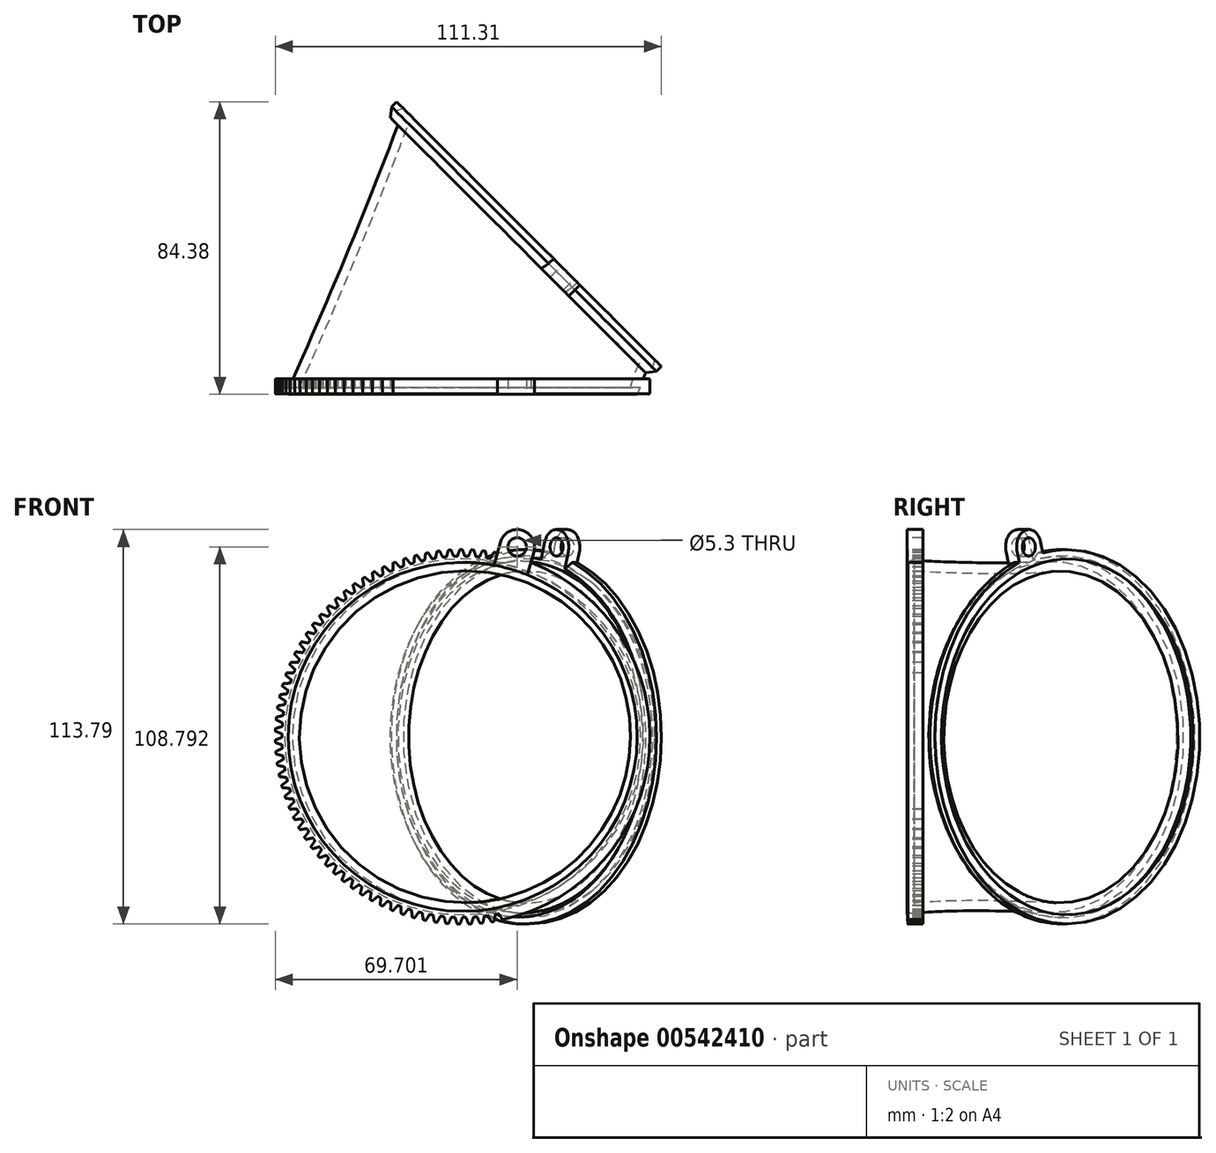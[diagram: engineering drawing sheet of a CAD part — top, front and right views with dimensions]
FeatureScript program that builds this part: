
annotation { "Feature Type Name" : "Feature", "Feature Type Description" : "" }
export const myFeature = defineFeature(function(context is Context, id is Id, definition is map)
    precondition{}
    {
        {
            var Q0;
            Q0=qCreatedBy(makeId("Front.planeOp"),FACE);
            var sketch = newSketch(context, id + "F0", { "sketchPlane" : qUnion([Q0])});
            skCircle(sketch, "E0", {"center": v(0, 0) * mm, "radius": 51 * mm});
            skSolve(sketch);
        }
        {
            var Q0;
            Q0=qCreatedBy(makeId("Top.planeOp"),FACE);
            var sketch = newSketch(context, id + "F1", { "sketchPlane" : qUnion([Q0])});
            skLineSegment(sketch, "E1", {"start": v(36.81, 28.52) * mm, "end": v(1.46, 63.87) * mm});
            skLineSegment(sketch, "E2", {"start": v(25, 0) * mm, "end": v(-25, 0) * mm});
            skLineSegment(sketch, "E3", {"start": v(19.13, 46.2) * mm, "end": v(0, 0) * mm});
            skPoint(sketch, "E4", {"position": v(19.13, 46.2) * mm});
            skLineSegment(sketch, "E5", {"start": v(9.57, 23.1) * mm, "end": v(14.19, 21.18) * mm});
            skSolve(sketch);
        }
        {
            var Q0;
            Q0=sQuery(id+"F1.wireOp",EDGE,"E1");
            cPlane(context, id + "F2", {"entities" : qUnion([Q0]), "cplaneType" : CPlaneType.LINE_ANGLE, "offset" : 25 * mm, "angle" : 90 * degree, "width" : 150 * mm, "height" : 150 * mm});
        }
        {
            var Q0;
            Q0=qCreatedBy(id+"F2.planeOp",FACE);
            var sketch = newSketch(context, id + "F3", { "sketchPlane" : qUnion([Q0])});
            skCircle(sketch, "E6", {"center": v(19.13, 0) * mm, "radius": 51 * mm});
            skSolve(sketch);
        }
        {
            var Q0;
            Q0=makeQuery(id+"F0.imprint","IMPRINT",FACE,{"disambiguationData":[TD([[makeQuery(id+"F0.imprint","IMPRINT",EDGE,{"derivedFrom":sQuery(id+"F0.wireOp",EDGE,"E0")}),1.0]])]});
            var Q1;
            Q1=makeQuery(id+"F3.imprint","IMPRINT",FACE,{"disambiguationData":[TD([[makeQuery(id+"F3.imprint","IMPRINT",EDGE,{"derivedFrom":sQuery(id+"F3.wireOp",EDGE,"E6")}),1.0]])]});
            loft(context, id + "F4", {"sheetProfilesArray" : [{ "sheetProfileEntities" : qUnion([Q0]) }, { "sheetProfileEntities" : qUnion([Q1]) }]});
        }
        {
            var Q0;
            Q0=makeQuery(id+"F4.opLoft","CAP_FACE",FACE,{"disambiguationData":[OSD([makeQuery(id+"F3.imprint","IMPRINT",FACE,{"disambiguationData":[TD([[makeQuery(id+"F3.imprint","IMPRINT",EDGE,{"derivedFrom":sQuery(id+"F3.wireOp",EDGE,"E6")}),1.0]])]})])],"isStart":true});
            var sketch = newSketch(context, id + "F5", { "sketchPlane" : qUnion([Q0])});
            skCircle(sketch, "E7", {"center": v(19.13, 0) * mm, "radius": 48 * mm});
            skSolve(sketch);
        }
        {
            var Q0;
            Q0=makeQuery(id+"F4.opLoft","CAP_FACE",FACE,{"disambiguationData":[OSD([makeQuery(id+"F3.imprint","IMPRINT",FACE,{"disambiguationData":[TD([[makeQuery(id+"F3.imprint","IMPRINT",EDGE,{"derivedFrom":sQuery(id+"F3.wireOp",EDGE,"E6")}),1.0]])]})])],"isStart":true});
            var sketch = newSketch(context, id + "F6", { "sketchPlane" : qUnion([Q0])});
            skCircle(sketch, "E8", {"center": v(19.13, 0) * mm, "radius": 54 * mm});
            skCircle(sketch, "E9", {"center": v(19.13, 0) * mm, "radius": 45 * mm});
            skSolve(sketch);
        }
        {
            var Q0;
            Q0=makeQuery(id+"F6.imprint","IMPRINT",FACE,{"disambiguationData":[TD([[makeQuery(id+"F6.imprint","IMPRINT",EDGE,{"derivedFrom":sQuery(id+"F6.wireOp",EDGE,"E8")}),1.0]])]});
            var Q1;
            Q1=makeQuery(id+"F5.imprint","IMPRINT",FACE,{"disambiguationData":[TD([[makeQuery(id+"F5.imprint","IMPRINT",EDGE,{"derivedFrom":sQuery(id+"F5.wireOp",EDGE,"E7")}),-1.0]])]});
            extrude(context, id + "F7", {"entities" : qUnion([Q0, Q1]), "operationType" : NewBodyOperationType.ADD, "oppositeDirection" : true, "depth" : 4.5 * mm, "offsetDistance" : 25 * mm});
        }
        {
            var Q0;
            Q0=makeQuery(id+"F4.opLoft","CAP_FACE",FACE,{"disambiguationData":[OSD([makeQuery(id+"F0.imprint","IMPRINT",FACE,{"disambiguationData":[TD([[makeQuery(id+"F0.imprint","IMPRINT",EDGE,{"derivedFrom":sQuery(id+"F0.wireOp",EDGE,"E0")}),1.0]])]})])],"isStart":true});
            var sketch = newSketch(context, id + "F8", { "sketchPlane" : qUnion([Q0])});
            skCircle(sketch, "E10", {"center": v(0, 0) * mm, "radius": 54 * mm});
            skSolve(sketch);
        }
        {
            var Q0;
            Q0=makeQuery(id+"F8.imprint","IMPRINT",FACE,{"disambiguationData":[TD([[makeQuery(id+"F8.imprint","IMPRINT",EDGE,{"derivedFrom":sQuery(id+"F8.wireOp",EDGE,"E10")}),1.0]])]});
            var Q1;
            Q1=makeQuery(id+"F8.imprint","IMPRINT",FACE,{"disambiguationData":[TD([[makeQuery(id+"F8.imprint","IMPRINT",EDGE,{"derivedFrom":makeQuery(id+"F4.opLoft","MID_CAP_EDGE",EDGE,{"disambiguationData":[OSD([sQuery(id+"F0.wireOp",EDGE,"E0")])],"capPos":0.0})}),1.0]])]});
            extrude(context, id + "F9", {"entities" : qUnion([Q0, Q1]), "operationType" : NewBodyOperationType.ADD, "oppositeDirection" : true, "depth" : 4.5 * mm, "offsetDistance" : 25 * mm});
        }
        {
            var Q0;
            {var subQ0=sQuery(id+"F3.wireOp",EDGE,"E6");var subQ1=sQuery(id+"F0.wireOp",EDGE,"E0");Q0=makeQuery(id+"F7.boolean.opBoolean","MERGE",FACE,{"derivedFrom":[makeQuery(id+"F4.opLoft","CAP_FACE",FACE,{"disambiguationData":[OSD([makeQuery(id+"F3.imprint","IMPRINT",FACE,{"disambiguationData":[TD([[makeQuery(id+"F3.imprint","IMPRINT",EDGE,{"derivedFrom":subQ0}),1.0]])]})])],"isStart":true}),makeQuery(id+"F7.opExtrude","CAP_FACE",FACE,{"disambiguationData":[OSD([subQ1,subQ0,sQuery(id+"F5.wireOp",EDGE,"E7")])],"isStart":true}),makeQuery(id+"F7.opExtrude","CAP_FACE",FACE,{"disambiguationData":[OSD([subQ1,subQ0,sQuery(id+"F6.wireOp",EDGE,"E8")])],"isStart":true})]});}
            var sketch = newSketch(context, id + "F10", { "sketchPlane" : qUnion([Q0])});
            skCircle(sketch, "E11", {"center": v(19.13, 0) * mm, "radius": 48 * mm});
            skSolve(sketch);
        }
        {
            var Q0;
            Q0=makeQuery(id+"F9.boolean.opBoolean","MERGE",FACE,{"derivedFrom":[makeQuery(id+"F4.opLoft","CAP_FACE",FACE,{"disambiguationData":[OSD([makeQuery(id+"F0.imprint","IMPRINT",FACE,{"disambiguationData":[TD([[makeQuery(id+"F0.imprint","IMPRINT",EDGE,{"derivedFrom":sQuery(id+"F0.wireOp",EDGE,"E0")}),1.0]])]})])],"isStart":true}),makeQuery(id+"F9.opExtrude","CAP_FACE",FACE,{"disambiguationData":[OSD([sQuery(id+"F8.wireOp",EDGE,"E10")])],"isStart":true})]});
            var sketch = newSketch(context, id + "F11", { "sketchPlane" : qUnion([Q0])});
            skCircle(sketch, "E12", {"center": v(0, 0) * mm, "radius": 48 * mm});
            skSolve(sketch);
        }
        {
            var Q1;
            Q1=makeQuery(id+"F11.imprint","IMPRINT",FACE,{"disambiguationData":[TD([[makeQuery(id+"F11.imprint","IMPRINT",EDGE,{"derivedFrom":sQuery(id+"F11.wireOp",EDGE,"E12")}),1.0]])]});
            var Q2;
            Q2=makeQuery(id+"F10.imprint","IMPRINT",FACE,{"disambiguationData":[TD([[makeQuery(id+"F10.imprint","IMPRINT",EDGE,{"derivedFrom":sQuery(id+"F10.wireOp",EDGE,"E11")}),1.0]])]});
            loft(context, id + "F12", {"operationType" : NewBodyOperationType.REMOVE, "sheetProfilesArray" : [{ "sheetProfileEntities" : qUnion([Q1]) }, { "sheetProfileEntities" : qUnion([Q2]) }]});
        }
        {
            var Q0;
            Q0=makeQuery(id+"F9.boolean.opBoolean","MERGE",FACE,{"derivedFrom":[makeQuery(id+"F4.opLoft","CAP_FACE",FACE,{"disambiguationData":[OSD([makeQuery(id+"F0.imprint","IMPRINT",FACE,{"disambiguationData":[TD([[makeQuery(id+"F0.imprint","IMPRINT",EDGE,{"derivedFrom":sQuery(id+"F0.wireOp",EDGE,"E0")}),1.0]])]})])],"isStart":true}),makeQuery(id+"F9.opExtrude","CAP_FACE",FACE,{"disambiguationData":[OSD([sQuery(id+"F8.wireOp",EDGE,"E10")])],"isStart":true})]});
            var sketch = newSketch(context, id + "F13", { "sketchPlane" : qUnion([Q0])});
            skCircle(sketch, "E13", {"center": v(0, 0) * mm, "radius": 50 * mm});
            skCircle(sketch, "E14", {"center": v(0, 0) * mm, "radius": 40 * mm});
            skSolve(sketch);
        }
        {
            var Q0;
            Q0=makeQuery(id+"F13.imprint","IMPRINT",FACE,{"disambiguationData":[TD([[makeQuery(id+"F13.imprint","IMPRINT",EDGE,{"derivedFrom":sQuery(id+"F13.wireOp",EDGE,"E13")}),1.0]])]});
            var Q1;
            Q1=makeQuery(id+"F13.imprint","IMPRINT",FACE,{"disambiguationData":[TD([[makeQuery(id+"F13.imprint","IMPRINT",EDGE,{"derivedFrom":sQuery(id+"F13.wireOp",EDGE,"E14")}),-1.0]])]});
            extrude(context, id + "F14", {"entities" : qUnion([Q0, Q1]), "operationType" : NewBodyOperationType.REMOVE, "oppositeDirection" : true, "depth" : 2 * mm, "offsetDistance" : 25 * mm});
        }
        {
            var Q0;
            {var subQ0=sQuery(id+"F3.wireOp",EDGE,"E6");var subQ1=sQuery(id+"F0.wireOp",EDGE,"E0");Q0=makeQuery(id+"F7.boolean.opBoolean","MERGE",FACE,{"derivedFrom":[makeQuery(id+"F4.opLoft","CAP_FACE",FACE,{"disambiguationData":[OSD([makeQuery(id+"F3.imprint","IMPRINT",FACE,{"disambiguationData":[TD([[makeQuery(id+"F3.imprint","IMPRINT",EDGE,{"derivedFrom":subQ0}),1.0]])]})])],"isStart":true}),makeQuery(id+"F7.opExtrude","CAP_FACE",FACE,{"disambiguationData":[OSD([subQ1,subQ0,sQuery(id+"F5.wireOp",EDGE,"E7")])],"isStart":true}),makeQuery(id+"F7.opExtrude","CAP_FACE",FACE,{"disambiguationData":[OSD([subQ1,subQ0,sQuery(id+"F6.wireOp",EDGE,"E8")])],"isStart":true})]});}
            var sketch = newSketch(context, id + "F15", { "sketchPlane" : qUnion([Q0])});
            skCircle(sketch, "E15", {"center": v(19.13, 0) * mm, "radius": 40 * mm});
            skCircle(sketch, "E16", {"center": v(19.13, 0) * mm, "radius": 51 * mm});
            skSolve(sketch);
        }
        {
            var Q0;
            Q0=makeQuery(id+"F15.imprint","IMPRINT",FACE,{"disambiguationData":[TD([[makeQuery(id+"F15.imprint","IMPRINT",EDGE,{"derivedFrom":sQuery(id+"F15.wireOp",EDGE,"E15")}),-1.0]])]});
            var Q1;
            Q1=makeQuery(id+"F15.imprint","IMPRINT",FACE,{"disambiguationData":[TD([[makeQuery(id+"F15.imprint","IMPRINT",EDGE,{"derivedFrom":sQuery(id+"F15.wireOp",EDGE,"E16")}),1.0]])]});
            extrude(context, id + "F16", {"entities" : qUnion([Q0, Q1]), "operationType" : NewBodyOperationType.REMOVE, "oppositeDirection" : true, "depth" : 2 * mm, "offsetDistance" : 25 * mm});
        }
        {
            var Q0;
            Q0=makeQuery(id+"F9.boolean.opBoolean","MERGE",FACE,{"derivedFrom":[makeQuery(id+"F4.opLoft","CAP_FACE",FACE,{"disambiguationData":[OSD([makeQuery(id+"F0.imprint","IMPRINT",FACE,{"disambiguationData":[TD([[makeQuery(id+"F0.imprint","IMPRINT",EDGE,{"derivedFrom":sQuery(id+"F0.wireOp",EDGE,"E0")}),1.0]])]})])],"isStart":true}),makeQuery(id+"F9.opExtrude","CAP_FACE",FACE,{"disambiguationData":[OSD([sQuery(id+"F8.wireOp",EDGE,"E10")])],"isStart":true})]});
            var sketch = newSketch(context, id + "F17", { "sketchPlane" : qUnion([Q0])});
            skLineSegment(sketch, "E17", {"start": v(0, 0) * mm, "end": v(-20, 0) * mm});
            skLineSegment(sketch, "E18", {"start": v(0, 0) * mm, "end": v(-4.8, 1.38) * mm});
            skLineSegment(sketch, "E19", {"start": v(0, 0) * mm, "end": v(4.8, -1.38) * mm});
            skArc(sketch, "E20", {"start": v(21.84, 58.03) * mm, "mid": v(17.09, 59.6) * mm, "end": v(12.23, 60.78) * mm});
            skLineSegment(sketch, "E21", {"start": v(-4.8, 1.38) * mm, "end": v(12.23, 60.78) * mm});
            skLineSegment(sketch, "E22", {"start": v(4.8, -1.38) * mm, "end": v(21.84, 58.03) * mm});
            skLineSegment(sketch, "E23", {"start": v(0, 0) * mm, "end": v(15.71, 54.8) * mm});
            skCircle(sketch, "E24", {"center": v(15.71, 54.8) * mm, "radius": 2.65 * mm});
            skSolve(sketch);
        }
        {
            var Q0;
            {var subQ1=sQuery(id+"F17.wireOp",EDGE,"E20");Q0=makeQuery(id+"F17.imprint","IMPRINT",FACE,{"disambiguationData":[TD([[makeQuery(id+"F17.imprint","IMPRINT",EDGE,{"derivedFrom":subQ1}),1.0]])]});}
            extrude(context, id + "F18", {"entities" : qUnion([Q0]), "operationType" : NewBodyOperationType.ADD, "oppositeDirection" : true, "depth" : 4.5 * mm, "offsetDistance" : 25 * mm});
        }
        {
            var Q0;
            Q0=makeQuery(id+"F9.opExtrude","CAP_EDGE",EDGE,{"disambiguationData":[OSD([sQuery(id+"F8.wireOp",EDGE,"E10")])],"isStart":true});
            chamfer(context, id + "F19", {"entities" : qUnion([Q0]), "chamferType" : ChamferType.TWO_OFFSETS, "width1" : 4 * mm, "oppositeDirection" : false, "width2" : .2 * mm, "tangentPropagation" : true});
        }
        {
            var Q0;
            Q0=makeQuery(id+"F18.opExtrude","SWEPT_EDGE",EDGE,{"disambiguationData":[OSD([sQuery(id+"F17.wireOp",EDGE,"E20"),sQuery(id+"F17.wireOp",EDGE,"E21")])]});
            var Q1;
            Q1=makeQuery(id+"F18.opExtrude","SWEPT_EDGE",EDGE,{"disambiguationData":[OSD([sQuery(id+"F17.wireOp",EDGE,"E20"),sQuery(id+"F17.wireOp",EDGE,"E22")])]});
            fillet(context, id + "F20", {"entities" : qUnion([Q0, Q1]), "radius" : 5 * mm, "tangentPropagation" : true, "allowEdgeOverflow" : false});
        }
        {
            var Q0;
            {var subQ0=sQuery(id+"F3.wireOp",EDGE,"E6");var subQ1=sQuery(id+"F0.wireOp",EDGE,"E0");Q0=makeQuery(id+"F7.boolean.opBoolean","MERGE",FACE,{"derivedFrom":[makeQuery(id+"F4.opLoft","CAP_FACE",FACE,{"disambiguationData":[OSD([makeQuery(id+"F3.imprint","IMPRINT",FACE,{"disambiguationData":[TD([[makeQuery(id+"F3.imprint","IMPRINT",EDGE,{"derivedFrom":subQ0}),1.0]])]})])],"isStart":true}),makeQuery(id+"F7.opExtrude","CAP_FACE",FACE,{"disambiguationData":[OSD([subQ1,subQ0,sQuery(id+"F5.wireOp",EDGE,"E7")])],"isStart":true}),makeQuery(id+"F7.opExtrude","CAP_FACE",FACE,{"disambiguationData":[OSD([subQ1,subQ0,sQuery(id+"F6.wireOp",EDGE,"E8")])],"isStart":true})]});}
            var sketch = newSketch(context, id + "F21", { "sketchPlane" : qUnion([Q0])});
            skArc(sketch, "E25", {"start": v(6.9, 60.78) * mm, "mid": v(2.04, 59.6) * mm, "end": v(-2.7, 58.03) * mm});
            skLineSegment(sketch, "E26", {"start": v(19.13, 0) * mm, "end": v(39.13, 0) * mm});
            skLineSegment(sketch, "E27", {"start": v(19.13, 0) * mm, "end": v(23.94, 1.38) * mm});
            skLineSegment(sketch, "E28", {"start": v(23.94, 1.38) * mm, "end": v(6.9, 60.78) * mm});
            skLineSegment(sketch, "E29", {"start": v(23.94, 1.38) * mm, "end": v(14.33, -1.38) * mm});
            skLineSegment(sketch, "E30", {"start": v(14.33, -1.38) * mm, "end": v(-2.7, 58.03) * mm});
            skLineSegment(sketch, "E31", {"start": v(19.13, 0) * mm, "end": v(3.42, 54.8) * mm});
            skCircle(sketch, "E32", {"center": v(3.42, 54.8) * mm, "radius": 2.65 * mm});
            skSolve(sketch);
        }
        {
            var Q0;
            {var subQ0=sQuery(id+"F21.wireOp",EDGE,"E25");Q0=makeQuery(id+"F21.imprint","IMPRINT",FACE,{"disambiguationData":[TD([[makeQuery(id+"F21.imprint","IMPRINT",EDGE,{"derivedFrom":subQ0}),1.0]])]});}
            extrude(context, id + "F22", {"entities" : qUnion([Q0]), "operationType" : NewBodyOperationType.ADD, "oppositeDirection" : true, "depth" : 4.5 * mm, "offsetDistance" : 25 * mm});
        }
        {
            var Q0;
            Q0=makeQuery(id+"F22.opExtrude","SWEPT_EDGE",EDGE,{"disambiguationData":[OSD([sQuery(id+"F21.wireOp",EDGE,"E25"),sQuery(id+"F21.wireOp",EDGE,"E30")])]});
            var Q1;
            Q1=makeQuery(id+"F22.opExtrude","SWEPT_EDGE",EDGE,{"disambiguationData":[OSD([sQuery(id+"F21.wireOp",EDGE,"E25"),sQuery(id+"F21.wireOp",EDGE,"E28")])]});
            fillet(context, id + "F23", {"entities" : qUnion([Q0, Q1]), "radius" : 5 * mm, "tangentPropagation" : true, "allowEdgeOverflow" : false});
        }
        {
            var Q0;
            Q0=makeQuery(id+"F7.opExtrude","CAP_EDGE",EDGE,{"disambiguationData":[OSD([sQuery(id+"F6.wireOp",EDGE,"E8")])],"isStart":false});
            chamfer(context, id + "F24", {"entities" : qUnion([Q0]), "chamferType" : ChamferType.TWO_OFFSETS, "width1" : 2.5 * mm, "oppositeDirection" : false, "width2" : 2 * mm, "tangentPropagation" : true});
        }
        {
            var Q0;
            {var subQ0=sQuery(id+"F8.wireOp",EDGE,"E10");Q0=makeQuery(id+"F18.boolean.opBoolean","MERGE",FACE,{"derivedFrom":[makeQuery(id+"F9.boolean.opBoolean","MERGE",FACE,{"derivedFrom":[makeQuery(id+"F4.opLoft","CAP_FACE",FACE,{"disambiguationData":[OSD([makeQuery(id+"F0.imprint","IMPRINT",FACE,{"disambiguationData":[TD([[makeQuery(id+"F0.imprint","IMPRINT",EDGE,{"derivedFrom":sQuery(id+"F0.wireOp",EDGE,"E0")}),1.0]])]})])],"isStart":true}),makeQuery(id+"F9.opExtrude","CAP_FACE",FACE,{"disambiguationData":[OSD([subQ0])],"isStart":true})]}),makeQuery(id+"F18.opExtrude","CAP_FACE",FACE,{"disambiguationData":[OSD([subQ0,sQuery(id+"F17.wireOp",EDGE,"E20"),sQuery(id+"F17.wireOp",EDGE,"E21"),sQuery(id+"F17.wireOp",EDGE,"E22"),sQuery(id+"F17.wireOp",EDGE,"E24")])],"isStart":true})]});}
            var sketch = newSketch(context, id + "F25", { "sketchPlane" : qUnion([Q0])});
            skArc(sketch, "E33", {"start": v(9.38, 53.18) * mm, "mid": v(9.25, 53.2) * mm, "end": v(9.12, 53.22) * mm});
            skLineSegment(sketch, "E34", {"start": v(0, 0) * mm, "end": v(9.38, 53.18) * mm});
            skLineSegment(sketch, "E35", {"start": v(0, 0) * mm, "end": v(9.42, 0) * mm});
            skLineSegment(sketch, "E36", {"start": v(0, 0) * mm, "end": v(6.11, 53.65) * mm});
            skLineSegment(sketch, "E37", {"start": v(0, 0) * mm, "end": v(8.97, 53.2) * mm});
            skLineSegment(sketch, "E38", {"start": v(0, 0) * mm, "end": v(6.5, 53.55) * mm});
            skLineSegment(sketch, "E39", {"start": v(7.75, 53.43) * mm, "end": v(0, 0) * mm});
            skLineSegment(sketch, "E40", {"start": v(6.54, 53.47) * mm, "end": v(6.93, 51.77) * mm});
            skLineSegment(sketch, "E41", {"start": v(8.05, 51.6) * mm, "end": v(8.91, 53.13) * mm});
            skArc(sketch, "E42", {"start": v(9.05, 51.3) * mm, "mid": v(8.86, 51.34) * mm, "end": v(8.67, 51.37) * mm});
            skLineSegment(sketch, "E43", {"start": v(9.38, 53.18) * mm, "end": v(9.11, 53.23) * mm});
            skArc(sketch, "E44.trimOffspring", {"start": v(6.37, 53.62) * mm, "mid": v(6.24, 53.64) * mm, "end": v(6.11, 53.65) * mm});
            skPoint(sketch, "E45.visualSharp", {"position": v(6.5, 53.6) * mm});
            skArc(sketch, "E45.filletArc", {"start": v(6.54, 53.47) * mm, "mid": v(6.48, 53.57) * mm, "end": v(6.37, 53.62) * mm});
            skPoint(sketch, "E46.visualSharp", {"position": v(8.98, 53.25) * mm});
            skArc(sketch, "E46.filletArc", {"start": v(9.12, 53.22) * mm, "mid": v(9, 53.2) * mm, "end": v(8.91, 53.13) * mm});
            skArc(sketch, "E47.trimOffspring", {"start": v(7.85, 51.5) * mm, "mid": v(7.48, 51.56) * mm, "end": v(7.1, 51.61) * mm});
            skPoint(sketch, "E48.visualSharp", {"position": v(6.96, 51.63) * mm});
            skArc(sketch, "E48.filletArc", {"start": v(6.93, 51.77) * mm, "mid": v(7, 51.66) * mm, "end": v(7.1, 51.61) * mm});
            skPoint(sketch, "E49.visualSharp", {"position": v(7.99, 51.48) * mm});
            skArc(sketch, "E49.filletArc", {"start": v(7.85, 51.5) * mm, "mid": v(7.97, 51.52) * mm, "end": v(8.05, 51.6) * mm});
            skLineSegment(sketch, "E50", {"start": v(6.11, 53.65) * mm, "end": v(8.15, 53.9) * mm});
            skLineSegment(sketch, "E51", {"start": v(8.15, 53.9) * mm, "end": v(9.38, 53.18) * mm});
            skLineSegment(sketch, "E52.1.0", {"start": v(4.85, 54.3) * mm, "end": v(6.12, 53.65) * mm});
            skPoint(sketch, "E52.1.1", {"position": v(4.83, 51.88) * mm});
            skPoint(sketch, "E52.1.2", {"position": v(5.72, 53.7) * mm});
            skArc(sketch, "E52.1.3", {"start": v(4.7, 51.89) * mm, "mid": v(4.32, 51.92) * mm, "end": v(3.94, 51.95) * mm});
            skPoint(sketch, "E52.1.4", {"position": v(3.23, 53.9) * mm});
            skPoint(sketch, "E52.1.5", {"position": v(3.8, 51.96) * mm});
            skLineSegment(sketch, "E52.1.6", {"start": v(4.9, 52) * mm, "end": v(5.66, 53.57) * mm});
            skLineSegment(sketch, "E52.1.7", {"start": v(2.83, 53.93) * mm, "end": v(4.85, 54.3) * mm});
            skLineSegment(sketch, "E52.1.8", {"start": v(3.27, 53.77) * mm, "end": v(3.76, 52.1) * mm});
            skArc(sketch, "E52.1.9", {"start": v(4.7, 51.89) * mm, "mid": v(4.81, 51.91) * mm, "end": v(4.9, 52) * mm});
            skArc(sketch, "E52.1.10", {"start": v(3.76, 52.1) * mm, "mid": v(3.83, 52) * mm, "end": v(3.94, 51.95) * mm});
            skArc(sketch, "E52.1.11", {"start": v(3.27, 53.77) * mm, "mid": v(3.2, 53.87) * mm, "end": v(3.09, 53.91) * mm});
            skArc(sketch, "E52.1.12", {"start": v(5.86, 53.68) * mm, "mid": v(5.74, 53.66) * mm, "end": v(5.66, 53.57) * mm});
            skArc(sketch, "E52.1.13", {"start": v(6.12, 53.65) * mm, "mid": v(5.99, 53.67) * mm, "end": v(5.86, 53.68) * mm});
            skArc(sketch, "E52.1.14", {"start": v(3.09, 53.91) * mm, "mid": v(2.96, 53.92) * mm, "end": v(2.83, 53.93) * mm});
            skLineSegment(sketch, "E52.1.15", {"start": v(6.12, 53.65) * mm, "end": v(5.85, 53.68) * mm});
            skLineSegment(sketch, "E52.2.0", {"start": v(1.53, 54.5) * mm, "end": v(2.84, 53.93) * mm});
            skPoint(sketch, "E52.2.1", {"position": v(1.66, 52.07) * mm});
            skPoint(sketch, "E52.2.2", {"position": v(2.44, 53.95) * mm});
            skArc(sketch, "E52.2.3", {"start": v(1.52, 52.08) * mm, "mid": v(1.14, 52.09) * mm, "end": v(0.77, 52.1) * mm});
            skPoint(sketch, "E52.2.4", {"position": v(-0.06, 54) * mm});
            skPoint(sketch, "E52.2.5", {"position": v(0.63, 52.1) * mm});
            skLineSegment(sketch, "E52.2.6", {"start": v(1.71, 52.2) * mm, "end": v(2.38, 53.82) * mm});
            skLineSegment(sketch, "E52.2.7", {"start": v(-0.46, 54) * mm, "end": v(1.53, 54.5) * mm});
            skLineSegment(sketch, "E52.2.8", {"start": v(-0.02, 53.87) * mm, "end": v(0.58, 52.23) * mm});
            skArc(sketch, "E52.2.9", {"start": v(1.52, 52.08) * mm, "mid": v(1.64, 52.1) * mm, "end": v(1.71, 52.2) * mm});
            skArc(sketch, "E52.2.10", {"start": v(0.58, 52.23) * mm, "mid": v(0.65, 52.13) * mm, "end": v(0.77, 52.1) * mm});
            skArc(sketch, "E52.2.11", {"start": v(-0.02, 53.87) * mm, "mid": v(-0.09, 53.96) * mm, "end": v(-0.2, 54) * mm});
            skArc(sketch, "E52.2.12", {"start": v(2.58, 53.94) * mm, "mid": v(2.46, 53.9) * mm, "end": v(2.38, 53.82) * mm});
            skArc(sketch, "E52.2.13", {"start": v(2.84, 53.93) * mm, "mid": v(2.7, 53.93) * mm, "end": v(2.58, 53.94) * mm});
            skArc(sketch, "E52.2.14", {"start": v(-0.2, 54) * mm, "mid": v(-0.33, 54) * mm, "end": v(-0.46, 54) * mm});
            skLineSegment(sketch, "E52.2.15", {"start": v(2.84, 53.93) * mm, "end": v(2.56, 53.94) * mm});
            skLineSegment(sketch, "E52.3.0", {"start": v(-1.8, 54.48) * mm, "end": v(-0.46, 54) * mm});
            skPoint(sketch, "E52.3.1", {"position": v(-1.52, 52.08) * mm});
            skPoint(sketch, "E52.3.2", {"position": v(-0.86, 54) * mm});
            skArc(sketch, "E52.3.3", {"start": v(-1.66, 52.07) * mm, "mid": v(-2.03, 52.06) * mm, "end": v(-2.41, 52.04) * mm});
            skPoint(sketch, "E52.3.4", {"position": v(-3.36, 53.9) * mm});
            skPoint(sketch, "E52.3.5", {"position": v(-2.55, 52.04) * mm});
            skLineSegment(sketch, "E52.3.6", {"start": v(-1.47, 52.2) * mm, "end": v(-0.9, 53.86) * mm});
            skLineSegment(sketch, "E52.3.7", {"start": v(-3.75, 53.87) * mm, "end": v(-1.8, 54.48) * mm});
            skLineSegment(sketch, "E52.3.8", {"start": v(-3.3, 53.77) * mm, "end": v(-2.6, 52.16) * mm});
            skArc(sketch, "E52.3.9", {"start": v(-1.66, 52.07) * mm, "mid": v(-1.54, 52.11) * mm, "end": v(-1.47, 52.2) * mm});
            skArc(sketch, "E52.3.10", {"start": v(-2.6, 52.16) * mm, "mid": v(-2.53, 52.07) * mm, "end": v(-2.41, 52.04) * mm});
            skArc(sketch, "E52.3.11", {"start": v(-3.3, 53.77) * mm, "mid": v(-3.38, 53.86) * mm, "end": v(-3.5, 53.89) * mm});
            skArc(sketch, "E52.3.12", {"start": v(-0.72, 54) * mm, "mid": v(-0.83, 53.96) * mm, "end": v(-0.9, 53.86) * mm});
            skArc(sketch, "E52.3.13", {"start": v(-0.46, 54) * mm, "mid": v(-0.59, 54) * mm, "end": v(-0.72, 54) * mm});
            skArc(sketch, "E52.3.14", {"start": v(-3.5, 53.89) * mm, "mid": v(-3.63, 53.88) * mm, "end": v(-3.75, 53.87) * mm});
            skLineSegment(sketch, "E52.3.15", {"start": v(-0.46, 54) * mm, "end": v(-0.73, 54) * mm});
            skLineSegment(sketch, "E52.4.0", {"start": v(-5.12, 54.27) * mm, "end": v(-3.75, 53.87) * mm});
            skPoint(sketch, "E52.4.1", {"position": v(-4.69, 51.89) * mm});
            skPoint(sketch, "E52.4.2", {"position": v(-4.15, 53.84) * mm});
            skArc(sketch, "E52.4.3", {"start": v(-4.83, 51.88) * mm, "mid": v(-5.2, 51.84) * mm, "end": v(-5.58, 51.8) * mm});
            skPoint(sketch, "E52.4.4", {"position": v(-6.64, 53.6) * mm});
            skPoint(sketch, "E52.4.5", {"position": v(-5.72, 51.79) * mm});
            skLineSegment(sketch, "E52.4.6", {"start": v(-4.65, 52.02) * mm, "end": v(-4.19, 53.7) * mm});
            skLineSegment(sketch, "E52.4.7", {"start": v(-7.03, 53.54) * mm, "end": v(-5.12, 54.27) * mm});
            skLineSegment(sketch, "E52.4.8", {"start": v(-6.57, 53.47) * mm, "end": v(-5.78, 51.9) * mm});
            skArc(sketch, "E52.4.9", {"start": v(-4.83, 51.88) * mm, "mid": v(-4.72, 51.92) * mm, "end": v(-4.65, 52.02) * mm});
            skArc(sketch, "E52.4.10", {"start": v(-5.78, 51.9) * mm, "mid": v(-5.7, 51.82) * mm, "end": v(-5.58, 51.8) * mm});
            skArc(sketch, "E52.4.11", {"start": v(-6.57, 53.47) * mm, "mid": v(-6.66, 53.55) * mm, "end": v(-6.77, 53.57) * mm});
            skArc(sketch, "E52.4.12", {"start": v(-4, 53.85) * mm, "mid": v(-4.12, 53.8) * mm, "end": v(-4.19, 53.7) * mm});
            skArc(sketch, "E52.4.13", {"start": v(-3.75, 53.87) * mm, "mid": v(-3.88, 53.86) * mm, "end": v(-4, 53.85) * mm});
            skArc(sketch, "E52.4.14", {"start": v(-6.77, 53.57) * mm, "mid": v(-6.9, 53.56) * mm, "end": v(-7.03, 53.54) * mm});
            skLineSegment(sketch, "E52.4.15", {"start": v(-3.75, 53.87) * mm, "end": v(-4.02, 53.85) * mm});
            skLineSegment(sketch, "E52.5.0", {"start": v(-8.41, 53.86) * mm, "end": v(-7.03, 53.54) * mm});
            skPoint(sketch, "E52.5.1", {"position": v(-7.84, 51.5) * mm});
            skPoint(sketch, "E52.5.2", {"position": v(-7.42, 53.49) * mm});
            skArc(sketch, "E52.5.3", {"start": v(-7.98, 51.49) * mm, "mid": v(-8.35, 51.43) * mm, "end": v(-8.73, 51.36) * mm});
            skPoint(sketch, "E52.5.4", {"position": v(-9.9, 53.09) * mm});
            skPoint(sketch, "E52.5.5", {"position": v(-8.86, 51.34) * mm});
            skLineSegment(sketch, "E52.5.6", {"start": v(-7.82, 51.64) * mm, "end": v(-7.45, 53.35) * mm});
            skLineSegment(sketch, "E52.5.7", {"start": v(-10.28, 53.01) * mm, "end": v(-8.41, 53.86) * mm});
            skLineSegment(sketch, "E52.5.8", {"start": v(-9.82, 52.97) * mm, "end": v(-8.93, 51.46) * mm});
            skArc(sketch, "E52.5.9", {"start": v(-7.98, 51.49) * mm, "mid": v(-7.87, 51.54) * mm, "end": v(-7.82, 51.64) * mm});
            skArc(sketch, "E52.5.10", {"start": v(-8.93, 51.46) * mm, "mid": v(-8.84, 51.38) * mm, "end": v(-8.73, 51.36) * mm});
            skArc(sketch, "E52.5.11", {"start": v(-9.82, 52.97) * mm, "mid": v(-9.9, 53.05) * mm, "end": v(-10.03, 53.06) * mm});
            skArc(sketch, "E52.5.12", {"start": v(-7.28, 53.5) * mm, "mid": v(-7.4, 53.46) * mm, "end": v(-7.45, 53.35) * mm});
            skArc(sketch, "E52.5.13", {"start": v(-7.03, 53.54) * mm, "mid": v(-7.15, 53.52) * mm, "end": v(-7.28, 53.5) * mm});
            skArc(sketch, "E52.5.14", {"start": v(-10.03, 53.06) * mm, "mid": v(-10.16, 53.04) * mm, "end": v(-10.28, 53.01) * mm});
            skLineSegment(sketch, "E52.5.15", {"start": v(-7.03, 53.54) * mm, "end": v(-7.3, 53.5) * mm});
            skLineSegment(sketch, "E52.6.0", {"start": v(-11.68, 53.25) * mm, "end": v(-10.28, 53.01) * mm});
            skPoint(sketch, "E52.6.1", {"position": v(-10.97, 50.93) * mm});
            skPoint(sketch, "E52.6.2", {"position": v(-10.67, 52.94) * mm});
            skArc(sketch, "E52.6.3", {"start": v(-11.1, 50.9) * mm, "mid": v(-11.47, 50.82) * mm, "end": v(-11.84, 50.74) * mm});
            skPoint(sketch, "E52.6.4", {"position": v(-13.1, 52.38) * mm});
            skPoint(sketch, "E52.6.5", {"position": v(-11.98, 50.7) * mm});
            skLineSegment(sketch, "E52.6.6", {"start": v(-10.95, 51.07) * mm, "end": v(-10.69, 52.8) * mm});
            skLineSegment(sketch, "E52.6.7", {"start": v(-13.5, 52.29) * mm, "end": v(-11.68, 53.25) * mm});
            skLineSegment(sketch, "E52.6.8", {"start": v(-13.03, 52.27) * mm, "end": v(-12.05, 50.82) * mm});
            skArc(sketch, "E52.6.9", {"start": v(-11.1, 50.9) * mm, "mid": v(-11, 50.96) * mm, "end": v(-10.95, 51.07) * mm});
            skArc(sketch, "E52.6.10", {"start": v(-12.05, 50.82) * mm, "mid": v(-11.96, 50.74) * mm, "end": v(-11.84, 50.74) * mm});
            skArc(sketch, "E52.6.11", {"start": v(-13.03, 52.27) * mm, "mid": v(-13.12, 52.34) * mm, "end": v(-13.24, 52.35) * mm});
            skArc(sketch, "E52.6.12", {"start": v(-10.53, 52.96) * mm, "mid": v(-10.64, 52.9) * mm, "end": v(-10.69, 52.8) * mm});
            skArc(sketch, "E52.6.13", {"start": v(-10.28, 53.01) * mm, "mid": v(-10.4, 52.99) * mm, "end": v(-10.53, 52.96) * mm});
            skArc(sketch, "E52.6.14", {"start": v(-13.24, 52.35) * mm, "mid": v(-13.37, 52.32) * mm, "end": v(-13.5, 52.29) * mm});
            skLineSegment(sketch, "E52.6.15", {"start": v(-10.28, 53.01) * mm, "end": v(-10.54, 52.96) * mm});
            skLineSegment(sketch, "E52.7.0", {"start": v(-14.9, 52.43) * mm, "end": v(-13.49, 52.29) * mm});
            skPoint(sketch, "E52.7.1", {"position": v(-14.05, 50.17) * mm});
            skPoint(sketch, "E52.7.2", {"position": v(-13.88, 52.19) * mm});
            skArc(sketch, "E52.7.3", {"start": v(-14.19, 50.13) * mm, "mid": v(-14.55, 50.03) * mm, "end": v(-14.91, 49.92) * mm});
            skPoint(sketch, "E52.7.4", {"position": v(-16.28, 51.49) * mm});
            skPoint(sketch, "E52.7.5", {"position": v(-15.04, 49.88) * mm});
            skLineSegment(sketch, "E52.7.6", {"start": v(-14.04, 50.3) * mm, "end": v(-13.89, 52.05) * mm});
            skLineSegment(sketch, "E52.7.7", {"start": v(-16.66, 51.37) * mm, "end": v(-14.9, 52.43) * mm});
            skLineSegment(sketch, "E52.7.8", {"start": v(-16.2, 51.38) * mm, "end": v(-15.13, 50) * mm});
            skArc(sketch, "E52.7.9", {"start": v(-14.19, 50.13) * mm, "mid": v(-14.09, 50.2) * mm, "end": v(-14.04, 50.3) * mm});
            skArc(sketch, "E52.7.10", {"start": v(-15.13, 50) * mm, "mid": v(-15.03, 49.92) * mm, "end": v(-14.91, 49.92) * mm});
            skArc(sketch, "E52.7.11", {"start": v(-16.2, 51.38) * mm, "mid": v(-16.3, 51.45) * mm, "end": v(-16.41, 51.45) * mm});
            skArc(sketch, "E52.7.12", {"start": v(-13.74, 52.22) * mm, "mid": v(-13.84, 52.16) * mm, "end": v(-13.89, 52.05) * mm});
            skArc(sketch, "E52.7.13", {"start": v(-13.49, 52.29) * mm, "mid": v(-13.62, 52.26) * mm, "end": v(-13.74, 52.22) * mm});
            skArc(sketch, "E52.7.14", {"start": v(-16.41, 51.45) * mm, "mid": v(-16.53, 51.4) * mm, "end": v(-16.66, 51.37) * mm});
            skLineSegment(sketch, "E52.7.15", {"start": v(-13.49, 52.29) * mm, "end": v(-13.75, 52.22) * mm});
            skLineSegment(sketch, "E52.8.0", {"start": v(-18.08, 51.43) * mm, "end": v(-16.65, 51.37) * mm});
            skPoint(sketch, "E52.8.1", {"position": v(-17.09, 49.22) * mm});
            skPoint(sketch, "E52.8.2", {"position": v(-17.03, 51.24) * mm});
            skArc(sketch, "E52.8.3", {"start": v(-17.22, 49.17) * mm, "mid": v(-17.57, 49.05) * mm, "end": v(-17.93, 48.92) * mm});
            skPoint(sketch, "E52.8.4", {"position": v(-19.39, 50.4) * mm});
            skPoint(sketch, "E52.8.5", {"position": v(-18.06, 48.87) * mm});
            skLineSegment(sketch, "E52.8.6", {"start": v(-17.08, 49.36) * mm, "end": v(-17.04, 51.1) * mm});
            skLineSegment(sketch, "E52.8.7", {"start": v(-19.76, 50.26) * mm, "end": v(-18.08, 51.43) * mm});
            skLineSegment(sketch, "E52.8.8", {"start": v(-19.3, 50.3) * mm, "end": v(-18.15, 48.97) * mm});
            skArc(sketch, "E52.8.9", {"start": v(-17.22, 49.17) * mm, "mid": v(-17.12, 49.24) * mm, "end": v(-17.08, 49.36) * mm});
            skArc(sketch, "E52.8.10", {"start": v(-18.15, 48.97) * mm, "mid": v(-18.05, 48.91) * mm, "end": v(-17.93, 48.92) * mm});
            skArc(sketch, "E52.8.11", {"start": v(-19.3, 50.3) * mm, "mid": v(-19.4, 50.36) * mm, "end": v(-19.52, 50.35) * mm});
            skArc(sketch, "E52.8.12", {"start": v(-16.9, 51.29) * mm, "mid": v(-17, 51.22) * mm, "end": v(-17.04, 51.1) * mm});
            skArc(sketch, "E52.8.13", {"start": v(-16.65, 51.37) * mm, "mid": v(-16.78, 51.33) * mm, "end": v(-16.9, 51.29) * mm});
            skArc(sketch, "E52.8.14", {"start": v(-19.52, 50.35) * mm, "mid": v(-19.64, 50.3) * mm, "end": v(-19.76, 50.26) * mm});
            skLineSegment(sketch, "E52.8.15", {"start": v(-16.65, 51.37) * mm, "end": v(-16.9, 51.28) * mm});
            skLineSegment(sketch, "E52.9.0", {"start": v(-21.18, 50.23) * mm, "end": v(-19.75, 50.26) * mm});
            skPoint(sketch, "E52.9.1", {"position": v(-20.06, 48.09) * mm});
            skPoint(sketch, "E52.9.2", {"position": v(-20.12, 50.1) * mm});
            skArc(sketch, "E52.9.3", {"start": v(-20.18, 48.03) * mm, "mid": v(-20.53, 47.88) * mm, "end": v(-20.88, 47.73) * mm});
            skPoint(sketch, "E52.9.4", {"position": v(-22.42, 49.12) * mm});
            skPoint(sketch, "E52.9.5", {"position": v(-21, 47.68) * mm});
            skLineSegment(sketch, "E52.9.6", {"start": v(-20.06, 48.22) * mm, "end": v(-20.12, 49.97) * mm});
            skLineSegment(sketch, "E52.9.7", {"start": v(-22.79, 48.96) * mm, "end": v(-21.18, 50.23) * mm});
            skLineSegment(sketch, "E52.9.8", {"start": v(-22.32, 49.02) * mm, "end": v(-21.1, 47.78) * mm});
            skArc(sketch, "E52.9.9", {"start": v(-20.18, 48.03) * mm, "mid": v(-20.1, 48.1) * mm, "end": v(-20.06, 48.22) * mm});
            skArc(sketch, "E52.9.10", {"start": v(-21.1, 47.78) * mm, "mid": v(-21, 47.72) * mm, "end": v(-20.88, 47.73) * mm});
            skArc(sketch, "E52.9.11", {"start": v(-22.32, 49.02) * mm, "mid": v(-22.43, 49.08) * mm, "end": v(-22.55, 49.07) * mm});
            skArc(sketch, "E52.9.12", {"start": v(-20, 50.16) * mm, "mid": v(-20.09, 50.09) * mm, "end": v(-20.12, 49.97) * mm});
            skArc(sketch, "E52.9.13", {"start": v(-19.75, 50.26) * mm, "mid": v(-19.87, 50.21) * mm, "end": v(-20, 50.16) * mm});
            skArc(sketch, "E52.9.14", {"start": v(-22.55, 49.07) * mm, "mid": v(-22.67, 49.01) * mm, "end": v(-22.79, 48.96) * mm});
            skLineSegment(sketch, "E52.9.15", {"start": v(-19.75, 50.26) * mm, "end": v(-20, 50.16) * mm});
            skLineSegment(sketch, "E52.10.0", {"start": v(-24.2, 48.85) * mm, "end": v(-22.78, 48.96) * mm});
            skPoint(sketch, "E52.10.1", {"position": v(-22.95, 46.77) * mm});
            skPoint(sketch, "E52.10.2", {"position": v(-23.14, 48.79) * mm});
            skArc(sketch, "E52.10.3", {"start": v(-23.07, 46.71) * mm, "mid": v(-23.41, 46.54) * mm, "end": v(-23.75, 46.37) * mm});
            skPoint(sketch, "E52.10.4", {"position": v(-25.38, 47.67) * mm});
            skPoint(sketch, "E52.10.5", {"position": v(-23.87, 46.3) * mm});
            skLineSegment(sketch, "E52.10.6", {"start": v(-22.96, 46.91) * mm, "end": v(-23.13, 48.65) * mm});
            skLineSegment(sketch, "E52.10.7", {"start": v(-25.73, 47.48) * mm, "end": v(-24.2, 48.85) * mm});
            skLineSegment(sketch, "E52.10.8", {"start": v(-25.27, 47.57) * mm, "end": v(-23.97, 46.4) * mm});
            skArc(sketch, "E52.10.9", {"start": v(-23.07, 46.71) * mm, "mid": v(-22.99, 46.8) * mm, "end": v(-22.96, 46.91) * mm});
            skArc(sketch, "E52.10.10", {"start": v(-23.97, 46.4) * mm, "mid": v(-23.87, 46.35) * mm, "end": v(-23.75, 46.37) * mm});
            skArc(sketch, "E52.10.11", {"start": v(-25.27, 47.57) * mm, "mid": v(-25.38, 47.62) * mm, "end": v(-25.5, 47.6) * mm});
            skArc(sketch, "E52.10.12", {"start": v(-23.01, 48.85) * mm, "mid": v(-23.1, 48.77) * mm, "end": v(-23.13, 48.65) * mm});
            skArc(sketch, "E52.10.13", {"start": v(-22.78, 48.96) * mm, "mid": v(-22.9, 48.9) * mm, "end": v(-23.01, 48.85) * mm});
            skArc(sketch, "E52.10.14", {"start": v(-25.5, 47.6) * mm, "mid": v(-25.61, 47.54) * mm, "end": v(-25.73, 47.48) * mm});
            skLineSegment(sketch, "E52.10.15", {"start": v(-22.78, 48.96) * mm, "end": v(-23.02, 48.84) * mm});
            skLineSegment(sketch, "E52.11.0", {"start": v(-27.13, 47.28) * mm, "end": v(-25.72, 47.48) * mm});
            skPoint(sketch, "E52.11.1", {"position": v(-25.76, 45.29) * mm});
            skPoint(sketch, "E52.11.2", {"position": v(-26.07, 47.29) * mm});
            skArc(sketch, "E52.11.3", {"start": v(-25.88, 45.22) * mm, "mid": v(-26.2, 45.03) * mm, "end": v(-26.53, 44.84) * mm});
            skPoint(sketch, "E52.11.4", {"position": v(-28.23, 46.03) * mm});
            skPoint(sketch, "E52.11.5", {"position": v(-26.65, 44.77) * mm});
            skLineSegment(sketch, "E52.11.6", {"start": v(-25.78, 45.42) * mm, "end": v(-26.05, 47.15) * mm});
            skLineSegment(sketch, "E52.11.7", {"start": v(-28.57, 45.82) * mm, "end": v(-27.13, 47.28) * mm});
            skLineSegment(sketch, "E52.11.8", {"start": v(-28.12, 45.94) * mm, "end": v(-26.76, 44.85) * mm});
            skArc(sketch, "E52.11.9", {"start": v(-25.88, 45.22) * mm, "mid": v(-25.8, 45.3) * mm, "end": v(-25.78, 45.42) * mm});
            skArc(sketch, "E52.11.10", {"start": v(-26.76, 44.85) * mm, "mid": v(-26.65, 44.81) * mm, "end": v(-26.53, 44.84) * mm});
            skArc(sketch, "E52.11.11", {"start": v(-28.12, 45.94) * mm, "mid": v(-28.24, 45.99) * mm, "end": v(-28.35, 45.96) * mm});
            skArc(sketch, "E52.11.12", {"start": v(-25.95, 47.36) * mm, "mid": v(-26.03, 47.27) * mm, "end": v(-26.05, 47.15) * mm});
            skArc(sketch, "E52.11.13", {"start": v(-25.72, 47.48) * mm, "mid": v(-25.84, 47.42) * mm, "end": v(-25.95, 47.36) * mm});
            skArc(sketch, "E52.11.14", {"start": v(-28.35, 45.96) * mm, "mid": v(-28.46, 45.89) * mm, "end": v(-28.57, 45.82) * mm});
            skLineSegment(sketch, "E52.11.15", {"start": v(-25.72, 47.48) * mm, "end": v(-25.96, 47.35) * mm});
            skLineSegment(sketch, "E52.12.0", {"start": v(-29.97, 45.54) * mm, "end": v(-28.57, 45.82) * mm});
            skPoint(sketch, "E52.12.1", {"position": v(-28.47, 43.63) * mm});
            skPoint(sketch, "E52.12.2", {"position": v(-28.9, 45.61) * mm});
            skArc(sketch, "E52.12.3", {"start": v(-28.59, 43.56) * mm, "mid": v(-28.9, 43.35) * mm, "end": v(-29.22, 43.14) * mm});
            skPoint(sketch, "E52.12.4", {"position": v(-30.99, 44.22) * mm});
            skPoint(sketch, "E52.12.5", {"position": v(-29.33, 43.06) * mm});
            skLineSegment(sketch, "E52.12.6", {"start": v(-28.5, 43.77) * mm, "end": v(-28.88, 45.47) * mm});
            skLineSegment(sketch, "E52.12.7", {"start": v(-31.31, 44) * mm, "end": v(-29.97, 45.54) * mm});
            skLineSegment(sketch, "E52.12.8", {"start": v(-30.87, 44.14) * mm, "end": v(-29.44, 43.14) * mm});
            skArc(sketch, "E52.12.9", {"start": v(-28.59, 43.56) * mm, "mid": v(-28.51, 43.65) * mm, "end": v(-28.5, 43.77) * mm});
            skArc(sketch, "E52.12.10", {"start": v(-29.44, 43.14) * mm, "mid": v(-29.33, 43.1) * mm, "end": v(-29.22, 43.14) * mm});
            skArc(sketch, "E52.12.11", {"start": v(-30.87, 44.14) * mm, "mid": v(-30.99, 44.18) * mm, "end": v(-31.1, 44.14) * mm});
            skArc(sketch, "E52.12.12", {"start": v(-28.79, 45.69) * mm, "mid": v(-28.87, 45.6) * mm, "end": v(-28.88, 45.47) * mm});
            skArc(sketch, "E52.12.13", {"start": v(-28.57, 45.82) * mm, "mid": v(-28.68, 45.75) * mm, "end": v(-28.79, 45.69) * mm});
            skArc(sketch, "E52.12.14", {"start": v(-31.1, 44.14) * mm, "mid": v(-31.2, 44.07) * mm, "end": v(-31.31, 44) * mm});
            skLineSegment(sketch, "E52.12.15", {"start": v(-28.57, 45.82) * mm, "end": v(-28.8, 45.68) * mm});
            skLineSegment(sketch, "E52.13.0", {"start": v(-32.69, 43.63) * mm, "end": v(-31.3, 44) * mm});
            skPoint(sketch, "E52.13.1", {"position": v(-31.08, 41.82) * mm});
            skPoint(sketch, "E52.13.2", {"position": v(-31.63, 43.76) * mm});
            skArc(sketch, "E52.13.3", {"start": v(-31.19, 41.73) * mm, "mid": v(-31.5, 41.5) * mm, "end": v(-31.8, 41.28) * mm});
            skPoint(sketch, "E52.13.4", {"position": v(-33.63, 42.25) * mm});
            skPoint(sketch, "E52.13.5", {"position": v(-31.9, 41.2) * mm});
            skLineSegment(sketch, "E52.13.6", {"start": v(-31.12, 41.95) * mm, "end": v(-31.6, 43.63) * mm});
            skLineSegment(sketch, "E52.13.7", {"start": v(-33.94, 42) * mm, "end": v(-32.69, 43.63) * mm});
            skLineSegment(sketch, "E52.13.8", {"start": v(-33.5, 42.18) * mm, "end": v(-32.02, 41.26) * mm});
            skArc(sketch, "E52.13.9", {"start": v(-31.19, 41.73) * mm, "mid": v(-31.12, 41.83) * mm, "end": v(-31.12, 41.95) * mm});
            skArc(sketch, "E52.13.10", {"start": v(-32.02, 41.26) * mm, "mid": v(-31.9, 41.23) * mm, "end": v(-31.8, 41.28) * mm});
            skArc(sketch, "E52.13.11", {"start": v(-33.5, 42.18) * mm, "mid": v(-33.62, 42.2) * mm, "end": v(-33.74, 42.16) * mm});
            skArc(sketch, "E52.13.12", {"start": v(-31.52, 43.85) * mm, "mid": v(-31.6, 43.75) * mm, "end": v(-31.6, 43.63) * mm});
            skArc(sketch, "E52.13.13", {"start": v(-31.3, 44) * mm, "mid": v(-31.42, 43.92) * mm, "end": v(-31.52, 43.85) * mm});
            skArc(sketch, "E52.13.14", {"start": v(-33.74, 42.16) * mm, "mid": v(-33.84, 42.08) * mm, "end": v(-33.94, 42) * mm});
            skLineSegment(sketch, "E52.13.15", {"start": v(-31.3, 44) * mm, "end": v(-31.53, 43.84) * mm});
            skLineSegment(sketch, "E52.14.0", {"start": v(-35.28, 41.55) * mm, "end": v(-33.93, 42) * mm});
            skPoint(sketch, "E52.14.1", {"position": v(-33.57, 39.84) * mm});
            skPoint(sketch, "E52.14.2", {"position": v(-34.24, 41.75) * mm});
            skArc(sketch, "E52.14.3", {"start": v(-33.67, 39.75) * mm, "mid": v(-33.96, 39.5) * mm, "end": v(-34.25, 39.26) * mm});
            skPoint(sketch, "E52.14.4", {"position": v(-36.14, 40.12) * mm});
            skPoint(sketch, "E52.14.5", {"position": v(-34.35, 39.17) * mm});
            skLineSegment(sketch, "E52.14.6", {"start": v(-33.62, 39.97) * mm, "end": v(-34.2, 41.62) * mm});
            skLineSegment(sketch, "E52.14.7", {"start": v(-36.44, 39.85) * mm, "end": v(-35.28, 41.55) * mm});
            skLineSegment(sketch, "E52.14.8", {"start": v(-36.02, 40.06) * mm, "end": v(-34.47, 39.24) * mm});
            skArc(sketch, "E52.14.9", {"start": v(-33.67, 39.75) * mm, "mid": v(-33.61, 39.85) * mm, "end": v(-33.62, 39.97) * mm});
            skArc(sketch, "E52.14.10", {"start": v(-34.47, 39.24) * mm, "mid": v(-34.36, 39.21) * mm, "end": v(-34.25, 39.26) * mm});
            skArc(sketch, "E52.14.11", {"start": v(-36.02, 40.06) * mm, "mid": v(-36.13, 40.08) * mm, "end": v(-36.24, 40.03) * mm});
            skArc(sketch, "E52.14.12", {"start": v(-34.13, 41.84) * mm, "mid": v(-34.2, 41.74) * mm, "end": v(-34.2, 41.62) * mm});
            skArc(sketch, "E52.14.13", {"start": v(-33.93, 42) * mm, "mid": v(-34.03, 41.92) * mm, "end": v(-34.13, 41.84) * mm});
            skArc(sketch, "E52.14.14", {"start": v(-36.24, 40.03) * mm, "mid": v(-36.34, 39.94) * mm, "end": v(-36.44, 39.85) * mm});
            skLineSegment(sketch, "E52.14.15", {"start": v(-33.93, 42) * mm, "end": v(-34.14, 41.84) * mm});
            skLineSegment(sketch, "E52.15.0", {"start": v(-37.75, 39.32) * mm, "end": v(-36.43, 39.86) * mm});
            skPoint(sketch, "E52.15.1", {"position": v(-35.94, 37.72) * mm});
            skPoint(sketch, "E52.15.2", {"position": v(-36.73, 39.59) * mm});
            skArc(sketch, "E52.15.3", {"start": v(-36.04, 37.63) * mm, "mid": v(-36.3, 37.36) * mm, "end": v(-36.58, 37.1) * mm});
            skPoint(sketch, "E52.15.4", {"position": v(-38.52, 37.85) * mm});
            skPoint(sketch, "E52.15.5", {"position": v(-36.68, 37) * mm});
            skLineSegment(sketch, "E52.15.6", {"start": v(-36, 37.85) * mm, "end": v(-36.67, 39.46) * mm});
            skLineSegment(sketch, "E52.15.7", {"start": v(-38.8, 37.56) * mm, "end": v(-37.75, 39.32) * mm});
            skLineSegment(sketch, "E52.15.8", {"start": v(-38.4, 37.79) * mm, "end": v(-36.8, 37.06) * mm});
            skArc(sketch, "E52.15.9", {"start": v(-36.04, 37.63) * mm, "mid": v(-35.98, 37.73) * mm, "end": v(-36, 37.85) * mm});
            skArc(sketch, "E52.15.10", {"start": v(-36.8, 37.06) * mm, "mid": v(-36.68, 37.05) * mm, "end": v(-36.58, 37.1) * mm});
            skArc(sketch, "E52.15.11", {"start": v(-38.4, 37.79) * mm, "mid": v(-38.51, 37.8) * mm, "end": v(-38.62, 37.75) * mm});
            skArc(sketch, "E52.15.12", {"start": v(-36.62, 39.68) * mm, "mid": v(-36.68, 39.58) * mm, "end": v(-36.67, 39.46) * mm});
            skArc(sketch, "E52.15.13", {"start": v(-36.43, 39.86) * mm, "mid": v(-36.53, 39.77) * mm, "end": v(-36.62, 39.68) * mm});
            skArc(sketch, "E52.15.14", {"start": v(-38.62, 37.75) * mm, "mid": v(-38.7, 37.65) * mm, "end": v(-38.8, 37.56) * mm});
            skLineSegment(sketch, "E52.15.15", {"start": v(-36.43, 39.86) * mm, "end": v(-36.63, 39.68) * mm});
            skLineSegment(sketch, "E52.16.0", {"start": v(-40.08, 36.95) * mm, "end": v(-38.8, 37.56) * mm});
            skPoint(sketch, "E52.16.1", {"position": v(-38.17, 35.46) * mm});
            skPoint(sketch, "E52.16.2", {"position": v(-39.07, 37.28) * mm});
            skArc(sketch, "E52.16.3", {"start": v(-38.26, 35.36) * mm, "mid": v(-38.52, 35.08) * mm, "end": v(-38.77, 34.8) * mm});
            skPoint(sketch, "E52.16.4", {"position": v(-40.75, 35.43) * mm});
            skPoint(sketch, "E52.16.5", {"position": v(-38.86, 34.7) * mm});
            skLineSegment(sketch, "E52.16.6", {"start": v(-38.23, 35.59) * mm, "end": v(-39, 37.15) * mm});
            skLineSegment(sketch, "E52.16.7", {"start": v(-41.02, 35.12) * mm, "end": v(-40.08, 36.95) * mm});
            skLineSegment(sketch, "E52.16.8", {"start": v(-40.62, 35.38) * mm, "end": v(-39, 34.75) * mm});
            skArc(sketch, "E52.16.9", {"start": v(-38.26, 35.36) * mm, "mid": v(-38.21, 35.47) * mm, "end": v(-38.23, 35.59) * mm});
            skArc(sketch, "E52.16.10", {"start": v(-39, 34.75) * mm, "mid": v(-38.87, 34.74) * mm, "end": v(-38.77, 34.8) * mm});
            skArc(sketch, "E52.16.11", {"start": v(-40.62, 35.38) * mm, "mid": v(-40.74, 35.38) * mm, "end": v(-40.85, 35.32) * mm});
            skArc(sketch, "E52.16.12", {"start": v(-38.97, 37.38) * mm, "mid": v(-39.03, 37.27) * mm, "end": v(-39, 37.15) * mm});
            skArc(sketch, "E52.16.13", {"start": v(-38.8, 37.56) * mm, "mid": v(-38.88, 37.47) * mm, "end": v(-38.97, 37.38) * mm});
            skArc(sketch, "E52.16.14", {"start": v(-40.85, 35.32) * mm, "mid": v(-40.93, 35.22) * mm, "end": v(-41.02, 35.12) * mm});
            skLineSegment(sketch, "E52.16.15", {"start": v(-38.8, 37.56) * mm, "end": v(-38.98, 37.37) * mm});
            skLineSegment(sketch, "E52.17.0", {"start": v(-42.26, 34.44) * mm, "end": v(-41.01, 35.13) * mm});
            skPoint(sketch, "E52.17.1", {"position": v(-40.26, 33.07) * mm});
            skPoint(sketch, "E52.17.2", {"position": v(-41.27, 34.82) * mm});
            skArc(sketch, "E52.17.3", {"start": v(-40.35, 32.96) * mm, "mid": v(-40.59, 32.67) * mm, "end": v(-40.82, 32.37) * mm});
            skPoint(sketch, "E52.17.4", {"position": v(-42.84, 32.88) * mm});
            skPoint(sketch, "E52.17.5", {"position": v(-40.9, 32.26) * mm});
            skLineSegment(sketch, "E52.17.6", {"start": v(-40.33, 33.19) * mm, "end": v(-41.2, 34.7) * mm});
            skLineSegment(sketch, "E52.17.7", {"start": v(-43.08, 32.56) * mm, "end": v(-42.26, 34.44) * mm});
            skLineSegment(sketch, "E52.17.8", {"start": v(-42.7, 32.83) * mm, "end": v(-41.04, 32.3) * mm});
            skArc(sketch, "E52.17.9", {"start": v(-40.35, 32.96) * mm, "mid": v(-40.3, 33.07) * mm, "end": v(-40.33, 33.19) * mm});
            skArc(sketch, "E52.17.10", {"start": v(-41.04, 32.3) * mm, "mid": v(-40.92, 32.3) * mm, "end": v(-40.82, 32.37) * mm});
            skArc(sketch, "E52.17.11", {"start": v(-42.7, 32.83) * mm, "mid": v(-42.83, 32.83) * mm, "end": v(-42.92, 32.77) * mm});
            skArc(sketch, "E52.17.12", {"start": v(-41.18, 34.93) * mm, "mid": v(-41.23, 34.82) * mm, "end": v(-41.2, 34.7) * mm});
            skArc(sketch, "E52.17.13", {"start": v(-41.01, 35.13) * mm, "mid": v(-41.1, 35.03) * mm, "end": v(-41.18, 34.93) * mm});
            skArc(sketch, "E52.17.14", {"start": v(-42.92, 32.77) * mm, "mid": v(-43, 32.66) * mm, "end": v(-43.08, 32.56) * mm});
            skLineSegment(sketch, "E52.17.15", {"start": v(-41.01, 35.13) * mm, "end": v(-41.19, 34.92) * mm});
            skLineSegment(sketch, "E52.18.0", {"start": v(-44.28, 31.8) * mm, "end": v(-43.08, 32.56) * mm});
            skPoint(sketch, "E52.18.1", {"position": v(-42.2, 30.55) * mm});
            skPoint(sketch, "E52.18.2", {"position": v(-43.32, 32.24) * mm});
            skArc(sketch, "E52.18.3", {"start": v(-42.28, 30.44) * mm, "mid": v(-42.5, 30.13) * mm, "end": v(-42.72, 29.82) * mm});
            skPoint(sketch, "E52.18.4", {"position": v(-44.76, 30.2) * mm});
            skPoint(sketch, "E52.18.5", {"position": v(-42.8, 29.71) * mm});
            skLineSegment(sketch, "E52.18.6", {"start": v(-42.28, 30.67) * mm, "end": v(-43.24, 32.13) * mm});
            skLineSegment(sketch, "E52.18.7", {"start": v(-44.99, 29.87) * mm, "end": v(-44.28, 31.8) * mm});
            skLineSegment(sketch, "E52.18.8", {"start": v(-44.63, 30.17) * mm, "end": v(-42.93, 29.74) * mm});
            skArc(sketch, "E52.18.9", {"start": v(-42.28, 30.44) * mm, "mid": v(-42.24, 30.55) * mm, "end": v(-42.28, 30.67) * mm});
            skArc(sketch, "E52.18.10", {"start": v(-42.93, 29.74) * mm, "mid": v(-42.81, 29.75) * mm, "end": v(-42.72, 29.82) * mm});
            skArc(sketch, "E52.18.11", {"start": v(-44.63, 30.17) * mm, "mid": v(-44.75, 30.16) * mm, "end": v(-44.84, 30.09) * mm});
            skArc(sketch, "E52.18.12", {"start": v(-43.23, 32.36) * mm, "mid": v(-43.27, 32.24) * mm, "end": v(-43.24, 32.13) * mm});
            skArc(sketch, "E52.18.13", {"start": v(-43.08, 32.56) * mm, "mid": v(-43.15, 32.46) * mm, "end": v(-43.23, 32.36) * mm});
            skArc(sketch, "E52.18.14", {"start": v(-44.84, 30.09) * mm, "mid": v(-44.91, 29.98) * mm, "end": v(-44.99, 29.87) * mm});
            skLineSegment(sketch, "E52.18.15", {"start": v(-43.08, 32.56) * mm, "end": v(-43.24, 32.35) * mm});
            skLineSegment(sketch, "E52.19.0", {"start": v(-46.13, 29.04) * mm, "end": v(-44.98, 29.88) * mm});
            skPoint(sketch, "E52.19.1", {"position": v(-43.99, 27.92) * mm});
            skPoint(sketch, "E52.19.2", {"position": v(-45.2, 29.54) * mm});
            skArc(sketch, "E52.19.3", {"start": v(-44.06, 27.8) * mm, "mid": v(-44.26, 27.49) * mm, "end": v(-44.46, 27.16) * mm});
            skPoint(sketch, "E52.19.4", {"position": v(-46.52, 27.42) * mm});
            skPoint(sketch, "E52.19.5", {"position": v(-44.53, 27.05) * mm});
            skLineSegment(sketch, "E52.19.6", {"start": v(-44.07, 28.03) * mm, "end": v(-45.12, 29.43) * mm});
            skLineSegment(sketch, "E52.19.7", {"start": v(-46.72, 27.07) * mm, "end": v(-46.13, 29.04) * mm});
            skLineSegment(sketch, "E52.19.8", {"start": v(-46.38, 27.4) * mm, "end": v(-44.67, 27.07) * mm});
            skArc(sketch, "E52.19.9", {"start": v(-44.06, 27.8) * mm, "mid": v(-44.03, 27.92) * mm, "end": v(-44.07, 28.03) * mm});
            skArc(sketch, "E52.19.10", {"start": v(-44.67, 27.07) * mm, "mid": v(-44.55, 27.09) * mm, "end": v(-44.46, 27.16) * mm});
            skArc(sketch, "E52.19.11", {"start": v(-46.38, 27.4) * mm, "mid": v(-46.5, 27.38) * mm, "end": v(-46.6, 27.3) * mm});
            skArc(sketch, "E52.19.12", {"start": v(-45.12, 29.66) * mm, "mid": v(-45.16, 29.54) * mm, "end": v(-45.12, 29.43) * mm});
            skArc(sketch, "E52.19.13", {"start": v(-44.98, 29.88) * mm, "mid": v(-45.05, 29.77) * mm, "end": v(-45.12, 29.66) * mm});
            skArc(sketch, "E52.19.14", {"start": v(-46.6, 27.3) * mm, "mid": v(-46.66, 27.19) * mm, "end": v(-46.72, 27.07) * mm});
            skLineSegment(sketch, "E52.19.15", {"start": v(-44.98, 29.88) * mm, "end": v(-45.13, 29.65) * mm});
            skLineSegment(sketch, "E52.20.0", {"start": v(-47.82, 26.17) * mm, "end": v(-46.72, 27.08) * mm});
            skPoint(sketch, "E52.20.1", {"position": v(-45.6, 25.19) * mm});
            skPoint(sketch, "E52.20.2", {"position": v(-46.92, 26.73) * mm});
            skArc(sketch, "E52.20.3", {"start": v(-45.67, 25.07) * mm, "mid": v(-45.85, 24.74) * mm, "end": v(-46.03, 24.4) * mm});
            skPoint(sketch, "E52.20.4", {"position": v(-48.1, 24.53) * mm});
            skPoint(sketch, "E52.20.5", {"position": v(-46.1, 24.28) * mm});
            skLineSegment(sketch, "E52.20.6", {"start": v(-45.7, 25.3) * mm, "end": v(-46.83, 26.63) * mm});
            skLineSegment(sketch, "E52.20.7", {"start": v(-48.29, 24.17) * mm, "end": v(-47.82, 26.17) * mm});
            skLineSegment(sketch, "E52.20.8", {"start": v(-47.97, 24.51) * mm, "end": v(-46.23, 24.3) * mm});
            skArc(sketch, "E52.20.9", {"start": v(-45.67, 25.07) * mm, "mid": v(-45.65, 25.19) * mm, "end": v(-45.7, 25.3) * mm});
            skArc(sketch, "E52.20.10", {"start": v(-46.23, 24.3) * mm, "mid": v(-46.12, 24.32) * mm, "end": v(-46.03, 24.4) * mm});
            skArc(sketch, "E52.20.11", {"start": v(-47.97, 24.51) * mm, "mid": v(-48.09, 24.5) * mm, "end": v(-48.17, 24.4) * mm});
            skArc(sketch, "E52.20.12", {"start": v(-46.85, 26.85) * mm, "mid": v(-46.87, 26.74) * mm, "end": v(-46.83, 26.63) * mm});
            skArc(sketch, "E52.20.13", {"start": v(-46.72, 27.08) * mm, "mid": v(-46.78, 26.97) * mm, "end": v(-46.85, 26.85) * mm});
            skArc(sketch, "E52.20.14", {"start": v(-48.17, 24.4) * mm, "mid": v(-48.23, 24.3) * mm, "end": v(-48.29, 24.17) * mm});
            skLineSegment(sketch, "E52.20.15", {"start": v(-46.72, 27.08) * mm, "end": v(-46.85, 26.84) * mm});
            skLineSegment(sketch, "E52.21.0", {"start": v(-49.33, 23.2) * mm, "end": v(-48.28, 24.18) * mm});
            skPoint(sketch, "E52.21.1", {"position": v(-47.06, 22.36) * mm});
            skPoint(sketch, "E52.21.2", {"position": v(-48.46, 23.82) * mm});
            skArc(sketch, "E52.21.3", {"start": v(-47.12, 22.24) * mm, "mid": v(-47.28, 21.9) * mm, "end": v(-47.43, 21.55) * mm});
            skPoint(sketch, "E52.21.4", {"position": v(-49.51, 21.55) * mm});
            skPoint(sketch, "E52.21.5", {"position": v(-47.5, 21.43) * mm});
            skLineSegment(sketch, "E52.21.6", {"start": v(-47.15, 22.46) * mm, "end": v(-48.36, 23.72) * mm});
            skLineSegment(sketch, "E52.21.7", {"start": v(-49.67, 21.19) * mm, "end": v(-49.33, 23.2) * mm});
            skLineSegment(sketch, "E52.21.8", {"start": v(-49.37, 21.54) * mm, "end": v(-47.63, 21.43) * mm});
            skArc(sketch, "E52.21.9", {"start": v(-47.12, 22.24) * mm, "mid": v(-47.1, 22.36) * mm, "end": v(-47.15, 22.46) * mm});
            skArc(sketch, "E52.21.10", {"start": v(-47.63, 21.43) * mm, "mid": v(-47.51, 21.46) * mm, "end": v(-47.43, 21.55) * mm});
            skArc(sketch, "E52.21.11", {"start": v(-49.37, 21.54) * mm, "mid": v(-49.49, 21.52) * mm, "end": v(-49.57, 21.42) * mm});
            skArc(sketch, "E52.21.12", {"start": v(-48.4, 23.95) * mm, "mid": v(-48.42, 23.83) * mm, "end": v(-48.36, 23.72) * mm});
            skArc(sketch, "E52.21.13", {"start": v(-48.28, 24.18) * mm, "mid": v(-48.34, 24.06) * mm, "end": v(-48.4, 23.95) * mm});
            skArc(sketch, "E52.21.14", {"start": v(-49.57, 21.42) * mm, "mid": v(-49.62, 21.3) * mm, "end": v(-49.67, 21.19) * mm});
            skLineSegment(sketch, "E52.21.15", {"start": v(-48.28, 24.18) * mm, "end": v(-48.4, 23.94) * mm});
            skLineSegment(sketch, "E52.22.0", {"start": v(-50.65, 20.16) * mm, "end": v(-49.67, 21.2) * mm});
            skPoint(sketch, "E52.22.1", {"position": v(-48.33, 19.45) * mm});
            skPoint(sketch, "E52.22.2", {"position": v(-49.82, 20.82) * mm});
            skArc(sketch, "E52.22.3", {"start": v(-48.38, 19.32) * mm, "mid": v(-48.52, 18.97) * mm, "end": v(-48.66, 18.62) * mm});
            skPoint(sketch, "E52.22.4", {"position": v(-50.73, 18.5) * mm});
            skPoint(sketch, "E52.22.5", {"position": v(-48.7, 18.5) * mm});
            skLineSegment(sketch, "E52.22.6", {"start": v(-48.43, 19.55) * mm, "end": v(-49.72, 20.73) * mm});
            skLineSegment(sketch, "E52.22.7", {"start": v(-50.87, 18.12) * mm, "end": v(-50.65, 20.16) * mm});
            skLineSegment(sketch, "E52.22.8", {"start": v(-50.6, 18.5) * mm, "end": v(-48.85, 18.5) * mm});
            skArc(sketch, "E52.22.9", {"start": v(-48.38, 19.32) * mm, "mid": v(-48.37, 19.44) * mm, "end": v(-48.43, 19.55) * mm});
            skArc(sketch, "E52.22.10", {"start": v(-48.85, 18.5) * mm, "mid": v(-48.73, 18.53) * mm, "end": v(-48.66, 18.62) * mm});
            skArc(sketch, "E52.22.11", {"start": v(-50.6, 18.5) * mm, "mid": v(-50.7, 18.46) * mm, "end": v(-50.78, 18.36) * mm});
            skArc(sketch, "E52.22.12", {"start": v(-49.77, 20.95) * mm, "mid": v(-49.78, 20.83) * mm, "end": v(-49.72, 20.73) * mm});
            skArc(sketch, "E52.22.13", {"start": v(-49.67, 21.2) * mm, "mid": v(-49.72, 21.07) * mm, "end": v(-49.77, 20.95) * mm});
            skArc(sketch, "E52.22.14", {"start": v(-50.78, 18.36) * mm, "mid": v(-50.83, 18.24) * mm, "end": v(-50.87, 18.12) * mm});
            skLineSegment(sketch, "E52.22.15", {"start": v(-49.67, 21.2) * mm, "end": v(-49.77, 20.94) * mm});
            skLineSegment(sketch, "E52.23.0", {"start": v(-51.78, 17.03) * mm, "end": v(-50.87, 18.12) * mm});
            skPoint(sketch, "E52.23.1", {"position": v(-49.43, 16.47) * mm});
            skPoint(sketch, "E52.23.2", {"position": v(-51, 17.75) * mm});
            skArc(sketch, "E52.23.3", {"start": v(-49.47, 16.34) * mm, "mid": v(-49.59, 15.98) * mm, "end": v(-49.7, 15.62) * mm});
            skPoint(sketch, "E52.23.4", {"position": v(-51.77, 15.37) * mm});
            skPoint(sketch, "E52.23.5", {"position": v(-49.74, 15.49) * mm});
            skLineSegment(sketch, "E52.23.6", {"start": v(-49.54, 16.56) * mm, "end": v(-50.9, 17.66) * mm});
            skLineSegment(sketch, "E52.23.7", {"start": v(-51.88, 14.98) * mm, "end": v(-51.78, 17.03) * mm});
            skLineSegment(sketch, "E52.23.8", {"start": v(-51.63, 15.38) * mm, "end": v(-49.88, 15.48) * mm});
            skArc(sketch, "E52.23.9", {"start": v(-49.47, 16.34) * mm, "mid": v(-49.47, 16.46) * mm, "end": v(-49.54, 16.56) * mm});
            skArc(sketch, "E52.23.10", {"start": v(-49.88, 15.48) * mm, "mid": v(-49.77, 15.52) * mm, "end": v(-49.7, 15.62) * mm});
            skArc(sketch, "E52.23.11", {"start": v(-51.63, 15.38) * mm, "mid": v(-51.74, 15.33) * mm, "end": v(-51.8, 15.23) * mm});
            skArc(sketch, "E52.23.12", {"start": v(-50.95, 17.88) * mm, "mid": v(-50.96, 17.76) * mm, "end": v(-50.9, 17.66) * mm});
            skArc(sketch, "E52.23.13", {"start": v(-50.87, 18.12) * mm, "mid": v(-50.91, 18) * mm, "end": v(-50.95, 17.88) * mm});
            skArc(sketch, "E52.23.14", {"start": v(-51.8, 15.23) * mm, "mid": v(-51.84, 15.1) * mm, "end": v(-51.88, 14.98) * mm});
            skLineSegment(sketch, "E52.23.15", {"start": v(-50.87, 18.12) * mm, "end": v(-50.96, 17.87) * mm});
            skLineSegment(sketch, "E52.24.0", {"start": v(-52.73, 13.84) * mm, "end": v(-51.88, 14.99) * mm});
            skPoint(sketch, "E52.24.1", {"position": v(-50.34, 13.43) * mm});
            skPoint(sketch, "E52.24.2", {"position": v(-51.99, 14.6) * mm});
            skArc(sketch, "E52.24.3", {"start": v(-50.38, 13.3) * mm, "mid": v(-50.47, 12.93) * mm, "end": v(-50.56, 12.56) * mm});
            skPoint(sketch, "E52.24.4", {"position": v(-52.6, 12.18) * mm});
            skPoint(sketch, "E52.24.5", {"position": v(-50.6, 12.43) * mm});
            skLineSegment(sketch, "E52.24.6", {"start": v(-50.45, 13.5) * mm, "end": v(-51.87, 14.52) * mm});
            skLineSegment(sketch, "E52.24.7", {"start": v(-52.7, 11.8) * mm, "end": v(-52.73, 13.84) * mm});
            skLineSegment(sketch, "E52.24.8", {"start": v(-52.47, 12.2) * mm, "end": v(-50.73, 12.4) * mm});
            skArc(sketch, "E52.24.9", {"start": v(-50.38, 13.3) * mm, "mid": v(-50.38, 13.41) * mm, "end": v(-50.45, 13.5) * mm});
            skArc(sketch, "E52.24.10", {"start": v(-50.73, 12.4) * mm, "mid": v(-50.63, 12.46) * mm, "end": v(-50.56, 12.56) * mm});
            skArc(sketch, "E52.24.11", {"start": v(-52.47, 12.2) * mm, "mid": v(-52.58, 12.15) * mm, "end": v(-52.64, 12.05) * mm});
            skArc(sketch, "E52.24.12", {"start": v(-51.95, 14.74) * mm, "mid": v(-51.95, 14.62) * mm, "end": v(-51.87, 14.52) * mm});
            skArc(sketch, "E52.24.13", {"start": v(-51.88, 14.99) * mm, "mid": v(-51.91, 14.87) * mm, "end": v(-51.95, 14.74) * mm});
            skArc(sketch, "E52.24.14", {"start": v(-52.64, 12.05) * mm, "mid": v(-52.67, 11.92) * mm, "end": v(-52.7, 11.8) * mm});
            skLineSegment(sketch, "E52.24.15", {"start": v(-51.88, 14.99) * mm, "end": v(-51.95, 14.73) * mm});
            skLineSegment(sketch, "E52.25.0", {"start": v(-53.47, 10.6) * mm, "end": v(-52.7, 11.8) * mm});
            skPoint(sketch, "E52.25.1", {"position": v(-51.07, 10.33) * mm});
            skPoint(sketch, "E52.25.2", {"position": v(-52.78, 11.4) * mm});
            skArc(sketch, "E52.25.3", {"start": v(-51.1, 10.2) * mm, "mid": v(-51.17, 9.83) * mm, "end": v(-51.24, 9.45) * mm});
            skPoint(sketch, "E52.25.4", {"position": v(-53.25, 8.95) * mm});
            skPoint(sketch, "E52.25.5", {"position": v(-51.26, 9.32) * mm});
            skLineSegment(sketch, "E52.25.6", {"start": v(-51.18, 10.4) * mm, "end": v(-52.66, 11.33) * mm});
            skLineSegment(sketch, "E52.25.7", {"start": v(-53.32, 8.56) * mm, "end": v(-53.47, 10.6) * mm});
            skLineSegment(sketch, "E52.25.8", {"start": v(-53.11, 8.98) * mm, "end": v(-51.4, 9.3) * mm});
            skArc(sketch, "E52.25.9", {"start": v(-51.1, 10.2) * mm, "mid": v(-51.1, 10.31) * mm, "end": v(-51.18, 10.4) * mm});
            skArc(sketch, "E52.25.10", {"start": v(-51.4, 9.3) * mm, "mid": v(-51.3, 9.35) * mm, "end": v(-51.24, 9.45) * mm});
            skArc(sketch, "E52.25.11", {"start": v(-53.11, 8.98) * mm, "mid": v(-53.22, 8.92) * mm, "end": v(-53.28, 8.81) * mm});
            skArc(sketch, "E52.25.12", {"start": v(-52.75, 11.55) * mm, "mid": v(-52.74, 11.43) * mm, "end": v(-52.66, 11.33) * mm});
            skArc(sketch, "E52.25.13", {"start": v(-52.7, 11.8) * mm, "mid": v(-52.72, 11.67) * mm, "end": v(-52.75, 11.55) * mm});
            skArc(sketch, "E52.25.14", {"start": v(-53.28, 8.81) * mm, "mid": v(-53.3, 8.69) * mm, "end": v(-53.32, 8.56) * mm});
            skLineSegment(sketch, "E52.25.15", {"start": v(-52.7, 11.8) * mm, "end": v(-52.75, 11.53) * mm});
            skLineSegment(sketch, "E52.26.0", {"start": v(-54.02, 7.32) * mm, "end": v(-53.32, 8.56) * mm});
            skPoint(sketch, "E52.26.1", {"position": v(-51.6, 7.2) * mm});
            skPoint(sketch, "E52.26.2", {"position": v(-53.38, 8.17) * mm});
            skArc(sketch, "E52.26.3", {"start": v(-51.62, 7.06) * mm, "mid": v(-51.67, 6.69) * mm, "end": v(-51.72, 6.31) * mm});
            skPoint(sketch, "E52.26.4", {"position": v(-53.7, 5.7) * mm});
            skPoint(sketch, "E52.26.5", {"position": v(-51.73, 6.18) * mm});
            skLineSegment(sketch, "E52.26.6", {"start": v(-51.72, 7.27) * mm, "end": v(-53.26, 8.1) * mm});
            skLineSegment(sketch, "E52.26.7", {"start": v(-53.74, 5.3) * mm, "end": v(-54.02, 7.32) * mm});
            skLineSegment(sketch, "E52.26.8", {"start": v(-53.56, 5.72) * mm, "end": v(-51.87, 6.14) * mm});
            skArc(sketch, "E52.26.9", {"start": v(-51.62, 7.06) * mm, "mid": v(-51.64, 7.18) * mm, "end": v(-51.72, 7.27) * mm});
            skArc(sketch, "E52.26.10", {"start": v(-51.87, 6.14) * mm, "mid": v(-51.76, 6.2) * mm, "end": v(-51.72, 6.31) * mm});
            skArc(sketch, "E52.26.11", {"start": v(-53.56, 5.72) * mm, "mid": v(-53.67, 5.66) * mm, "end": v(-53.71, 5.55) * mm});
            skArc(sketch, "E52.26.12", {"start": v(-53.36, 8.3) * mm, "mid": v(-53.34, 8.19) * mm, "end": v(-53.26, 8.1) * mm});
            skArc(sketch, "E52.26.13", {"start": v(-53.32, 8.56) * mm, "mid": v(-53.34, 8.44) * mm, "end": v(-53.36, 8.3) * mm});
            skArc(sketch, "E52.26.14", {"start": v(-53.71, 5.55) * mm, "mid": v(-53.73, 5.42) * mm, "end": v(-53.74, 5.3) * mm});
            skLineSegment(sketch, "E52.26.15", {"start": v(-53.32, 8.56) * mm, "end": v(-53.36, 8.3) * mm});
            skLineSegment(sketch, "E52.27.0", {"start": v(-54.36, 4.02) * mm, "end": v(-53.74, 5.3) * mm});
            skPoint(sketch, "E52.27.1", {"position": v(-51.94, 4.04) * mm});
            skPoint(sketch, "E52.27.2", {"position": v(-53.78, 4.9) * mm});
            skArc(sketch, "E52.27.3", {"start": v(-51.95, 3.9) * mm, "mid": v(-51.98, 3.53) * mm, "end": v(-52, 3.15) * mm});
            skPoint(sketch, "E52.27.4", {"position": v(-53.95, 2.4) * mm});
            skPoint(sketch, "E52.27.5", {"position": v(-52.01, 3.01) * mm});
            skLineSegment(sketch, "E52.27.6", {"start": v(-52.07, 4.1) * mm, "end": v(-53.65, 4.84) * mm});
            skLineSegment(sketch, "E52.27.7", {"start": v(-53.96, 2) * mm, "end": v(-54.36, 4.02) * mm});
            skLineSegment(sketch, "E52.27.8", {"start": v(-53.81, 2.45) * mm, "end": v(-52.14, 2.97) * mm});
            skArc(sketch, "E52.27.9", {"start": v(-51.95, 3.9) * mm, "mid": v(-51.98, 4.02) * mm, "end": v(-52.07, 4.1) * mm});
            skArc(sketch, "E52.27.10", {"start": v(-52.14, 2.97) * mm, "mid": v(-52.05, 3.04) * mm, "end": v(-52, 3.15) * mm});
            skArc(sketch, "E52.27.11", {"start": v(-53.81, 2.45) * mm, "mid": v(-53.91, 2.38) * mm, "end": v(-53.95, 2.27) * mm});
            skArc(sketch, "E52.27.12", {"start": v(-53.76, 5.04) * mm, "mid": v(-53.74, 4.92) * mm, "end": v(-53.65, 4.84) * mm});
            skArc(sketch, "E52.27.13", {"start": v(-53.74, 5.3) * mm, "mid": v(-53.75, 5.17) * mm, "end": v(-53.76, 5.04) * mm});
            skArc(sketch, "E52.27.14", {"start": v(-53.95, 2.27) * mm, "mid": v(-53.96, 2.14) * mm, "end": v(-53.96, 2) * mm});
            skLineSegment(sketch, "E52.27.15", {"start": v(-53.74, 5.3) * mm, "end": v(-53.76, 5.03) * mm});
            skLineSegment(sketch, "E52.28.0", {"start": v(-54.5, 0.7) * mm, "end": v(-53.96, 2.01) * mm});
            skPoint(sketch, "E52.28.1", {"position": v(-52.1, 0.87) * mm});
            skPoint(sketch, "E52.28.2", {"position": v(-53.98, 1.61) * mm});
            skArc(sketch, "E52.28.3", {"start": v(-52.1, 0.73) * mm, "mid": v(-52.1, 0.35) * mm, "end": v(-52.1, -0.03) * mm});
            skPoint(sketch, "E52.28.4", {"position": v(-54, -0.89) * mm});
            skPoint(sketch, "E52.28.5", {"position": v(-52.1, -0.17) * mm});
            skLineSegment(sketch, "E52.28.6", {"start": v(-52.22, 0.92) * mm, "end": v(-53.85, 1.56) * mm});
            skLineSegment(sketch, "E52.28.7", {"start": v(-53.98, -1.29) * mm, "end": v(-54.5, 0.7) * mm});
            skLineSegment(sketch, "E52.28.8", {"start": v(-53.86, -0.84) * mm, "end": v(-52.23, -0.22) * mm});
            skArc(sketch, "E52.28.9", {"start": v(-52.1, 0.73) * mm, "mid": v(-52.13, 0.84) * mm, "end": v(-52.22, 0.92) * mm});
            skArc(sketch, "E52.28.10", {"start": v(-52.23, -0.22) * mm, "mid": v(-52.14, -0.14) * mm, "end": v(-52.1, -0.03) * mm});
            skArc(sketch, "E52.28.11", {"start": v(-53.86, -0.84) * mm, "mid": v(-53.96, -0.91) * mm, "end": v(-54, -1.03) * mm});
            skArc(sketch, "E52.28.12", {"start": v(-53.97, 1.75) * mm, "mid": v(-53.94, 1.64) * mm, "end": v(-53.85, 1.56) * mm});
            skArc(sketch, "E52.28.13", {"start": v(-53.96, 2.01) * mm, "mid": v(-53.97, 1.88) * mm, "end": v(-53.97, 1.75) * mm});
            skArc(sketch, "E52.28.14", {"start": v(-54, -1.03) * mm, "mid": v(-53.99, -1.16) * mm, "end": v(-53.98, -1.29) * mm});
            skLineSegment(sketch, "E52.28.15", {"start": v(-53.96, 2.01) * mm, "end": v(-53.97, 1.74) * mm});
            skLineSegment(sketch, "E52.29.0", {"start": v(-54.45, -2.63) * mm, "end": v(-53.98, -1.28) * mm});
            skPoint(sketch, "E52.29.1", {"position": v(-52.05, -2.31) * mm});
            skPoint(sketch, "E52.29.2", {"position": v(-53.97, -1.68) * mm});
            skArc(sketch, "E52.29.3", {"start": v(-52.04, -2.45) * mm, "mid": v(-52.02, -2.83) * mm, "end": v(-52, -3.2) * mm});
            skPoint(sketch, "E52.29.4", {"position": v(-53.84, -4.18) * mm});
            skPoint(sketch, "E52.29.5", {"position": v(-52, -3.34) * mm});
            skLineSegment(sketch, "E52.29.6", {"start": v(-52.18, -2.27) * mm, "end": v(-53.84, -1.72) * mm});
            skLineSegment(sketch, "E52.29.7", {"start": v(-53.8, -4.58) * mm, "end": v(-54.45, -2.63) * mm});
            skLineSegment(sketch, "E52.29.8", {"start": v(-53.71, -4.12) * mm, "end": v(-52.12, -3.4) * mm});
            skArc(sketch, "E52.29.9", {"start": v(-52.04, -2.45) * mm, "mid": v(-52.08, -2.34) * mm, "end": v(-52.18, -2.27) * mm});
            skArc(sketch, "E52.29.10", {"start": v(-52.12, -3.4) * mm, "mid": v(-52.03, -3.32) * mm, "end": v(-52, -3.2) * mm});
            skArc(sketch, "E52.29.11", {"start": v(-53.71, -4.12) * mm, "mid": v(-53.8, -4.2) * mm, "end": v(-53.83, -4.32) * mm});
            skArc(sketch, "E52.29.12", {"start": v(-53.98, -1.54) * mm, "mid": v(-53.94, -1.65) * mm, "end": v(-53.84, -1.72) * mm});
            skArc(sketch, "E52.29.13", {"start": v(-53.98, -1.28) * mm, "mid": v(-53.98, -1.41) * mm, "end": v(-53.98, -1.54) * mm});
            skArc(sketch, "E52.29.14", {"start": v(-53.83, -4.32) * mm, "mid": v(-53.82, -4.45) * mm, "end": v(-53.8, -4.58) * mm});
            skLineSegment(sketch, "E52.29.15", {"start": v(-53.98, -1.28) * mm, "end": v(-53.98, -1.55) * mm});
            skLineSegment(sketch, "E52.30.0", {"start": v(-54.19, -5.94) * mm, "end": v(-53.8, -4.57) * mm});
            skPoint(sketch, "E52.30.1", {"position": v(-51.81, -5.48) * mm});
            skPoint(sketch, "E52.30.2", {"position": v(-53.77, -4.97) * mm});
            skArc(sketch, "E52.30.3", {"start": v(-51.8, -5.62) * mm, "mid": v(-51.75, -6) * mm, "end": v(-51.7, -6.37) * mm});
            skPoint(sketch, "E52.30.4", {"position": v(-53.48, -7.45) * mm});
            skPoint(sketch, "E52.30.5", {"position": v(-51.7, -6.5) * mm});
            skLineSegment(sketch, "E52.30.6", {"start": v(-51.94, -5.45) * mm, "end": v(-53.64, -5) * mm});
            skLineSegment(sketch, "E52.30.7", {"start": v(-53.43, -7.85) * mm, "end": v(-54.19, -5.94) * mm});
            skLineSegment(sketch, "E52.30.8", {"start": v(-53.36, -7.39) * mm, "end": v(-51.81, -6.57) * mm});
            skArc(sketch, "E52.30.9", {"start": v(-51.8, -5.62) * mm, "mid": v(-51.84, -5.5) * mm, "end": v(-51.94, -5.45) * mm});
            skArc(sketch, "E52.30.10", {"start": v(-51.81, -6.57) * mm, "mid": v(-51.73, -6.49) * mm, "end": v(-51.7, -6.37) * mm});
            skArc(sketch, "E52.30.11", {"start": v(-53.36, -7.39) * mm, "mid": v(-53.44, -7.47) * mm, "end": v(-53.46, -7.6) * mm});
            skArc(sketch, "E52.30.12", {"start": v(-53.78, -4.83) * mm, "mid": v(-53.74, -4.94) * mm, "end": v(-53.64, -5) * mm});
            skArc(sketch, "E52.30.13", {"start": v(-53.8, -4.57) * mm, "mid": v(-53.8, -4.7) * mm, "end": v(-53.78, -4.83) * mm});
            skArc(sketch, "E52.30.14", {"start": v(-53.46, -7.6) * mm, "mid": v(-53.45, -7.72) * mm, "end": v(-53.43, -7.85) * mm});
            skLineSegment(sketch, "E52.30.15", {"start": v(-53.8, -4.57) * mm, "end": v(-53.78, -4.84) * mm});
            skLineSegment(sketch, "E52.31.0", {"start": v(-53.72, -9.24) * mm, "end": v(-53.43, -7.84) * mm});
            skPoint(sketch, "E52.31.1", {"position": v(-51.38, -8.63) * mm});
            skPoint(sketch, "E52.31.2", {"position": v(-53.37, -8.24) * mm});
            skArc(sketch, "E52.31.3", {"start": v(-51.36, -8.76) * mm, "mid": v(-51.3, -9.14) * mm, "end": v(-51.22, -9.5) * mm});
            skPoint(sketch, "E52.31.4", {"position": v(-52.93, -10.7) * mm});
            skPoint(sketch, "E52.31.5", {"position": v(-51.2, -9.64) * mm});
            skLineSegment(sketch, "E52.31.6", {"start": v(-51.52, -8.6) * mm, "end": v(-53.23, -8.26) * mm});
            skLineSegment(sketch, "E52.31.7", {"start": v(-52.85, -11.1) * mm, "end": v(-53.72, -9.24) * mm});
            skLineSegment(sketch, "E52.31.8", {"start": v(-52.8, -10.63) * mm, "end": v(-51.32, -9.72) * mm});
            skArc(sketch, "E52.31.9", {"start": v(-51.36, -8.76) * mm, "mid": v(-51.41, -8.66) * mm, "end": v(-51.52, -8.6) * mm});
            skArc(sketch, "E52.31.10", {"start": v(-51.32, -9.72) * mm, "mid": v(-51.24, -9.63) * mm, "end": v(-51.22, -9.5) * mm});
            skArc(sketch, "E52.31.11", {"start": v(-52.8, -10.63) * mm, "mid": v(-52.89, -10.72) * mm, "end": v(-52.9, -10.84) * mm});
            skArc(sketch, "E52.31.12", {"start": v(-53.39, -8.1) * mm, "mid": v(-53.34, -8.2) * mm, "end": v(-53.23, -8.26) * mm});
            skArc(sketch, "E52.31.13", {"start": v(-53.43, -7.84) * mm, "mid": v(-53.4, -7.97) * mm, "end": v(-53.39, -8.1) * mm});
            skArc(sketch, "E52.31.14", {"start": v(-52.9, -10.84) * mm, "mid": v(-52.88, -10.96) * mm, "end": v(-52.85, -11.1) * mm});
            skLineSegment(sketch, "E52.31.15", {"start": v(-53.43, -7.84) * mm, "end": v(-53.39, -8.1) * mm});
            skLineSegment(sketch, "E52.32.0", {"start": v(-53.06, -12.5) * mm, "end": v(-52.85, -11.08) * mm});
            skPoint(sketch, "E52.32.1", {"position": v(-50.76, -11.74) * mm});
            skPoint(sketch, "E52.32.2", {"position": v(-52.77, -11.48) * mm});
            skArc(sketch, "E52.32.3", {"start": v(-50.73, -11.88) * mm, "mid": v(-50.64, -12.25) * mm, "end": v(-50.55, -12.61) * mm});
            skPoint(sketch, "E52.32.4", {"position": v(-52.18, -13.9) * mm});
            skPoint(sketch, "E52.32.5", {"position": v(-50.52, -12.75) * mm});
            skLineSegment(sketch, "E52.32.6", {"start": v(-50.9, -11.73) * mm, "end": v(-52.63, -11.5) * mm});
            skLineSegment(sketch, "E52.32.7", {"start": v(-52.07, -14.3) * mm, "end": v(-53.06, -12.5) * mm});
            skLineSegment(sketch, "E52.32.8", {"start": v(-52.06, -13.83) * mm, "end": v(-50.63, -12.83) * mm});
            skArc(sketch, "E52.32.9", {"start": v(-50.73, -11.88) * mm, "mid": v(-50.79, -11.78) * mm, "end": v(-50.9, -11.73) * mm});
            skArc(sketch, "E52.32.10", {"start": v(-50.63, -12.83) * mm, "mid": v(-50.56, -12.73) * mm, "end": v(-50.55, -12.61) * mm});
            skArc(sketch, "E52.32.11", {"start": v(-52.06, -13.83) * mm, "mid": v(-52.14, -13.92) * mm, "end": v(-52.14, -14.04) * mm});
            skArc(sketch, "E52.32.12", {"start": v(-52.8, -11.34) * mm, "mid": v(-52.74, -11.44) * mm, "end": v(-52.63, -11.5) * mm});
            skArc(sketch, "E52.32.13", {"start": v(-52.85, -11.08) * mm, "mid": v(-52.82, -11.21) * mm, "end": v(-52.8, -11.34) * mm});
            skArc(sketch, "E52.32.14", {"start": v(-52.14, -14.04) * mm, "mid": v(-52.1, -14.17) * mm, "end": v(-52.07, -14.3) * mm});
            skLineSegment(sketch, "E52.32.15", {"start": v(-52.85, -11.08) * mm, "end": v(-52.8, -11.35) * mm});
            skLineSegment(sketch, "E52.33.0", {"start": v(-52.2, -15.7) * mm, "end": v(-52.08, -14.29) * mm});
            skPoint(sketch, "E52.33.1", {"position": v(-49.95, -14.82) * mm});
            skPoint(sketch, "E52.33.2", {"position": v(-51.97, -14.67) * mm});
            skArc(sketch, "E52.33.3", {"start": v(-49.9, -14.95) * mm, "mid": v(-49.8, -15.31) * mm, "end": v(-49.69, -15.67) * mm});
            skPoint(sketch, "E52.33.4", {"position": v(-51.23, -17.06) * mm});
            skPoint(sketch, "E52.33.5", {"position": v(-49.65, -15.8) * mm});
            skLineSegment(sketch, "E52.33.6", {"start": v(-50.09, -14.8) * mm, "end": v(-51.83, -14.68) * mm});
            skLineSegment(sketch, "E52.33.7", {"start": v(-51.1, -17.44) * mm, "end": v(-52.2, -15.7) * mm});
            skLineSegment(sketch, "E52.33.8", {"start": v(-51.12, -16.97) * mm, "end": v(-49.75, -15.89) * mm});
            skArc(sketch, "E52.33.9", {"start": v(-49.9, -14.95) * mm, "mid": v(-49.98, -14.85) * mm, "end": v(-50.09, -14.8) * mm});
            skArc(sketch, "E52.33.10", {"start": v(-49.75, -15.89) * mm, "mid": v(-49.69, -15.8) * mm, "end": v(-49.69, -15.67) * mm});
            skArc(sketch, "E52.33.11", {"start": v(-51.12, -16.97) * mm, "mid": v(-51.2, -17.07) * mm, "end": v(-51.19, -17.2) * mm});
            skArc(sketch, "E52.33.12", {"start": v(-52, -14.54) * mm, "mid": v(-51.94, -14.64) * mm, "end": v(-51.83, -14.68) * mm});
            skArc(sketch, "E52.33.13", {"start": v(-52.08, -14.29) * mm, "mid": v(-52.04, -14.41) * mm, "end": v(-52, -14.54) * mm});
            skArc(sketch, "E52.33.14", {"start": v(-51.19, -17.2) * mm, "mid": v(-51.15, -17.32) * mm, "end": v(-51.1, -17.44) * mm});
            skLineSegment(sketch, "E52.33.15", {"start": v(-52.08, -14.29) * mm, "end": v(-52, -14.55) * mm});
            skLineSegment(sketch, "E52.34.0", {"start": v(-51.15, -18.86) * mm, "end": v(-51.1, -17.43) * mm});
            skPoint(sketch, "E52.34.1", {"position": v(-48.95, -17.84) * mm});
            skPoint(sketch, "E52.34.2", {"position": v(-50.98, -17.81) * mm});
            skArc(sketch, "E52.34.3", {"start": v(-48.9, -17.96) * mm, "mid": v(-48.77, -18.32) * mm, "end": v(-48.64, -18.67) * mm});
            skPoint(sketch, "E52.34.4", {"position": v(-50.1, -20.15) * mm});
            skPoint(sketch, "E52.34.5", {"position": v(-48.59, -18.8) * mm});
            skLineSegment(sketch, "E52.34.6", {"start": v(-49.1, -17.83) * mm, "end": v(-50.84, -17.81) * mm});
            skLineSegment(sketch, "E52.34.7", {"start": v(-49.95, -20.52) * mm, "end": v(-51.15, -18.86) * mm});
            skLineSegment(sketch, "E52.34.8", {"start": v(-50, -20.06) * mm, "end": v(-48.7, -18.9) * mm});
            skArc(sketch, "E52.34.9", {"start": v(-48.9, -17.96) * mm, "mid": v(-48.98, -17.87) * mm, "end": v(-49.1, -17.83) * mm});
            skArc(sketch, "E52.34.10", {"start": v(-48.7, -18.9) * mm, "mid": v(-48.63, -18.8) * mm, "end": v(-48.64, -18.67) * mm});
            skArc(sketch, "E52.34.11", {"start": v(-50, -20.06) * mm, "mid": v(-50.06, -20.16) * mm, "end": v(-50.05, -20.28) * mm});
            skArc(sketch, "E52.34.12", {"start": v(-51.02, -17.68) * mm, "mid": v(-50.95, -17.78) * mm, "end": v(-50.84, -17.81) * mm});
            skArc(sketch, "E52.34.13", {"start": v(-51.1, -17.43) * mm, "mid": v(-51.07, -17.56) * mm, "end": v(-51.02, -17.68) * mm});
            skArc(sketch, "E52.34.14", {"start": v(-50.05, -20.28) * mm, "mid": v(-50, -20.4) * mm, "end": v(-49.95, -20.52) * mm});
            skLineSegment(sketch, "E52.34.15", {"start": v(-51.1, -17.43) * mm, "end": v(-51.02, -17.69) * mm});
            skLineSegment(sketch, "E52.35.0", {"start": v(-49.9, -21.94) * mm, "end": v(-49.95, -20.52) * mm});
            skPoint(sketch, "E52.35.1", {"position": v(-47.77, -20.79) * mm});
            skPoint(sketch, "E52.35.2", {"position": v(-49.8, -20.89) * mm});
            skArc(sketch, "E52.35.3", {"start": v(-47.72, -20.91) * mm, "mid": v(-47.57, -21.26) * mm, "end": v(-47.41, -21.6) * mm});
            skPoint(sketch, "E52.35.4", {"position": v(-48.78, -23.17) * mm});
            skPoint(sketch, "E52.35.5", {"position": v(-47.35, -21.73) * mm});
            skLineSegment(sketch, "E52.35.6", {"start": v(-47.91, -20.8) * mm, "end": v(-49.66, -20.88) * mm});
            skLineSegment(sketch, "E52.35.7", {"start": v(-48.6, -23.53) * mm, "end": v(-49.9, -21.94) * mm});
            skLineSegment(sketch, "E52.35.8", {"start": v(-48.68, -23.07) * mm, "end": v(-47.45, -21.83) * mm});
            skArc(sketch, "E52.35.9", {"start": v(-47.72, -20.91) * mm, "mid": v(-47.8, -20.82) * mm, "end": v(-47.91, -20.8) * mm});
            skArc(sketch, "E52.35.10", {"start": v(-47.45, -21.83) * mm, "mid": v(-47.4, -21.72) * mm, "end": v(-47.41, -21.6) * mm});
            skArc(sketch, "E52.35.11", {"start": v(-48.68, -23.07) * mm, "mid": v(-48.73, -23.18) * mm, "end": v(-48.72, -23.3) * mm});
            skArc(sketch, "E52.35.12", {"start": v(-49.85, -20.76) * mm, "mid": v(-49.77, -20.85) * mm, "end": v(-49.66, -20.88) * mm});
            skArc(sketch, "E52.35.13", {"start": v(-49.95, -20.52) * mm, "mid": v(-49.9, -20.64) * mm, "end": v(-49.85, -20.76) * mm});
            skArc(sketch, "E52.35.14", {"start": v(-48.72, -23.3) * mm, "mid": v(-48.66, -23.41) * mm, "end": v(-48.6, -23.53) * mm});
            skLineSegment(sketch, "E52.35.15", {"start": v(-49.95, -20.52) * mm, "end": v(-49.85, -20.77) * mm});
            skLineSegment(sketch, "E52.36.0", {"start": v(-48.47, -24.94) * mm, "end": v(-48.6, -23.52) * mm});
            skPoint(sketch, "E52.36.1", {"position": v(-46.42, -23.66) * mm});
            skPoint(sketch, "E52.36.2", {"position": v(-48.43, -23.88) * mm});
            skArc(sketch, "E52.36.3", {"start": v(-46.36, -23.78) * mm, "mid": v(-46.18, -24.12) * mm, "end": v(-46, -24.45) * mm});
            skPoint(sketch, "E52.36.4", {"position": v(-47.27, -26.1) * mm});
            skPoint(sketch, "E52.36.5", {"position": v(-45.94, -24.57) * mm});
            skLineSegment(sketch, "E52.36.6", {"start": v(-46.56, -23.68) * mm, "end": v(-48.3, -23.87) * mm});
            skLineSegment(sketch, "E52.36.7", {"start": v(-47.08, -26.45) * mm, "end": v(-48.47, -24.94) * mm});
            skLineSegment(sketch, "E52.36.8", {"start": v(-47.18, -26) * mm, "end": v(-46.03, -24.68) * mm});
            skArc(sketch, "E52.36.9", {"start": v(-46.36, -23.78) * mm, "mid": v(-46.44, -23.7) * mm, "end": v(-46.56, -23.68) * mm});
            skArc(sketch, "E52.36.10", {"start": v(-46.03, -24.68) * mm, "mid": v(-45.98, -24.57) * mm, "end": v(-46, -24.45) * mm});
            skArc(sketch, "E52.36.11", {"start": v(-47.18, -26) * mm, "mid": v(-47.23, -26.1) * mm, "end": v(-47.2, -26.22) * mm});
            skArc(sketch, "E52.36.12", {"start": v(-48.5, -23.76) * mm, "mid": v(-48.41, -23.84) * mm, "end": v(-48.3, -23.87) * mm});
            skArc(sketch, "E52.36.13", {"start": v(-48.6, -23.52) * mm, "mid": v(-48.55, -23.64) * mm, "end": v(-48.5, -23.76) * mm});
            skArc(sketch, "E52.36.14", {"start": v(-47.2, -26.22) * mm, "mid": v(-47.14, -26.34) * mm, "end": v(-47.08, -26.45) * mm});
            skLineSegment(sketch, "E52.36.15", {"start": v(-48.6, -23.52) * mm, "end": v(-48.49, -23.77) * mm});
            skLineSegment(sketch, "E52.37.0", {"start": v(-46.86, -27.85) * mm, "end": v(-47.08, -26.44) * mm});
            skPoint(sketch, "E52.37.1", {"position": v(-44.89, -26.45) * mm});
            skPoint(sketch, "E52.37.2", {"position": v(-46.89, -26.8) * mm});
            skArc(sketch, "E52.37.3", {"start": v(-44.82, -26.56) * mm, "mid": v(-44.62, -26.89) * mm, "end": v(-44.43, -27.21) * mm});
            skPoint(sketch, "E52.37.4", {"position": v(-45.6, -28.93) * mm});
            skPoint(sketch, "E52.37.5", {"position": v(-44.36, -27.33) * mm});
            skLineSegment(sketch, "E52.37.6", {"start": v(-45.03, -26.47) * mm, "end": v(-46.75, -26.77) * mm});
            skLineSegment(sketch, "E52.37.7", {"start": v(-45.38, -29.27) * mm, "end": v(-46.86, -27.85) * mm});
            skLineSegment(sketch, "E52.37.8", {"start": v(-45.5, -28.82) * mm, "end": v(-44.44, -27.44) * mm});
            skArc(sketch, "E52.37.9", {"start": v(-44.82, -26.56) * mm, "mid": v(-44.9, -26.48) * mm, "end": v(-45.03, -26.47) * mm});
            skArc(sketch, "E52.37.10", {"start": v(-44.44, -27.44) * mm, "mid": v(-44.4, -27.33) * mm, "end": v(-44.43, -27.21) * mm});
            skArc(sketch, "E52.37.11", {"start": v(-45.5, -28.82) * mm, "mid": v(-45.55, -28.94) * mm, "end": v(-45.52, -29.05) * mm});
            skArc(sketch, "E52.37.12", {"start": v(-46.95, -26.67) * mm, "mid": v(-46.87, -26.75) * mm, "end": v(-46.75, -26.77) * mm});
            skArc(sketch, "E52.37.13", {"start": v(-47.08, -26.44) * mm, "mid": v(-47.02, -26.56) * mm, "end": v(-46.95, -26.67) * mm});
            skArc(sketch, "E52.37.14", {"start": v(-45.52, -29.05) * mm, "mid": v(-45.45, -29.16) * mm, "end": v(-45.38, -29.27) * mm});
            skLineSegment(sketch, "E52.37.15", {"start": v(-47.08, -26.44) * mm, "end": v(-46.95, -26.68) * mm});
            skLineSegment(sketch, "E52.38.0", {"start": v(-45.08, -30.66) * mm, "end": v(-45.38, -29.26) * mm});
            skPoint(sketch, "E52.38.1", {"position": v(-43.2, -29.13) * mm});
            skPoint(sketch, "E52.38.2", {"position": v(-45.16, -29.6) * mm});
            skArc(sketch, "E52.38.3", {"start": v(-43.12, -29.25) * mm, "mid": v(-42.9, -29.56) * mm, "end": v(-42.69, -29.87) * mm});
            skPoint(sketch, "E52.38.4", {"position": v(-43.75, -31.66) * mm});
            skPoint(sketch, "E52.38.5", {"position": v(-42.6, -29.98) * mm});
            skLineSegment(sketch, "E52.38.6", {"start": v(-43.33, -29.17) * mm, "end": v(-45.03, -29.57) * mm});
            skLineSegment(sketch, "E52.38.7", {"start": v(-43.51, -31.98) * mm, "end": v(-45.08, -30.66) * mm});
            skLineSegment(sketch, "E52.38.8", {"start": v(-43.67, -31.54) * mm, "end": v(-42.69, -30.1) * mm});
            skArc(sketch, "E52.38.9", {"start": v(-43.12, -29.25) * mm, "mid": v(-43.2, -29.17) * mm, "end": v(-43.33, -29.17) * mm});
            skArc(sketch, "E52.38.10", {"start": v(-42.69, -30.1) * mm, "mid": v(-42.65, -29.98) * mm, "end": v(-42.69, -29.87) * mm});
            skArc(sketch, "E52.38.11", {"start": v(-43.67, -31.54) * mm, "mid": v(-43.7, -31.66) * mm, "end": v(-43.66, -31.77) * mm});
            skArc(sketch, "E52.38.12", {"start": v(-45.24, -29.48) * mm, "mid": v(-45.15, -29.56) * mm, "end": v(-45.03, -29.57) * mm});
            skArc(sketch, "E52.38.13", {"start": v(-45.38, -29.26) * mm, "mid": v(-45.31, -29.37) * mm, "end": v(-45.24, -29.48) * mm});
            skArc(sketch, "E52.38.14", {"start": v(-43.66, -31.77) * mm, "mid": v(-43.59, -31.88) * mm, "end": v(-43.51, -31.98) * mm});
            skLineSegment(sketch, "E52.38.15", {"start": v(-45.38, -29.26) * mm, "end": v(-45.24, -29.5) * mm});
            skLineSegment(sketch, "E52.39.0", {"start": v(-43.12, -33.35) * mm, "end": v(-43.51, -31.98) * mm});
            skPoint(sketch, "E52.39.1", {"position": v(-41.34, -31.71) * mm});
            skPoint(sketch, "E52.39.2", {"position": v(-43.28, -32.3) * mm});
            skArc(sketch, "E52.39.3", {"start": v(-41.25, -31.82) * mm, "mid": v(-41.02, -32.12) * mm, "end": v(-40.79, -32.42) * mm});
            skPoint(sketch, "E52.39.4", {"position": v(-41.73, -34.27) * mm});
            skPoint(sketch, "E52.39.5", {"position": v(-40.7, -32.52) * mm});
            skLineSegment(sketch, "E52.39.6", {"start": v(-41.47, -31.75) * mm, "end": v(-43.14, -32.26) * mm});
            skLineSegment(sketch, "E52.39.7", {"start": v(-41.48, -34.58) * mm, "end": v(-43.12, -33.35) * mm});
            skLineSegment(sketch, "E52.39.8", {"start": v(-41.66, -34.15) * mm, "end": v(-40.77, -32.64) * mm});
            skArc(sketch, "E52.39.9", {"start": v(-41.25, -31.82) * mm, "mid": v(-41.35, -31.75) * mm, "end": v(-41.47, -31.75) * mm});
            skArc(sketch, "E52.39.10", {"start": v(-40.77, -32.64) * mm, "mid": v(-40.74, -32.53) * mm, "end": v(-40.79, -32.42) * mm});
            skArc(sketch, "E52.39.11", {"start": v(-41.66, -34.15) * mm, "mid": v(-41.7, -34.26) * mm, "end": v(-41.65, -34.38) * mm});
            skArc(sketch, "E52.39.12", {"start": v(-43.36, -32.19) * mm, "mid": v(-43.26, -32.26) * mm, "end": v(-43.14, -32.26) * mm});
            skArc(sketch, "E52.39.13", {"start": v(-43.51, -31.98) * mm, "mid": v(-43.44, -32.08) * mm, "end": v(-43.36, -32.19) * mm});
            skArc(sketch, "E52.39.14", {"start": v(-41.65, -34.38) * mm, "mid": v(-41.56, -34.48) * mm, "end": v(-41.48, -34.58) * mm});
            skLineSegment(sketch, "E52.39.15", {"start": v(-43.51, -31.98) * mm, "end": v(-43.35, -32.2) * mm});
            skLineSegment(sketch, "E52.40.0", {"start": v(-41, -35.91) * mm, "end": v(-41.48, -34.57) * mm});
            skPoint(sketch, "E52.40.1", {"position": v(-39.33, -34.17) * mm});
            skPoint(sketch, "E52.40.2", {"position": v(-41.23, -34.88) * mm});
            skArc(sketch, "E52.40.3", {"start": v(-39.24, -34.28) * mm, "mid": v(-38.99, -34.56) * mm, "end": v(-38.73, -34.84) * mm});
            skPoint(sketch, "E52.40.4", {"position": v(-39.57, -36.75) * mm});
            skPoint(sketch, "E52.40.5", {"position": v(-38.64, -34.95) * mm});
            skLineSegment(sketch, "E52.40.6", {"start": v(-39.46, -34.22) * mm, "end": v(-41.1, -34.83) * mm});
            skLineSegment(sketch, "E52.40.7", {"start": v(-39.3, -37.04) * mm, "end": v(-41, -35.91) * mm});
            skLineSegment(sketch, "E52.40.8", {"start": v(-39.5, -36.62) * mm, "end": v(-38.7, -35.07) * mm});
            skArc(sketch, "E52.40.9", {"start": v(-39.24, -34.28) * mm, "mid": v(-39.34, -34.22) * mm, "end": v(-39.46, -34.22) * mm});
            skArc(sketch, "E52.40.10", {"start": v(-38.7, -35.07) * mm, "mid": v(-38.68, -34.95) * mm, "end": v(-38.73, -34.84) * mm});
            skArc(sketch, "E52.40.11", {"start": v(-39.5, -36.62) * mm, "mid": v(-39.52, -36.74) * mm, "end": v(-39.47, -36.85) * mm});
            skArc(sketch, "E52.40.12", {"start": v(-41.32, -34.77) * mm, "mid": v(-41.22, -34.83) * mm, "end": v(-41.1, -34.83) * mm});
            skArc(sketch, "E52.40.13", {"start": v(-41.48, -34.57) * mm, "mid": v(-41.4, -34.67) * mm, "end": v(-41.32, -34.77) * mm});
            skArc(sketch, "E52.40.14", {"start": v(-39.47, -36.85) * mm, "mid": v(-39.38, -36.95) * mm, "end": v(-39.3, -37.04) * mm});
            skLineSegment(sketch, "E52.40.15", {"start": v(-41.48, -34.57) * mm, "end": v(-41.3, -34.78) * mm});
            skLineSegment(sketch, "E52.41.0", {"start": v(-38.74, -38.35) * mm, "end": v(-39.3, -37.03) * mm});
            skPoint(sketch, "E52.41.1", {"position": v(-37.17, -36.5) * mm});
            skPoint(sketch, "E52.41.2", {"position": v(-39.02, -37.32) * mm});
            skArc(sketch, "E52.41.3", {"start": v(-37.07, -36.6) * mm, "mid": v(-36.8, -36.87) * mm, "end": v(-36.54, -37.14) * mm});
            skPoint(sketch, "E52.41.4", {"position": v(-37.25, -39.1) * mm});
            skPoint(sketch, "E52.41.5", {"position": v(-36.44, -37.24) * mm});
            skLineSegment(sketch, "E52.41.6", {"start": v(-37.3, -36.56) * mm, "end": v(-38.9, -37.27) * mm});
            skLineSegment(sketch, "E52.41.7", {"start": v(-36.96, -39.37) * mm, "end": v(-38.74, -38.35) * mm});
            skLineSegment(sketch, "E52.41.8", {"start": v(-37.2, -38.96) * mm, "end": v(-36.5, -37.36) * mm});
            skArc(sketch, "E52.41.9", {"start": v(-37.07, -36.6) * mm, "mid": v(-37.18, -36.55) * mm, "end": v(-37.3, -36.56) * mm});
            skArc(sketch, "E52.41.10", {"start": v(-36.5, -37.36) * mm, "mid": v(-36.48, -37.24) * mm, "end": v(-36.54, -37.14) * mm});
            skArc(sketch, "E52.41.11", {"start": v(-37.2, -38.96) * mm, "mid": v(-37.21, -39.08) * mm, "end": v(-37.15, -39.19) * mm});
            skArc(sketch, "E52.41.12", {"start": v(-39.12, -37.22) * mm, "mid": v(-39.02, -37.28) * mm, "end": v(-38.9, -37.27) * mm});
            skArc(sketch, "E52.41.13", {"start": v(-39.3, -37.03) * mm, "mid": v(-39.21, -37.13) * mm, "end": v(-39.12, -37.22) * mm});
            skArc(sketch, "E52.41.14", {"start": v(-37.15, -39.19) * mm, "mid": v(-37.06, -39.28) * mm, "end": v(-36.96, -39.37) * mm});
            skLineSegment(sketch, "E52.41.15", {"start": v(-39.3, -37.03) * mm, "end": v(-39.11, -37.23) * mm});
            skLineSegment(sketch, "E52.42.0", {"start": v(-36.33, -40.64) * mm, "end": v(-36.97, -39.36) * mm});
            skPoint(sketch, "E52.42.1", {"position": v(-34.88, -38.7) * mm});
            skPoint(sketch, "E52.42.2", {"position": v(-36.68, -39.63) * mm});
            skArc(sketch, "E52.42.3", {"start": v(-34.77, -38.8) * mm, "mid": v(-34.5, -39.05) * mm, "end": v(-34.2, -39.3) * mm});
            skPoint(sketch, "E52.42.4", {"position": v(-34.8, -41.29) * mm});
            skPoint(sketch, "E52.42.5", {"position": v(-34.1, -39.39) * mm});
            skLineSegment(sketch, "E52.42.6", {"start": v(-35, -38.77) * mm, "end": v(-36.55, -39.57) * mm});
            skLineSegment(sketch, "E52.42.7", {"start": v(-34.5, -41.55) * mm, "end": v(-36.33, -40.64) * mm});
            skLineSegment(sketch, "E52.42.8", {"start": v(-34.75, -41.16) * mm, "end": v(-34.15, -39.52) * mm});
            skArc(sketch, "E52.42.9", {"start": v(-34.77, -38.8) * mm, "mid": v(-34.88, -38.75) * mm, "end": v(-35, -38.77) * mm});
            skArc(sketch, "E52.42.10", {"start": v(-34.15, -39.52) * mm, "mid": v(-34.14, -39.4) * mm, "end": v(-34.2, -39.3) * mm});
            skArc(sketch, "E52.42.11", {"start": v(-34.75, -41.16) * mm, "mid": v(-34.76, -41.28) * mm, "end": v(-34.7, -41.38) * mm});
            skArc(sketch, "E52.42.12", {"start": v(-36.78, -39.54) * mm, "mid": v(-36.67, -39.6) * mm, "end": v(-36.55, -39.57) * mm});
            skArc(sketch, "E52.42.13", {"start": v(-36.97, -39.36) * mm, "mid": v(-36.87, -39.45) * mm, "end": v(-36.78, -39.54) * mm});
            skArc(sketch, "E52.42.14", {"start": v(-34.7, -41.38) * mm, "mid": v(-34.6, -41.46) * mm, "end": v(-34.5, -41.55) * mm});
            skLineSegment(sketch, "E52.42.15", {"start": v(-36.97, -39.36) * mm, "end": v(-36.77, -39.55) * mm});
            skLineSegment(sketch, "E52.43.0", {"start": v(-33.79, -42.78) * mm, "end": v(-34.5, -41.54) * mm});
            skPoint(sketch, "E52.43.1", {"position": v(-32.45, -40.76) * mm});
            skPoint(sketch, "E52.43.2", {"position": v(-34.2, -41.8) * mm});
            skArc(sketch, "E52.43.3", {"start": v(-32.34, -40.85) * mm, "mid": v(-32.05, -41.08) * mm, "end": v(-31.75, -41.31) * mm});
            skPoint(sketch, "E52.43.4", {"position": v(-32.22, -43.33) * mm});
            skPoint(sketch, "E52.43.5", {"position": v(-31.64, -41.4) * mm});
            skLineSegment(sketch, "E52.43.6", {"start": v(-32.57, -40.83) * mm, "end": v(-34.07, -41.72) * mm});
            skLineSegment(sketch, "E52.43.7", {"start": v(-31.9, -43.57) * mm, "end": v(-33.79, -42.78) * mm});
            skLineSegment(sketch, "E52.43.8", {"start": v(-32.18, -43.2) * mm, "end": v(-31.68, -41.53) * mm});
            skArc(sketch, "E52.43.9", {"start": v(-32.34, -40.85) * mm, "mid": v(-32.45, -40.8) * mm, "end": v(-32.57, -40.83) * mm});
            skArc(sketch, "E52.43.10", {"start": v(-31.68, -41.53) * mm, "mid": v(-31.68, -41.4) * mm, "end": v(-31.75, -41.31) * mm});
            skArc(sketch, "E52.43.11", {"start": v(-32.18, -43.2) * mm, "mid": v(-32.18, -43.32) * mm, "end": v(-32.1, -43.42) * mm});
            skArc(sketch, "E52.43.12", {"start": v(-34.3, -41.7) * mm, "mid": v(-34.19, -41.75) * mm, "end": v(-34.07, -41.72) * mm});
            skArc(sketch, "E52.43.13", {"start": v(-34.5, -41.54) * mm, "mid": v(-34.4, -41.63) * mm, "end": v(-34.3, -41.7) * mm});
            skArc(sketch, "E52.43.14", {"start": v(-32.1, -43.42) * mm, "mid": v(-32, -43.5) * mm, "end": v(-31.9, -43.57) * mm});
            skLineSegment(sketch, "E52.43.15", {"start": v(-34.5, -41.54) * mm, "end": v(-34.3, -41.71) * mm});
            skLineSegment(sketch, "E52.44.0", {"start": v(-31.12, -44.76) * mm, "end": v(-31.9, -43.57) * mm});
            skPoint(sketch, "E52.44.1", {"position": v(-29.9, -42.66) * mm});
            skPoint(sketch, "E52.44.2", {"position": v(-31.58, -43.8) * mm});
            skArc(sketch, "E52.44.3", {"start": v(-29.8, -42.74) * mm, "mid": v(-29.48, -42.96) * mm, "end": v(-29.17, -43.17) * mm});
            skPoint(sketch, "E52.44.4", {"position": v(-29.52, -45.22) * mm});
            skPoint(sketch, "E52.44.5", {"position": v(-29.05, -43.25) * mm});
            skLineSegment(sketch, "E52.44.6", {"start": v(-30.02, -42.74) * mm, "end": v(-31.46, -43.72) * mm});
            skLineSegment(sketch, "E52.44.7", {"start": v(-29.18, -45.44) * mm, "end": v(-31.12, -44.76) * mm});
            skLineSegment(sketch, "E52.44.8", {"start": v(-29.49, -45.08) * mm, "end": v(-29.09, -43.38) * mm});
            skArc(sketch, "E52.44.9", {"start": v(-29.8, -42.74) * mm, "mid": v(-29.9, -42.7) * mm, "end": v(-30.02, -42.74) * mm});
            skArc(sketch, "E52.44.10", {"start": v(-29.09, -43.38) * mm, "mid": v(-29.1, -43.26) * mm, "end": v(-29.17, -43.17) * mm});
            skArc(sketch, "E52.44.11", {"start": v(-29.49, -45.08) * mm, "mid": v(-29.48, -45.2) * mm, "end": v(-29.4, -45.3) * mm});
            skArc(sketch, "E52.44.12", {"start": v(-31.7, -43.72) * mm, "mid": v(-31.58, -43.76) * mm, "end": v(-31.46, -43.72) * mm});
            skArc(sketch, "E52.44.13", {"start": v(-31.9, -43.57) * mm, "mid": v(-31.8, -43.64) * mm, "end": v(-31.7, -43.72) * mm});
            skArc(sketch, "E52.44.14", {"start": v(-29.4, -45.3) * mm, "mid": v(-29.3, -45.37) * mm, "end": v(-29.18, -45.44) * mm});
            skLineSegment(sketch, "E52.44.15", {"start": v(-31.9, -43.57) * mm, "end": v(-31.68, -43.73) * mm});
            skLineSegment(sketch, "E52.45.0", {"start": v(-28.33, -46.57) * mm, "end": v(-29.19, -45.43) * mm});
            skPoint(sketch, "E52.45.1", {"position": v(-27.25, -44.4) * mm});
            skPoint(sketch, "E52.45.2", {"position": v(-28.85, -45.65) * mm});
            skArc(sketch, "E52.45.3", {"start": v(-27.13, -44.48) * mm, "mid": v(-26.8, -44.67) * mm, "end": v(-26.48, -44.87) * mm});
            skPoint(sketch, "E52.45.4", {"position": v(-26.7, -46.93) * mm});
            skPoint(sketch, "E52.45.5", {"position": v(-26.36, -44.94) * mm});
            skLineSegment(sketch, "E52.45.6", {"start": v(-27.36, -44.5) * mm, "end": v(-28.74, -45.56) * mm});
            skLineSegment(sketch, "E52.45.7", {"start": v(-26.36, -47.13) * mm, "end": v(-28.33, -46.57) * mm});
            skLineSegment(sketch, "E52.45.8", {"start": v(-26.68, -46.8) * mm, "end": v(-26.39, -45.07) * mm});
            skArc(sketch, "E52.45.9", {"start": v(-27.13, -44.48) * mm, "mid": v(-27.25, -44.45) * mm, "end": v(-27.36, -44.5) * mm});
            skArc(sketch, "E52.45.10", {"start": v(-26.39, -45.07) * mm, "mid": v(-26.4, -44.96) * mm, "end": v(-26.48, -44.87) * mm});
            skArc(sketch, "E52.45.11", {"start": v(-26.68, -46.8) * mm, "mid": v(-26.67, -46.91) * mm, "end": v(-26.58, -47) * mm});
            skArc(sketch, "E52.45.12", {"start": v(-28.97, -45.57) * mm, "mid": v(-28.85, -45.6) * mm, "end": v(-28.74, -45.56) * mm});
            skArc(sketch, "E52.45.13", {"start": v(-29.19, -45.43) * mm, "mid": v(-29.08, -45.5) * mm, "end": v(-28.97, -45.57) * mm});
            skArc(sketch, "E52.45.14", {"start": v(-26.58, -47) * mm, "mid": v(-26.47, -47.07) * mm, "end": v(-26.36, -47.13) * mm});
            skLineSegment(sketch, "E52.45.15", {"start": v(-29.19, -45.43) * mm, "end": v(-28.96, -45.58) * mm});
            skLineSegment(sketch, "E52.46.0", {"start": v(-25.44, -48.21) * mm, "end": v(-26.36, -47.13) * mm});
            skPoint(sketch, "E52.46.1", {"position": v(-24.5, -45.98) * mm});
            skPoint(sketch, "E52.46.2", {"position": v(-26.01, -47.32) * mm});
            skArc(sketch, "E52.46.3", {"start": v(-24.37, -46.05) * mm, "mid": v(-24.03, -46.22) * mm, "end": v(-23.7, -46.4) * mm});
            skPoint(sketch, "E52.46.4", {"position": v(-23.8, -48.47) * mm});
            skPoint(sketch, "E52.46.5", {"position": v(-23.58, -46.46) * mm});
            skLineSegment(sketch, "E52.46.6", {"start": v(-24.6, -46.08) * mm, "end": v(-25.9, -47.23) * mm});
            skLineSegment(sketch, "E52.46.7", {"start": v(-23.44, -48.65) * mm, "end": v(-25.44, -48.21) * mm});
            skLineSegment(sketch, "E52.46.8", {"start": v(-23.78, -48.33) * mm, "end": v(-23.6, -46.6) * mm});
            skArc(sketch, "E52.46.9", {"start": v(-24.37, -46.05) * mm, "mid": v(-24.49, -46.03) * mm, "end": v(-24.6, -46.08) * mm});
            skArc(sketch, "E52.46.10", {"start": v(-23.6, -46.6) * mm, "mid": v(-23.61, -46.48) * mm, "end": v(-23.7, -46.4) * mm});
            skArc(sketch, "E52.46.11", {"start": v(-23.78, -48.33) * mm, "mid": v(-23.76, -48.45) * mm, "end": v(-23.67, -48.54) * mm});
            skArc(sketch, "E52.46.12", {"start": v(-26.14, -47.25) * mm, "mid": v(-26.02, -47.28) * mm, "end": v(-25.9, -47.23) * mm});
            skArc(sketch, "E52.46.13", {"start": v(-26.36, -47.13) * mm, "mid": v(-26.25, -47.2) * mm, "end": v(-26.14, -47.25) * mm});
            skArc(sketch, "E52.46.14", {"start": v(-23.67, -48.54) * mm, "mid": v(-23.55, -48.6) * mm, "end": v(-23.44, -48.65) * mm});
            skLineSegment(sketch, "E52.46.15", {"start": v(-26.36, -47.13) * mm, "end": v(-26.13, -47.26) * mm});
            skLineSegment(sketch, "E52.47.0", {"start": v(-22.45, -49.67) * mm, "end": v(-23.44, -48.65) * mm});
            skPoint(sketch, "E52.47.1", {"position": v(-21.64, -47.4) * mm});
            skPoint(sketch, "E52.47.2", {"position": v(-23.08, -48.82) * mm});
            skArc(sketch, "E52.47.3", {"start": v(-21.52, -47.45) * mm, "mid": v(-21.17, -47.6) * mm, "end": v(-20.83, -47.76) * mm});
            skPoint(sketch, "E52.47.4", {"position": v(-20.8, -49.83) * mm});
            skPoint(sketch, "E52.47.5", {"position": v(-20.7, -47.81) * mm});
            skLineSegment(sketch, "E52.47.6", {"start": v(-21.74, -47.49) * mm, "end": v(-22.98, -48.72) * mm});
            skLineSegment(sketch, "E52.47.7", {"start": v(-20.43, -49.99) * mm, "end": v(-22.45, -49.67) * mm});
            skLineSegment(sketch, "E52.47.8", {"start": v(-20.79, -49.7) * mm, "end": v(-20.7, -47.95) * mm});
            skArc(sketch, "E52.47.9", {"start": v(-21.52, -47.45) * mm, "mid": v(-21.63, -47.43) * mm, "end": v(-21.74, -47.49) * mm});
            skArc(sketch, "E52.47.10", {"start": v(-20.7, -47.95) * mm, "mid": v(-20.74, -47.83) * mm, "end": v(-20.83, -47.76) * mm});
            skArc(sketch, "E52.47.11", {"start": v(-20.79, -49.7) * mm, "mid": v(-20.76, -49.81) * mm, "end": v(-20.67, -49.89) * mm});
            skArc(sketch, "E52.47.12", {"start": v(-23.2, -48.76) * mm, "mid": v(-23.09, -48.78) * mm, "end": v(-22.98, -48.72) * mm});
            skArc(sketch, "E52.47.13", {"start": v(-23.44, -48.65) * mm, "mid": v(-23.32, -48.7) * mm, "end": v(-23.2, -48.76) * mm});
            skArc(sketch, "E52.47.14", {"start": v(-20.67, -49.89) * mm, "mid": v(-20.55, -49.94) * mm, "end": v(-20.43, -49.99) * mm});
            skLineSegment(sketch, "E52.47.15", {"start": v(-23.44, -48.65) * mm, "end": v(-23.2, -48.76) * mm});
            skLineSegment(sketch, "E52.48.0", {"start": v(-19.38, -50.95) * mm, "end": v(-20.43, -49.99) * mm});
            skPoint(sketch, "E52.48.1", {"position": v(-18.71, -48.62) * mm});
            skPoint(sketch, "E52.48.2", {"position": v(-20.06, -50.14) * mm});
            skArc(sketch, "E52.48.3", {"start": v(-18.58, -48.67) * mm, "mid": v(-18.23, -48.8) * mm, "end": v(-17.88, -48.94) * mm});
            skPoint(sketch, "E52.48.4", {"position": v(-17.72, -51.01) * mm});
            skPoint(sketch, "E52.48.5", {"position": v(-17.75, -48.98) * mm});
            skLineSegment(sketch, "E52.48.6", {"start": v(-18.8, -48.73) * mm, "end": v(-19.97, -50.03) * mm});
            skLineSegment(sketch, "E52.48.7", {"start": v(-17.34, -51.14) * mm, "end": v(-19.38, -50.95) * mm});
            skLineSegment(sketch, "E52.48.8", {"start": v(-17.72, -50.87) * mm, "end": v(-17.74, -49.12) * mm});
            skArc(sketch, "E52.48.9", {"start": v(-18.58, -48.67) * mm, "mid": v(-18.7, -48.67) * mm, "end": v(-18.8, -48.73) * mm});
            skArc(sketch, "E52.48.10", {"start": v(-17.74, -49.12) * mm, "mid": v(-17.78, -49) * mm, "end": v(-17.88, -48.94) * mm});
            skArc(sketch, "E52.48.11", {"start": v(-17.72, -50.87) * mm, "mid": v(-17.68, -50.98) * mm, "end": v(-17.59, -51.06) * mm});
            skArc(sketch, "E52.48.12", {"start": v(-20.2, -50.08) * mm, "mid": v(-20.07, -50.1) * mm, "end": v(-19.97, -50.03) * mm});
            skArc(sketch, "E52.48.13", {"start": v(-20.43, -49.99) * mm, "mid": v(-20.31, -50.03) * mm, "end": v(-20.2, -50.08) * mm});
            skArc(sketch, "E52.48.14", {"start": v(-17.59, -51.06) * mm, "mid": v(-17.46, -51.1) * mm, "end": v(-17.34, -51.14) * mm});
            skLineSegment(sketch, "E52.48.15", {"start": v(-20.43, -49.99) * mm, "end": v(-20.18, -50.09) * mm});
            skLineSegment(sketch, "E52.49.0", {"start": v(-16.24, -52.04) * mm, "end": v(-17.35, -51.14) * mm});
            skPoint(sketch, "E52.49.1", {"position": v(-15.71, -49.67) * mm});
            skPoint(sketch, "E52.49.2", {"position": v(-16.97, -51.26) * mm});
            skArc(sketch, "E52.49.3", {"start": v(-15.58, -49.72) * mm, "mid": v(-15.22, -49.83) * mm, "end": v(-14.86, -49.94) * mm});
            skPoint(sketch, "E52.49.4", {"position": v(-14.58, -52) * mm});
            skPoint(sketch, "E52.49.5", {"position": v(-14.73, -49.98) * mm});
            skLineSegment(sketch, "E52.49.6", {"start": v(-15.8, -49.78) * mm, "end": v(-16.88, -51.15) * mm});
            skLineSegment(sketch, "E52.49.7", {"start": v(-14.2, -52.1) * mm, "end": v(-16.24, -52.04) * mm});
            skLineSegment(sketch, "E52.49.8", {"start": v(-14.59, -51.86) * mm, "end": v(-14.72, -50.11) * mm});
            skArc(sketch, "E52.49.9", {"start": v(-15.58, -49.72) * mm, "mid": v(-15.7, -49.71) * mm, "end": v(-15.8, -49.78) * mm});
            skArc(sketch, "E52.49.10", {"start": v(-14.72, -50.11) * mm, "mid": v(-14.76, -50) * mm, "end": v(-14.86, -49.94) * mm});
            skArc(sketch, "E52.49.11", {"start": v(-14.59, -51.86) * mm, "mid": v(-14.54, -51.97) * mm, "end": v(-14.44, -52.03) * mm});
            skArc(sketch, "E52.49.12", {"start": v(-17.1, -51.22) * mm, "mid": v(-16.98, -51.22) * mm, "end": v(-16.88, -51.15) * mm});
            skArc(sketch, "E52.49.13", {"start": v(-17.35, -51.14) * mm, "mid": v(-17.22, -51.18) * mm, "end": v(-17.1, -51.22) * mm});
            skArc(sketch, "E52.49.14", {"start": v(-14.44, -52.03) * mm, "mid": v(-14.32, -52.07) * mm, "end": v(-14.2, -52.1) * mm});
            skLineSegment(sketch, "E52.49.15", {"start": v(-17.35, -51.14) * mm, "end": v(-17.1, -51.22) * mm});
            skLineSegment(sketch, "E52.50.0", {"start": v(-13.04, -52.93) * mm, "end": v(-14.2, -52.1) * mm});
            skPoint(sketch, "E52.50.1", {"position": v(-12.66, -50.54) * mm});
            skPoint(sketch, "E52.50.2", {"position": v(-13.81, -52.2) * mm});
            skArc(sketch, "E52.50.3", {"start": v(-12.52, -50.57) * mm, "mid": v(-12.16, -50.66) * mm, "end": v(-11.79, -50.75) * mm});
            skPoint(sketch, "E52.50.4", {"position": v(-11.38, -52.79) * mm});
            skPoint(sketch, "E52.50.5", {"position": v(-11.65, -50.78) * mm});
            skLineSegment(sketch, "E52.50.6", {"start": v(-12.73, -50.65) * mm, "end": v(-13.73, -52.09) * mm});
            skLineSegment(sketch, "E52.50.7", {"start": v(-10.99, -52.87) * mm, "end": v(-13.04, -52.93) * mm});
            skLineSegment(sketch, "E52.50.8", {"start": v(-11.4, -52.65) * mm, "end": v(-11.63, -50.92) * mm});
            skArc(sketch, "E52.50.9", {"start": v(-12.52, -50.57) * mm, "mid": v(-12.64, -50.58) * mm, "end": v(-12.73, -50.65) * mm});
            skArc(sketch, "E52.50.10", {"start": v(-11.63, -50.92) * mm, "mid": v(-11.68, -50.8) * mm, "end": v(-11.79, -50.75) * mm});
            skArc(sketch, "E52.50.11", {"start": v(-11.4, -52.65) * mm, "mid": v(-11.35, -52.76) * mm, "end": v(-11.24, -52.82) * mm});
            skArc(sketch, "E52.50.12", {"start": v(-13.95, -52.17) * mm, "mid": v(-13.83, -52.16) * mm, "end": v(-13.73, -52.09) * mm});
            skArc(sketch, "E52.50.13", {"start": v(-14.2, -52.1) * mm, "mid": v(-14.07, -52.13) * mm, "end": v(-13.95, -52.17) * mm});
            skArc(sketch, "E52.50.14", {"start": v(-11.24, -52.82) * mm, "mid": v(-11.12, -52.84) * mm, "end": v(-10.99, -52.87) * mm});
            skLineSegment(sketch, "E52.50.15", {"start": v(-14.2, -52.1) * mm, "end": v(-13.94, -52.17) * mm});
            skLineSegment(sketch, "E52.51.0", {"start": v(-9.79, -53.63) * mm, "end": v(-11, -52.87) * mm});
            skPoint(sketch, "E52.51.1", {"position": v(-9.55, -51.22) * mm});
            skPoint(sketch, "E52.51.2", {"position": v(-10.6, -52.95) * mm});
            skArc(sketch, "E52.51.3", {"start": v(-9.42, -51.24) * mm, "mid": v(-9.04, -51.3) * mm, "end": v(-8.67, -51.37) * mm});
            skPoint(sketch, "E52.51.4", {"position": v(-8.14, -53.38) * mm});
            skPoint(sketch, "E52.51.5", {"position": v(-8.54, -51.4) * mm});
            skLineSegment(sketch, "E52.51.6", {"start": v(-9.62, -51.33) * mm, "end": v(-10.53, -52.83) * mm});
            skLineSegment(sketch, "E52.51.7", {"start": v(-7.74, -53.44) * mm, "end": v(-9.79, -53.63) * mm});
            skLineSegment(sketch, "E52.51.8", {"start": v(-8.17, -53.25) * mm, "end": v(-8.5, -51.53) * mm});
            skArc(sketch, "E52.51.9", {"start": v(-9.42, -51.24) * mm, "mid": v(-9.53, -51.26) * mm, "end": v(-9.62, -51.33) * mm});
            skArc(sketch, "E52.51.10", {"start": v(-8.5, -51.53) * mm, "mid": v(-8.57, -51.43) * mm, "end": v(-8.67, -51.37) * mm});
            skArc(sketch, "E52.51.11", {"start": v(-8.17, -53.25) * mm, "mid": v(-8.1, -53.35) * mm, "end": v(-8, -53.4) * mm});
            skArc(sketch, "E52.51.12", {"start": v(-10.74, -52.92) * mm, "mid": v(-10.62, -52.9) * mm, "end": v(-10.53, -52.83) * mm});
            skArc(sketch, "E52.51.13", {"start": v(-11, -52.87) * mm, "mid": v(-10.87, -52.9) * mm, "end": v(-10.74, -52.92) * mm});
            skArc(sketch, "E52.51.14", {"start": v(-8, -53.4) * mm, "mid": v(-7.87, -53.42) * mm, "end": v(-7.74, -53.44) * mm});
            skLineSegment(sketch, "E52.51.15", {"start": v(-11, -52.87) * mm, "end": v(-10.73, -52.92) * mm});
            skLineSegment(sketch, "E52.52.0", {"start": v(-6.5, -54.12) * mm, "end": v(-7.75, -53.44) * mm});
            skPoint(sketch, "E52.52.1", {"position": v(-6.41, -51.7) * mm});
            skPoint(sketch, "E52.52.2", {"position": v(-7.35, -53.5) * mm});
            skArc(sketch, "E52.52.3", {"start": v(-6.27, -51.72) * mm, "mid": v(-5.9, -51.76) * mm, "end": v(-5.52, -51.8) * mm});
            skPoint(sketch, "E52.52.4", {"position": v(-4.87, -53.78) * mm});
            skPoint(sketch, "E52.52.5", {"position": v(-5.39, -51.82) * mm});
            skLineSegment(sketch, "E52.52.6", {"start": v(-6.48, -51.83) * mm, "end": v(-7.29, -53.37) * mm});
            skLineSegment(sketch, "E52.52.7", {"start": v(-4.47, -53.81) * mm, "end": v(-6.5, -54.12) * mm});
            skLineSegment(sketch, "E52.52.8", {"start": v(-4.9, -53.64) * mm, "end": v(-5.35, -51.95) * mm});
            skArc(sketch, "E52.52.9", {"start": v(-6.27, -51.72) * mm, "mid": v(-6.4, -51.74) * mm, "end": v(-6.48, -51.83) * mm});
            skArc(sketch, "E52.52.10", {"start": v(-5.35, -51.95) * mm, "mid": v(-5.41, -51.85) * mm, "end": v(-5.52, -51.8) * mm});
            skArc(sketch, "E52.52.11", {"start": v(-4.9, -53.64) * mm, "mid": v(-4.84, -53.75) * mm, "end": v(-4.73, -53.8) * mm});
            skArc(sketch, "E52.52.12", {"start": v(-7.5, -53.48) * mm, "mid": v(-7.38, -53.46) * mm, "end": v(-7.29, -53.37) * mm});
            skArc(sketch, "E52.52.13", {"start": v(-7.75, -53.44) * mm, "mid": v(-7.62, -53.46) * mm, "end": v(-7.5, -53.48) * mm});
            skArc(sketch, "E52.52.14", {"start": v(-4.73, -53.8) * mm, "mid": v(-4.6, -53.8) * mm, "end": v(-4.47, -53.81) * mm});
            skLineSegment(sketch, "E52.52.15", {"start": v(-7.75, -53.44) * mm, "end": v(-7.48, -53.48) * mm});
            skLineSegment(sketch, "E52.53.0", {"start": v(-3.19, -54.42) * mm, "end": v(-4.48, -53.81) * mm});
            skPoint(sketch, "E52.53.1", {"position": v(-3.25, -52) * mm});
            skPoint(sketch, "E52.53.2", {"position": v(-4.08, -53.85) * mm});
            skArc(sketch, "E52.53.3", {"start": v(-3.1, -52) * mm, "mid": v(-2.73, -52.03) * mm, "end": v(-2.35, -52.05) * mm});
            skPoint(sketch, "E52.53.4", {"position": v(-1.58, -53.98) * mm});
            skPoint(sketch, "E52.53.5", {"position": v(-2.22, -52.05) * mm});
            skLineSegment(sketch, "E52.53.6", {"start": v(-3.3, -52.12) * mm, "end": v(-4.02, -53.72) * mm});
            skLineSegment(sketch, "E52.53.7", {"start": v(-1.18, -53.99) * mm, "end": v(-3.19, -54.42) * mm});
            skLineSegment(sketch, "E52.53.8", {"start": v(-1.63, -53.84) * mm, "end": v(-2.17, -52.18) * mm});
            skArc(sketch, "E52.53.9", {"start": v(-3.1, -52) * mm, "mid": v(-3.23, -52.04) * mm, "end": v(-3.3, -52.12) * mm});
            skArc(sketch, "E52.53.10", {"start": v(-2.17, -52.18) * mm, "mid": v(-2.24, -52.09) * mm, "end": v(-2.35, -52.05) * mm});
            skArc(sketch, "E52.53.11", {"start": v(-1.63, -53.84) * mm, "mid": v(-1.56, -53.94) * mm, "end": v(-1.44, -53.98) * mm});
            skArc(sketch, "E52.53.12", {"start": v(-4.22, -53.83) * mm, "mid": v(-4.1, -53.8) * mm, "end": v(-4.02, -53.72) * mm});
            skArc(sketch, "E52.53.13", {"start": v(-4.48, -53.81) * mm, "mid": v(-4.35, -53.82) * mm, "end": v(-4.22, -53.83) * mm});
            skArc(sketch, "E52.53.14", {"start": v(-1.44, -53.98) * mm, "mid": v(-1.31, -53.98) * mm, "end": v(-1.18, -53.99) * mm});
            skLineSegment(sketch, "E52.53.15", {"start": v(-4.48, -53.81) * mm, "end": v(-4.2, -53.84) * mm});
            skLineSegment(sketch, "E52.54.0", {"start": v(0.14, -54.51) * mm, "end": v(-1.19, -53.99) * mm});
            skPoint(sketch, "E52.54.1", {"position": v(-0.07, -52.1) * mm});
            skPoint(sketch, "E52.54.2", {"position": v(-0.79, -54) * mm});
            skArc(sketch, "E52.54.3", {"start": v(0.07, -52.1) * mm, "mid": v(0.44, -52.1) * mm, "end": v(0.82, -52.1) * mm});
            skPoint(sketch, "E52.54.4", {"position": v(1.71, -53.97) * mm});
            skPoint(sketch, "E52.54.5", {"position": v(0.96, -52.1) * mm});
            skLineSegment(sketch, "E52.54.6", {"start": v(-0.12, -52.23) * mm, "end": v(-0.74, -53.86) * mm});
            skLineSegment(sketch, "E52.54.7", {"start": v(2.11, -53.96) * mm, "end": v(0.14, -54.51) * mm});
            skLineSegment(sketch, "E52.54.8", {"start": v(1.66, -53.84) * mm, "end": v(1.01, -52.22) * mm});
            skArc(sketch, "E52.54.9", {"start": v(0.07, -52.1) * mm, "mid": v(-0.05, -52.14) * mm, "end": v(-0.12, -52.23) * mm});
            skArc(sketch, "E52.54.10", {"start": v(1.01, -52.22) * mm, "mid": v(0.94, -52.13) * mm, "end": v(0.82, -52.1) * mm});
            skArc(sketch, "E52.54.11", {"start": v(1.66, -53.84) * mm, "mid": v(1.74, -53.94) * mm, "end": v(1.85, -53.97) * mm});
            skArc(sketch, "E52.54.12", {"start": v(-0.93, -54) * mm, "mid": v(-0.81, -53.96) * mm, "end": v(-0.74, -53.86) * mm});
            skArc(sketch, "E52.54.13", {"start": v(-1.19, -53.99) * mm, "mid": v(-1.06, -53.99) * mm, "end": v(-0.93, -54) * mm});
            skArc(sketch, "E52.54.14", {"start": v(1.85, -53.97) * mm, "mid": v(1.98, -53.96) * mm, "end": v(2.11, -53.96) * mm});
            skLineSegment(sketch, "E52.54.15", {"start": v(-1.19, -53.99) * mm, "end": v(-0.92, -54) * mm});
            skLineSegment(sketch, "E52.55.0", {"start": v(3.46, -54.4) * mm, "end": v(2.1, -53.96) * mm});
            skPoint(sketch, "E52.55.1", {"position": v(3.1, -52) * mm});
            skPoint(sketch, "E52.55.2", {"position": v(2.5, -53.94) * mm});
            skArc(sketch, "E52.55.3", {"start": v(3.24, -52) * mm, "mid": v(3.62, -51.97) * mm, "end": v(4, -51.95) * mm});
            skPoint(sketch, "E52.55.4", {"position": v(5, -53.77) * mm});
            skPoint(sketch, "E52.55.5", {"position": v(4.13, -51.94) * mm});
            skLineSegment(sketch, "E52.55.6", {"start": v(3.06, -52.14) * mm, "end": v(2.55, -53.8) * mm});
            skLineSegment(sketch, "E52.55.7", {"start": v(5.4, -53.73) * mm, "end": v(3.46, -54.4) * mm});
            skLineSegment(sketch, "E52.55.8", {"start": v(4.94, -53.64) * mm, "end": v(4.2, -52.06) * mm});
            skArc(sketch, "E52.55.9", {"start": v(3.24, -52) * mm, "mid": v(3.13, -52.04) * mm, "end": v(3.06, -52.14) * mm});
            skArc(sketch, "E52.55.10", {"start": v(4.2, -52.06) * mm, "mid": v(4.11, -51.97) * mm, "end": v(4, -51.95) * mm});
            skArc(sketch, "E52.55.11", {"start": v(4.94, -53.64) * mm, "mid": v(5.02, -53.73) * mm, "end": v(5.14, -53.76) * mm});
            skArc(sketch, "E52.55.12", {"start": v(2.36, -53.95) * mm, "mid": v(2.48, -53.9) * mm, "end": v(2.55, -53.8) * mm});
            skArc(sketch, "E52.55.13", {"start": v(2.1, -53.96) * mm, "mid": v(2.23, -53.95) * mm, "end": v(2.36, -53.95) * mm});
            skArc(sketch, "E52.55.14", {"start": v(5.14, -53.76) * mm, "mid": v(5.27, -53.74) * mm, "end": v(5.4, -53.73) * mm});
            skLineSegment(sketch, "E52.55.15", {"start": v(2.1, -53.96) * mm, "end": v(2.37, -53.95) * mm});
            skLineSegment(sketch, "E52.56.0", {"start": v(6.77, -54.1) * mm, "end": v(5.39, -53.73) * mm});
            skPoint(sketch, "E52.56.1", {"position": v(6.27, -51.72) * mm});
            skPoint(sketch, "E52.56.2", {"position": v(5.79, -53.69) * mm});
            skArc(sketch, "E52.56.3", {"start": v(6.4, -51.7) * mm, "mid": v(6.78, -51.66) * mm, "end": v(7.16, -51.6) * mm});
            skPoint(sketch, "E52.56.4", {"position": v(8.27, -53.36) * mm});
            skPoint(sketch, "E52.56.5", {"position": v(7.3, -51.59) * mm});
            skLineSegment(sketch, "E52.56.6", {"start": v(6.24, -51.86) * mm, "end": v(5.82, -53.55) * mm});
            skLineSegment(sketch, "E52.56.7", {"start": v(8.66, -53.3) * mm, "end": v(6.77, -54.1) * mm});
            skLineSegment(sketch, "E52.56.8", {"start": v(8.2, -53.24) * mm, "end": v(7.36, -51.7) * mm});
            skArc(sketch, "E52.56.9", {"start": v(6.4, -51.7) * mm, "mid": v(6.3, -51.75) * mm, "end": v(6.24, -51.86) * mm});
            skArc(sketch, "E52.56.10", {"start": v(7.36, -51.7) * mm, "mid": v(7.27, -51.63) * mm, "end": v(7.16, -51.6) * mm});
            skArc(sketch, "E52.56.11", {"start": v(8.2, -53.24) * mm, "mid": v(8.29, -53.32) * mm, "end": v(8.4, -53.34) * mm});
            skArc(sketch, "E52.56.12", {"start": v(5.65, -53.7) * mm, "mid": v(5.76, -53.66) * mm, "end": v(5.82, -53.55) * mm});
            skArc(sketch, "E52.56.13", {"start": v(5.39, -53.73) * mm, "mid": v(5.52, -53.72) * mm, "end": v(5.65, -53.7) * mm});
            skArc(sketch, "E52.56.14", {"start": v(8.4, -53.34) * mm, "mid": v(8.53, -53.32) * mm, "end": v(8.66, -53.3) * mm});
            skLineSegment(sketch, "E52.56.15", {"start": v(5.39, -53.73) * mm, "end": v(5.66, -53.7) * mm});
            skLineSegment(sketch, "E52.57.0", {"start": v(10.05, -53.58) * mm, "end": v(8.66, -53.3) * mm});
            skPoint(sketch, "E52.57.1", {"position": v(9.41, -51.24) * mm});
            skPoint(sketch, "E52.57.2", {"position": v(9.05, -53.24) * mm});
            skArc(sketch, "E52.57.3", {"start": v(9.55, -51.22) * mm, "mid": v(9.92, -51.15) * mm, "end": v(10.29, -51.07) * mm});
            skPoint(sketch, "E52.57.4", {"position": v(11.5, -52.76) * mm});
            skPoint(sketch, "E52.57.5", {"position": v(10.42, -51.05) * mm});
            skLineSegment(sketch, "E52.57.6", {"start": v(9.39, -51.38) * mm, "end": v(9.07, -53.1) * mm});
            skLineSegment(sketch, "E52.57.7", {"start": v(11.9, -52.67) * mm, "end": v(10.05, -53.58) * mm});
            skLineSegment(sketch, "E52.57.8", {"start": v(11.43, -52.64) * mm, "end": v(10.5, -51.16) * mm});
            skArc(sketch, "E52.57.9", {"start": v(9.55, -51.22) * mm, "mid": v(9.44, -51.27) * mm, "end": v(9.39, -51.38) * mm});
            skArc(sketch, "E52.57.10", {"start": v(10.5, -51.16) * mm, "mid": v(10.4, -51.09) * mm, "end": v(10.29, -51.07) * mm});
            skArc(sketch, "E52.57.11", {"start": v(11.43, -52.64) * mm, "mid": v(11.52, -52.72) * mm, "end": v(11.64, -52.73) * mm});
            skArc(sketch, "E52.57.12", {"start": v(8.91, -53.26) * mm, "mid": v(9.02, -53.2) * mm, "end": v(9.07, -53.1) * mm});
            skArc(sketch, "E52.57.13", {"start": v(8.66, -53.3) * mm, "mid": v(8.78, -53.28) * mm, "end": v(8.91, -53.26) * mm});
            skArc(sketch, "E52.57.14", {"start": v(11.64, -52.73) * mm, "mid": v(11.77, -52.7) * mm, "end": v(11.9, -52.67) * mm});
            skLineSegment(sketch, "E52.57.15", {"start": v(8.66, -53.3) * mm, "end": v(8.92, -53.26) * mm});
            skLineSegment(sketch, "E52.58.0", {"start": v(13.3, -52.86) * mm, "end": v(11.89, -52.68) * mm});
            skPoint(sketch, "E52.58.1", {"position": v(12.52, -50.57) * mm});
            skPoint(sketch, "E52.58.2", {"position": v(12.28, -52.59) * mm});
            skArc(sketch, "E52.58.3", {"start": v(12.65, -50.54) * mm, "mid": v(13.02, -50.45) * mm, "end": v(13.38, -50.35) * mm});
            skPoint(sketch, "E52.58.4", {"position": v(14.7, -51.96) * mm});
            skPoint(sketch, "E52.58.5", {"position": v(13.52, -50.32) * mm});
            skLineSegment(sketch, "E52.58.6", {"start": v(12.5, -50.71) * mm, "end": v(12.3, -52.45) * mm});
            skLineSegment(sketch, "E52.58.7", {"start": v(15.08, -51.85) * mm, "end": v(13.3, -52.86) * mm});
            skLineSegment(sketch, "E52.58.8", {"start": v(14.62, -51.85) * mm, "end": v(13.6, -50.43) * mm});
            skArc(sketch, "E52.58.9", {"start": v(12.65, -50.54) * mm, "mid": v(12.55, -50.6) * mm, "end": v(12.5, -50.71) * mm});
            skArc(sketch, "E52.58.10", {"start": v(13.6, -50.43) * mm, "mid": v(13.5, -50.36) * mm, "end": v(13.38, -50.35) * mm});
            skArc(sketch, "E52.58.11", {"start": v(14.62, -51.85) * mm, "mid": v(14.71, -51.92) * mm, "end": v(14.83, -51.92) * mm});
            skArc(sketch, "E52.58.12", {"start": v(12.14, -52.62) * mm, "mid": v(12.25, -52.56) * mm, "end": v(12.3, -52.45) * mm});
            skArc(sketch, "E52.58.13", {"start": v(11.89, -52.68) * mm, "mid": v(12.02, -52.65) * mm, "end": v(12.14, -52.62) * mm});
            skArc(sketch, "E52.58.14", {"start": v(14.83, -51.92) * mm, "mid": v(14.96, -51.89) * mm, "end": v(15.08, -51.85) * mm});
            skLineSegment(sketch, "E52.58.15", {"start": v(11.89, -52.68) * mm, "end": v(12.15, -52.61) * mm});
            skLineSegment(sketch, "E52.59.0", {"start": v(16.5, -51.96) * mm, "end": v(15.08, -51.85) * mm});
            skPoint(sketch, "E52.59.1", {"position": v(15.58, -49.72) * mm});
            skPoint(sketch, "E52.59.2", {"position": v(15.46, -51.74) * mm});
            skArc(sketch, "E52.59.3", {"start": v(15.7, -49.68) * mm, "mid": v(16.07, -49.56) * mm, "end": v(16.43, -49.44) * mm});
            skPoint(sketch, "E52.59.4", {"position": v(17.84, -50.97) * mm});
            skPoint(sketch, "E52.59.5", {"position": v(16.56, -49.4) * mm});
            skLineSegment(sketch, "E52.59.6", {"start": v(15.57, -49.85) * mm, "end": v(15.47, -51.6) * mm});
            skLineSegment(sketch, "E52.59.7", {"start": v(18.22, -50.83) * mm, "end": v(16.5, -51.96) * mm});
            skLineSegment(sketch, "E52.59.8", {"start": v(17.75, -50.86) * mm, "end": v(16.65, -49.5) * mm});
            skArc(sketch, "E52.59.9", {"start": v(15.7, -49.68) * mm, "mid": v(15.61, -49.74) * mm, "end": v(15.57, -49.85) * mm});
            skArc(sketch, "E52.59.10", {"start": v(16.65, -49.5) * mm, "mid": v(16.55, -49.44) * mm, "end": v(16.43, -49.44) * mm});
            skArc(sketch, "E52.59.11", {"start": v(17.75, -50.86) * mm, "mid": v(17.85, -50.93) * mm, "end": v(17.97, -50.92) * mm});
            skArc(sketch, "E52.59.12", {"start": v(15.33, -51.78) * mm, "mid": v(15.43, -51.71) * mm, "end": v(15.47, -51.6) * mm});
            skArc(sketch, "E52.59.13", {"start": v(15.08, -51.85) * mm, "mid": v(15.2, -51.82) * mm, "end": v(15.33, -51.78) * mm});
            skArc(sketch, "E52.59.14", {"start": v(17.97, -50.92) * mm, "mid": v(18.1, -50.88) * mm, "end": v(18.22, -50.83) * mm});
            skLineSegment(sketch, "E52.59.15", {"start": v(15.08, -51.85) * mm, "end": v(15.34, -51.78) * mm});
            skLineSegment(sketch, "E52.60.0", {"start": v(19.64, -50.85) * mm, "end": v(18.21, -50.84) * mm});
            skPoint(sketch, "E52.60.1", {"position": v(18.58, -48.67) * mm});
            skPoint(sketch, "E52.60.2", {"position": v(18.59, -50.7) * mm});
            skArc(sketch, "E52.60.3", {"start": v(18.7, -48.63) * mm, "mid": v(19.06, -48.49) * mm, "end": v(19.41, -48.35) * mm});
            skPoint(sketch, "E52.60.4", {"position": v(20.91, -49.79) * mm});
            skPoint(sketch, "E52.60.5", {"position": v(19.54, -48.3) * mm});
            skLineSegment(sketch, "E52.60.6", {"start": v(18.58, -48.81) * mm, "end": v(18.59, -50.56) * mm});
            skLineSegment(sketch, "E52.60.7", {"start": v(21.28, -49.63) * mm, "end": v(19.64, -50.85) * mm});
            skLineSegment(sketch, "E52.60.8", {"start": v(20.82, -49.68) * mm, "end": v(19.63, -48.4) * mm});
            skArc(sketch, "E52.60.9", {"start": v(18.7, -48.63) * mm, "mid": v(18.61, -48.7) * mm, "end": v(18.58, -48.81) * mm});
            skArc(sketch, "E52.60.10", {"start": v(19.63, -48.4) * mm, "mid": v(19.53, -48.34) * mm, "end": v(19.41, -48.35) * mm});
            skArc(sketch, "E52.60.11", {"start": v(20.82, -49.68) * mm, "mid": v(20.92, -49.74) * mm, "end": v(21.04, -49.73) * mm});
            skArc(sketch, "E52.60.12", {"start": v(18.45, -50.75) * mm, "mid": v(18.55, -50.68) * mm, "end": v(18.59, -50.56) * mm});
            skArc(sketch, "E52.60.13", {"start": v(18.21, -50.84) * mm, "mid": v(18.33, -50.8) * mm, "end": v(18.45, -50.75) * mm});
            skArc(sketch, "E52.60.14", {"start": v(21.04, -49.73) * mm, "mid": v(21.16, -49.68) * mm, "end": v(21.28, -49.63) * mm});
            skLineSegment(sketch, "E52.60.15", {"start": v(18.21, -50.84) * mm, "end": v(18.47, -50.74) * mm});
            skLineSegment(sketch, "E52.61.0", {"start": v(22.7, -49.56) * mm, "end": v(21.28, -49.63) * mm});
            skPoint(sketch, "E52.61.1", {"position": v(21.51, -47.45) * mm});
            skPoint(sketch, "E52.61.2", {"position": v(21.64, -49.47) * mm});
            skArc(sketch, "E52.61.3", {"start": v(21.64, -47.4) * mm, "mid": v(21.98, -47.24) * mm, "end": v(22.32, -47.08) * mm});
            skPoint(sketch, "E52.61.4", {"position": v(23.91, -48.42) * mm});
            skPoint(sketch, "E52.61.5", {"position": v(22.45, -47.02) * mm});
            skLineSegment(sketch, "E52.61.6", {"start": v(21.52, -47.59) * mm, "end": v(21.63, -49.33) * mm});
            skLineSegment(sketch, "E52.61.7", {"start": v(24.27, -48.24) * mm, "end": v(22.7, -49.56) * mm});
            skLineSegment(sketch, "E52.61.8", {"start": v(23.8, -48.32) * mm, "end": v(22.55, -47.11) * mm});
            skArc(sketch, "E52.61.9", {"start": v(21.64, -47.4) * mm, "mid": v(21.55, -47.47) * mm, "end": v(21.52, -47.59) * mm});
            skArc(sketch, "E52.61.10", {"start": v(22.55, -47.11) * mm, "mid": v(22.44, -47.06) * mm, "end": v(22.32, -47.08) * mm});
            skArc(sketch, "E52.61.11", {"start": v(23.8, -48.32) * mm, "mid": v(23.92, -48.37) * mm, "end": v(24.04, -48.36) * mm});
            skArc(sketch, "E52.61.12", {"start": v(21.51, -49.53) * mm, "mid": v(21.6, -49.45) * mm, "end": v(21.63, -49.33) * mm});
            skArc(sketch, "E52.61.13", {"start": v(21.28, -49.63) * mm, "mid": v(21.4, -49.58) * mm, "end": v(21.51, -49.53) * mm});
            skArc(sketch, "E52.61.14", {"start": v(24.04, -48.36) * mm, "mid": v(24.15, -48.3) * mm, "end": v(24.27, -48.24) * mm});
            skLineSegment(sketch, "E52.61.15", {"start": v(21.28, -49.63) * mm, "end": v(21.52, -49.52) * mm});
            skLineSegment(sketch, "E52.62.0", {"start": v(25.68, -48.09) * mm, "end": v(24.26, -48.24) * mm});
            skPoint(sketch, "E52.62.1", {"position": v(24.37, -46.05) * mm});
            skPoint(sketch, "E52.62.2", {"position": v(24.62, -48.06) * mm});
            skArc(sketch, "E52.62.3", {"start": v(24.49, -45.99) * mm, "mid": v(24.82, -45.8) * mm, "end": v(25.15, -45.63) * mm});
            skPoint(sketch, "E52.62.4", {"position": v(26.82, -46.87) * mm});
            skPoint(sketch, "E52.62.5", {"position": v(25.27, -45.56) * mm});
            skLineSegment(sketch, "E52.62.6", {"start": v(24.38, -46.19) * mm, "end": v(24.6, -47.92) * mm});
            skLineSegment(sketch, "E52.62.7", {"start": v(27.16, -46.67) * mm, "end": v(25.68, -48.09) * mm});
            skLineSegment(sketch, "E52.62.8", {"start": v(26.71, -46.78) * mm, "end": v(25.38, -45.65) * mm});
            skArc(sketch, "E52.62.9", {"start": v(24.49, -45.99) * mm, "mid": v(24.4, -46.07) * mm, "end": v(24.38, -46.19) * mm});
            skArc(sketch, "E52.62.10", {"start": v(25.38, -45.65) * mm, "mid": v(25.27, -45.6) * mm, "end": v(25.15, -45.63) * mm});
            skArc(sketch, "E52.62.11", {"start": v(26.71, -46.78) * mm, "mid": v(26.82, -46.83) * mm, "end": v(26.94, -46.8) * mm});
            skArc(sketch, "E52.62.12", {"start": v(24.5, -48.13) * mm, "mid": v(24.58, -48.04) * mm, "end": v(24.6, -47.92) * mm});
            skArc(sketch, "E52.62.13", {"start": v(24.26, -48.24) * mm, "mid": v(24.38, -48.18) * mm, "end": v(24.5, -48.13) * mm});
            skArc(sketch, "E52.62.14", {"start": v(26.94, -46.8) * mm, "mid": v(27.05, -46.74) * mm, "end": v(27.16, -46.67) * mm});
            skLineSegment(sketch, "E52.62.15", {"start": v(24.26, -48.24) * mm, "end": v(24.5, -48.12) * mm});
            skLineSegment(sketch, "E52.63.0", {"start": v(28.56, -46.43) * mm, "end": v(27.16, -46.67) * mm});
            skPoint(sketch, "E52.63.1", {"position": v(27.13, -44.48) * mm});
            skPoint(sketch, "E52.63.2", {"position": v(27.5, -46.47) * mm});
            skArc(sketch, "E52.63.3", {"start": v(27.24, -44.4) * mm, "mid": v(27.57, -44.2) * mm, "end": v(27.89, -44) * mm});
            skPoint(sketch, "E52.63.4", {"position": v(29.62, -45.15) * mm});
            skPoint(sketch, "E52.63.5", {"position": v(28, -43.93) * mm});
            skLineSegment(sketch, "E52.63.6", {"start": v(27.15, -44.62) * mm, "end": v(27.48, -46.33) * mm});
            skLineSegment(sketch, "E52.63.7", {"start": v(29.96, -44.93) * mm, "end": v(28.56, -46.43) * mm});
            skLineSegment(sketch, "E52.63.8", {"start": v(29.51, -45.06) * mm, "end": v(28.11, -44.02) * mm});
            skArc(sketch, "E52.63.9", {"start": v(27.24, -44.4) * mm, "mid": v(27.17, -44.5) * mm, "end": v(27.15, -44.62) * mm});
            skArc(sketch, "E52.63.10", {"start": v(28.11, -44.02) * mm, "mid": v(28, -43.98) * mm, "end": v(27.89, -44) * mm});
            skArc(sketch, "E52.63.11", {"start": v(29.51, -45.06) * mm, "mid": v(29.63, -45.1) * mm, "end": v(29.74, -45.07) * mm});
            skArc(sketch, "E52.63.12", {"start": v(27.38, -46.54) * mm, "mid": v(27.46, -46.45) * mm, "end": v(27.48, -46.33) * mm});
            skArc(sketch, "E52.63.13", {"start": v(27.16, -46.67) * mm, "mid": v(27.27, -46.6) * mm, "end": v(27.38, -46.54) * mm});
            skArc(sketch, "E52.63.14", {"start": v(29.74, -45.07) * mm, "mid": v(29.85, -45) * mm, "end": v(29.96, -44.93) * mm});
            skLineSegment(sketch, "E52.63.15", {"start": v(27.16, -46.67) * mm, "end": v(27.4, -46.54) * mm});
            skLineSegment(sketch, "E52.64.0", {"start": v(31.34, -44.6) * mm, "end": v(29.95, -44.93) * mm});
            skPoint(sketch, "E52.64.1", {"position": v(29.79, -42.74) * mm});
            skPoint(sketch, "E52.64.2", {"position": v(30.29, -44.7) * mm});
            skArc(sketch, "E52.64.3", {"start": v(29.9, -42.67) * mm, "mid": v(30.21, -42.45) * mm, "end": v(30.52, -42.23) * mm});
            skPoint(sketch, "E52.64.4", {"position": v(32.32, -43.26) * mm});
            skPoint(sketch, "E52.64.5", {"position": v(30.63, -42.15) * mm});
            skLineSegment(sketch, "E52.64.6", {"start": v(29.82, -42.88) * mm, "end": v(30.25, -44.57) * mm});
            skLineSegment(sketch, "E52.64.7", {"start": v(32.64, -43.02) * mm, "end": v(31.34, -44.6) * mm});
            skLineSegment(sketch, "E52.64.8", {"start": v(32.2, -43.18) * mm, "end": v(30.74, -42.22) * mm});
            skArc(sketch, "E52.64.9", {"start": v(29.9, -42.67) * mm, "mid": v(29.83, -42.76) * mm, "end": v(29.82, -42.88) * mm});
            skArc(sketch, "E52.64.10", {"start": v(30.74, -42.22) * mm, "mid": v(30.63, -42.19) * mm, "end": v(30.52, -42.23) * mm});
            skArc(sketch, "E52.64.11", {"start": v(32.2, -43.18) * mm, "mid": v(32.32, -43.21) * mm, "end": v(32.43, -43.17) * mm});
            skArc(sketch, "E52.64.12", {"start": v(30.17, -44.79) * mm, "mid": v(30.24, -44.7) * mm, "end": v(30.25, -44.57) * mm});
            skArc(sketch, "E52.64.13", {"start": v(29.95, -44.93) * mm, "mid": v(30.06, -44.86) * mm, "end": v(30.17, -44.79) * mm});
            skArc(sketch, "E52.64.14", {"start": v(32.43, -43.17) * mm, "mid": v(32.54, -43.1) * mm, "end": v(32.64, -43.02) * mm});
            skLineSegment(sketch, "E52.64.15", {"start": v(29.95, -44.93) * mm, "end": v(30.18, -44.78) * mm});
            skLineSegment(sketch, "E52.65.0", {"start": v(34, -42.6) * mm, "end": v(32.64, -43.02) * mm});
            skPoint(sketch, "E52.65.1", {"position": v(32.34, -40.85) * mm});
            skPoint(sketch, "E52.65.2", {"position": v(32.95, -42.78) * mm});
            skArc(sketch, "E52.65.3", {"start": v(32.45, -40.76) * mm, "mid": v(32.74, -40.53) * mm, "end": v(33.04, -40.29) * mm});
            skPoint(sketch, "E52.65.4", {"position": v(34.9, -41.2) * mm});
            skPoint(sketch, "E52.65.5", {"position": v(33.14, -40.2) * mm});
            skLineSegment(sketch, "E52.65.6", {"start": v(32.38, -40.98) * mm, "end": v(32.91, -42.64) * mm});
            skLineSegment(sketch, "E52.65.7", {"start": v(35.2, -40.95) * mm, "end": v(34, -42.6) * mm});
            skLineSegment(sketch, "E52.65.8", {"start": v(34.78, -41.14) * mm, "end": v(33.26, -40.27) * mm});
            skArc(sketch, "E52.65.9", {"start": v(32.45, -40.76) * mm, "mid": v(32.38, -40.86) * mm, "end": v(32.38, -40.98) * mm});
            skArc(sketch, "E52.65.10", {"start": v(33.26, -40.27) * mm, "mid": v(33.15, -40.24) * mm, "end": v(33.04, -40.29) * mm});
            skArc(sketch, "E52.65.11", {"start": v(34.78, -41.14) * mm, "mid": v(34.9, -41.16) * mm, "end": v(35, -41.12) * mm});
            skArc(sketch, "E52.65.12", {"start": v(32.84, -42.86) * mm, "mid": v(32.91, -42.77) * mm, "end": v(32.91, -42.64) * mm});
            skArc(sketch, "E52.65.13", {"start": v(32.64, -43.02) * mm, "mid": v(32.74, -42.94) * mm, "end": v(32.84, -42.86) * mm});
            skArc(sketch, "E52.65.14", {"start": v(35, -41.12) * mm, "mid": v(35.1, -41.03) * mm, "end": v(35.2, -40.95) * mm});
            skLineSegment(sketch, "E52.65.15", {"start": v(32.64, -43.02) * mm, "end": v(32.85, -42.86) * mm});
            skLineSegment(sketch, "E52.66.0", {"start": v(36.54, -40.46) * mm, "end": v(35.2, -40.95) * mm});
            skPoint(sketch, "E52.66.1", {"position": v(34.77, -38.8) * mm});
            skPoint(sketch, "E52.66.2", {"position": v(35.5, -40.69) * mm});
            skArc(sketch, "E52.66.3", {"start": v(34.87, -38.7) * mm, "mid": v(35.15, -38.45) * mm, "end": v(35.43, -38.2) * mm});
            skPoint(sketch, "E52.66.4", {"position": v(37.35, -39) * mm});
            skPoint(sketch, "E52.66.5", {"position": v(35.53, -38.1) * mm});
            skLineSegment(sketch, "E52.66.6", {"start": v(34.82, -38.93) * mm, "end": v(35.45, -40.56) * mm});
            skLineSegment(sketch, "E52.66.7", {"start": v(37.63, -38.73) * mm, "end": v(36.54, -40.46) * mm});
            skLineSegment(sketch, "E52.66.8", {"start": v(37.22, -38.94) * mm, "end": v(35.65, -38.17) * mm});
            skArc(sketch, "E52.66.9", {"start": v(34.87, -38.7) * mm, "mid": v(34.81, -38.81) * mm, "end": v(34.82, -38.93) * mm});
            skArc(sketch, "E52.66.10", {"start": v(35.65, -38.17) * mm, "mid": v(35.54, -38.15) * mm, "end": v(35.43, -38.2) * mm});
            skArc(sketch, "E52.66.11", {"start": v(37.22, -38.94) * mm, "mid": v(37.34, -38.96) * mm, "end": v(37.45, -38.9) * mm});
            skArc(sketch, "E52.66.12", {"start": v(35.4, -40.78) * mm, "mid": v(35.46, -40.68) * mm, "end": v(35.45, -40.56) * mm});
            skArc(sketch, "E52.66.13", {"start": v(35.2, -40.95) * mm, "mid": v(35.3, -40.87) * mm, "end": v(35.4, -40.78) * mm});
            skArc(sketch, "E52.66.14", {"start": v(37.45, -38.9) * mm, "mid": v(37.54, -38.82) * mm, "end": v(37.63, -38.73) * mm});
            skLineSegment(sketch, "E52.66.15", {"start": v(35.2, -40.95) * mm, "end": v(35.4, -40.77) * mm});
            skLineSegment(sketch, "E52.67.0", {"start": v(38.93, -38.15) * mm, "end": v(37.63, -38.73) * mm});
            skPoint(sketch, "E52.67.1", {"position": v(37.07, -36.6) * mm});
            skPoint(sketch, "E52.67.2", {"position": v(37.92, -38.45) * mm});
            skArc(sketch, "E52.67.3", {"start": v(37.17, -36.51) * mm, "mid": v(37.43, -36.24) * mm, "end": v(37.7, -35.97) * mm});
            skPoint(sketch, "E52.67.4", {"position": v(39.65, -36.65) * mm});
            skPoint(sketch, "E52.67.5", {"position": v(37.79, -35.87) * mm});
            skLineSegment(sketch, "E52.67.6", {"start": v(37.13, -36.73) * mm, "end": v(37.86, -38.32) * mm});
            skLineSegment(sketch, "E52.67.7", {"start": v(39.93, -36.36) * mm, "end": v(38.93, -38.15) * mm});
            skLineSegment(sketch, "E52.67.8", {"start": v(39.53, -36.6) * mm, "end": v(37.91, -35.92) * mm});
            skArc(sketch, "E52.67.9", {"start": v(37.17, -36.51) * mm, "mid": v(37.11, -36.62) * mm, "end": v(37.13, -36.73) * mm});
            skArc(sketch, "E52.67.10", {"start": v(37.91, -35.92) * mm, "mid": v(37.8, -35.9) * mm, "end": v(37.7, -35.97) * mm});
            skArc(sketch, "E52.67.11", {"start": v(39.53, -36.6) * mm, "mid": v(39.65, -36.61) * mm, "end": v(39.75, -36.55) * mm});
            skArc(sketch, "E52.67.12", {"start": v(37.82, -38.55) * mm, "mid": v(37.87, -38.44) * mm, "end": v(37.86, -38.32) * mm});
            skArc(sketch, "E52.67.13", {"start": v(37.63, -38.73) * mm, "mid": v(37.72, -38.64) * mm, "end": v(37.82, -38.55) * mm});
            skArc(sketch, "E52.67.14", {"start": v(39.75, -36.55) * mm, "mid": v(39.84, -36.45) * mm, "end": v(39.93, -36.36) * mm});
            skLineSegment(sketch, "E52.67.15", {"start": v(37.63, -38.73) * mm, "end": v(37.82, -38.54) * mm});
            skLineSegment(sketch, "E52.68.0", {"start": v(41.19, -35.71) * mm, "end": v(39.92, -36.36) * mm});
            skPoint(sketch, "E52.68.1", {"position": v(39.23, -34.28) * mm});
            skPoint(sketch, "E52.68.2", {"position": v(40.19, -36.07) * mm});
            skArc(sketch, "E52.68.3", {"start": v(39.32, -34.18) * mm, "mid": v(39.57, -33.9) * mm, "end": v(39.82, -33.6) * mm});
            skPoint(sketch, "E52.68.4", {"position": v(41.82, -34.17) * mm});
            skPoint(sketch, "E52.68.5", {"position": v(39.9, -33.5) * mm});
            skLineSegment(sketch, "E52.68.6", {"start": v(39.3, -34.4) * mm, "end": v(40.12, -35.94) * mm});
            skLineSegment(sketch, "E52.68.7", {"start": v(42.07, -33.86) * mm, "end": v(41.19, -35.71) * mm});
            skLineSegment(sketch, "E52.68.8", {"start": v(41.68, -34.12) * mm, "end": v(40.03, -33.54) * mm});
            skArc(sketch, "E52.68.9", {"start": v(39.32, -34.18) * mm, "mid": v(39.28, -34.29) * mm, "end": v(39.3, -34.4) * mm});
            skArc(sketch, "E52.68.10", {"start": v(40.03, -33.54) * mm, "mid": v(39.92, -33.54) * mm, "end": v(39.82, -33.6) * mm});
            skArc(sketch, "E52.68.11", {"start": v(41.68, -34.12) * mm, "mid": v(41.8, -34.13) * mm, "end": v(41.9, -34.06) * mm});
            skArc(sketch, "E52.68.12", {"start": v(40.1, -36.17) * mm, "mid": v(40.15, -36.06) * mm, "end": v(40.12, -35.94) * mm});
            skArc(sketch, "E52.68.13", {"start": v(39.92, -36.36) * mm, "mid": v(40, -36.27) * mm, "end": v(40.1, -36.17) * mm});
            skArc(sketch, "E52.68.14", {"start": v(41.9, -34.06) * mm, "mid": v(41.99, -33.96) * mm, "end": v(42.07, -33.86) * mm});
            skLineSegment(sketch, "E52.68.15", {"start": v(39.92, -36.36) * mm, "end": v(40.1, -36.16) * mm});
            skLineSegment(sketch, "E52.69.0", {"start": v(43.29, -33.13) * mm, "end": v(42.06, -33.86) * mm});
            skPoint(sketch, "E52.69.1", {"position": v(41.25, -31.83) * mm});
            skPoint(sketch, "E52.69.2", {"position": v(42.31, -33.55) * mm});
            skArc(sketch, "E52.69.3", {"start": v(41.33, -31.72) * mm, "mid": v(41.56, -31.42) * mm, "end": v(41.79, -31.11) * mm});
            skPoint(sketch, "E52.69.4", {"position": v(43.82, -31.56) * mm});
            skPoint(sketch, "E52.69.5", {"position": v(41.87, -31) * mm});
            skLineSegment(sketch, "E52.69.6", {"start": v(41.32, -31.94) * mm, "end": v(42.24, -33.43) * mm});
            skLineSegment(sketch, "E52.69.7", {"start": v(44.05, -31.23) * mm, "end": v(43.29, -33.13) * mm});
            skLineSegment(sketch, "E52.69.8", {"start": v(43.69, -31.52) * mm, "end": v(42, -31.04) * mm});
            skArc(sketch, "E52.69.9", {"start": v(41.33, -31.72) * mm, "mid": v(41.3, -31.83) * mm, "end": v(41.32, -31.94) * mm});
            skArc(sketch, "E52.69.10", {"start": v(42, -31.04) * mm, "mid": v(41.89, -31.04) * mm, "end": v(41.79, -31.11) * mm});
            skArc(sketch, "E52.69.11", {"start": v(43.69, -31.52) * mm, "mid": v(43.8, -31.51) * mm, "end": v(43.9, -31.44) * mm});
            skArc(sketch, "E52.69.12", {"start": v(42.23, -33.66) * mm, "mid": v(42.27, -33.55) * mm, "end": v(42.24, -33.43) * mm});
            skArc(sketch, "E52.69.13", {"start": v(42.06, -33.86) * mm, "mid": v(42.14, -33.76) * mm, "end": v(42.23, -33.66) * mm});
            skArc(sketch, "E52.69.14", {"start": v(43.9, -31.44) * mm, "mid": v(43.98, -31.34) * mm, "end": v(44.05, -31.23) * mm});
            skLineSegment(sketch, "E52.69.15", {"start": v(42.06, -33.86) * mm, "end": v(42.23, -33.65) * mm});
            skLineSegment(sketch, "E52.70.0", {"start": v(45.23, -30.43) * mm, "end": v(44.05, -31.23) * mm});
            skPoint(sketch, "E52.70.1", {"position": v(43.11, -29.25) * mm});
            skPoint(sketch, "E52.70.2", {"position": v(44.28, -30.9) * mm});
            skArc(sketch, "E52.70.3", {"start": v(43.2, -29.14) * mm, "mid": v(43.4, -28.82) * mm, "end": v(43.6, -28.5) * mm});
            skPoint(sketch, "E52.70.4", {"position": v(45.66, -28.82) * mm});
            skPoint(sketch, "E52.70.5", {"position": v(43.68, -28.4) * mm});
            skLineSegment(sketch, "E52.70.6", {"start": v(43.2, -29.36) * mm, "end": v(44.2, -30.8) * mm});
            skLineSegment(sketch, "E52.70.7", {"start": v(45.88, -28.49) * mm, "end": v(45.23, -30.43) * mm});
            skLineSegment(sketch, "E52.70.8", {"start": v(45.53, -28.8) * mm, "end": v(43.82, -28.42) * mm});
            skArc(sketch, "E52.70.9", {"start": v(43.2, -29.14) * mm, "mid": v(43.16, -29.25) * mm, "end": v(43.2, -29.36) * mm});
            skArc(sketch, "E52.70.10", {"start": v(43.82, -28.42) * mm, "mid": v(43.7, -28.43) * mm, "end": v(43.6, -28.5) * mm});
            skArc(sketch, "E52.70.11", {"start": v(45.53, -28.8) * mm, "mid": v(45.65, -28.78) * mm, "end": v(45.74, -28.7) * mm});
            skArc(sketch, "E52.70.12", {"start": v(44.2, -31.02) * mm, "mid": v(44.24, -30.9) * mm, "end": v(44.2, -30.8) * mm});
            skArc(sketch, "E52.70.13", {"start": v(44.05, -31.23) * mm, "mid": v(44.12, -31.13) * mm, "end": v(44.2, -31.02) * mm});
            skArc(sketch, "E52.70.14", {"start": v(45.74, -28.7) * mm, "mid": v(45.8, -28.6) * mm, "end": v(45.88, -28.49) * mm});
            skLineSegment(sketch, "E52.70.15", {"start": v(44.05, -31.23) * mm, "end": v(44.2, -31.01) * mm});
            skLineSegment(sketch, "E52.71.0", {"start": v(47, -27.62) * mm, "end": v(45.87, -28.5) * mm});
            skPoint(sketch, "E52.71.1", {"position": v(44.82, -26.57) * mm});
            skPoint(sketch, "E52.71.2", {"position": v(46.08, -28.15) * mm});
            skArc(sketch, "E52.71.3", {"start": v(44.89, -26.45) * mm, "mid": v(45.08, -26.12) * mm, "end": v(45.27, -25.8) * mm});
            skPoint(sketch, "E52.71.4", {"position": v(47.34, -25.99) * mm});
            skPoint(sketch, "E52.71.5", {"position": v(45.33, -25.68) * mm});
            skLineSegment(sketch, "E52.71.6", {"start": v(44.9, -26.68) * mm, "end": v(46, -28.04) * mm});
            skLineSegment(sketch, "E52.71.7", {"start": v(47.53, -25.64) * mm, "end": v(47, -27.62) * mm});
            skLineSegment(sketch, "E52.71.8", {"start": v(47.2, -25.97) * mm, "end": v(45.47, -25.7) * mm});
            skArc(sketch, "E52.71.9", {"start": v(44.89, -26.45) * mm, "mid": v(44.86, -26.57) * mm, "end": v(44.9, -26.68) * mm});
            skArc(sketch, "E52.71.10", {"start": v(45.47, -25.7) * mm, "mid": v(45.35, -25.71) * mm, "end": v(45.27, -25.8) * mm});
            skArc(sketch, "E52.71.11", {"start": v(47.2, -25.97) * mm, "mid": v(47.32, -25.95) * mm, "end": v(47.4, -25.86) * mm});
            skArc(sketch, "E52.71.12", {"start": v(46, -28.27) * mm, "mid": v(46.04, -28.15) * mm, "end": v(46, -28.04) * mm});
            skArc(sketch, "E52.71.13", {"start": v(45.87, -28.5) * mm, "mid": v(45.94, -28.38) * mm, "end": v(46, -28.27) * mm});
            skArc(sketch, "E52.71.14", {"start": v(47.4, -25.86) * mm, "mid": v(47.46, -25.75) * mm, "end": v(47.53, -25.64) * mm});
            skLineSegment(sketch, "E52.71.15", {"start": v(45.87, -28.5) * mm, "end": v(46.01, -28.26) * mm});
            skLineSegment(sketch, "E52.72.0", {"start": v(48.6, -24.7) * mm, "end": v(47.52, -25.64) * mm});
            skPoint(sketch, "E52.72.1", {"position": v(46.35, -23.79) * mm});
            skPoint(sketch, "E52.72.2", {"position": v(47.71, -25.29) * mm});
            skArc(sketch, "E52.72.3", {"start": v(46.42, -23.66) * mm, "mid": v(46.59, -23.33) * mm, "end": v(46.75, -22.99) * mm});
            skPoint(sketch, "E52.72.4", {"position": v(48.83, -23.05) * mm});
            skPoint(sketch, "E52.72.5", {"position": v(46.81, -22.86) * mm});
            skLineSegment(sketch, "E52.72.6", {"start": v(46.45, -23.89) * mm, "end": v(47.62, -25.18) * mm});
            skLineSegment(sketch, "E52.72.7", {"start": v(49, -22.7) * mm, "end": v(48.6, -24.7) * mm});
            skLineSegment(sketch, "E52.72.8", {"start": v(48.7, -23.04) * mm, "end": v(46.95, -22.88) * mm});
            skArc(sketch, "E52.72.9", {"start": v(46.42, -23.66) * mm, "mid": v(46.4, -23.78) * mm, "end": v(46.45, -23.89) * mm});
            skArc(sketch, "E52.72.10", {"start": v(46.95, -22.88) * mm, "mid": v(46.84, -22.9) * mm, "end": v(46.75, -22.99) * mm});
            skArc(sketch, "E52.72.11", {"start": v(48.7, -23.04) * mm, "mid": v(48.8, -23.01) * mm, "end": v(48.9, -22.93) * mm});
            skArc(sketch, "E52.72.12", {"start": v(47.65, -25.41) * mm, "mid": v(47.67, -25.3) * mm, "end": v(47.62, -25.18) * mm});
            skArc(sketch, "E52.72.13", {"start": v(47.52, -25.64) * mm, "mid": v(47.59, -25.53) * mm, "end": v(47.65, -25.41) * mm});
            skArc(sketch, "E52.72.14", {"start": v(48.9, -22.93) * mm, "mid": v(48.95, -22.8) * mm, "end": v(49, -22.7) * mm});
            skLineSegment(sketch, "E52.72.15", {"start": v(47.52, -25.64) * mm, "end": v(47.65, -25.4) * mm});
            skLineSegment(sketch, "E52.73.0", {"start": v(50, -21.7) * mm, "end": v(49, -22.7) * mm});
            skPoint(sketch, "E52.73.1", {"position": v(47.72, -20.92) * mm});
            skPoint(sketch, "E52.73.2", {"position": v(49.17, -22.33) * mm});
            skArc(sketch, "E52.73.3", {"start": v(47.77, -20.8) * mm, "mid": v(47.92, -20.44) * mm, "end": v(48.07, -20.1) * mm});
            skPoint(sketch, "E52.73.4", {"position": v(50.15, -20.03) * mm});
            skPoint(sketch, "E52.73.5", {"position": v(48.12, -19.97) * mm});
            skLineSegment(sketch, "E52.73.6", {"start": v(47.82, -21.01) * mm, "end": v(49.06, -22.24) * mm});
            skLineSegment(sketch, "E52.73.7", {"start": v(50.3, -19.66) * mm, "end": v(50, -21.7) * mm});
            skLineSegment(sketch, "E52.73.8", {"start": v(50, -20.03) * mm, "end": v(48.26, -19.97) * mm});
            skArc(sketch, "E52.73.9", {"start": v(47.77, -20.8) * mm, "mid": v(47.76, -20.9) * mm, "end": v(47.82, -21.01) * mm});
            skArc(sketch, "E52.73.10", {"start": v(48.26, -19.97) * mm, "mid": v(48.14, -20) * mm, "end": v(48.07, -20.1) * mm});
            skArc(sketch, "E52.73.11", {"start": v(50, -20.03) * mm, "mid": v(50.12, -20) * mm, "end": v(50.2, -19.9) * mm});
            skArc(sketch, "E52.73.12", {"start": v(49.1, -22.46) * mm, "mid": v(49.12, -22.34) * mm, "end": v(49.06, -22.24) * mm});
            skArc(sketch, "E52.73.13", {"start": v(49, -22.7) * mm, "mid": v(49.05, -22.58) * mm, "end": v(49.1, -22.46) * mm});
            skArc(sketch, "E52.73.14", {"start": v(50.2, -19.9) * mm, "mid": v(50.25, -19.78) * mm, "end": v(50.3, -19.66) * mm});
            skLineSegment(sketch, "E52.73.15", {"start": v(49, -22.7) * mm, "end": v(49.11, -22.45) * mm});
            skLineSegment(sketch, "E52.74.0", {"start": v(51.24, -18.6) * mm, "end": v(50.3, -19.67) * mm});
            skPoint(sketch, "E52.74.1", {"position": v(48.9, -17.97) * mm});
            skPoint(sketch, "E52.74.2", {"position": v(50.44, -19.3) * mm});
            skArc(sketch, "E52.74.3", {"start": v(48.95, -17.84) * mm, "mid": v(49.08, -17.48) * mm, "end": v(49.2, -17.13) * mm});
            skPoint(sketch, "E52.74.4", {"position": v(51.27, -16.94) * mm});
            skPoint(sketch, "E52.74.5", {"position": v(49.25, -17) * mm});
            skLineSegment(sketch, "E52.74.6", {"start": v(49, -18.06) * mm, "end": v(50.33, -19.2) * mm});
            skLineSegment(sketch, "E52.74.7", {"start": v(51.4, -16.56) * mm, "end": v(51.24, -18.6) * mm});
            skLineSegment(sketch, "E52.74.8", {"start": v(51.13, -16.94) * mm, "end": v(49.39, -17) * mm});
            skArc(sketch, "E52.74.9", {"start": v(48.95, -17.84) * mm, "mid": v(48.94, -17.96) * mm, "end": v(49, -18.06) * mm});
            skArc(sketch, "E52.74.10", {"start": v(49.39, -17) * mm, "mid": v(49.27, -17.03) * mm, "end": v(49.2, -17.13) * mm});
            skArc(sketch, "E52.74.11", {"start": v(51.13, -16.94) * mm, "mid": v(51.25, -16.9) * mm, "end": v(51.32, -16.8) * mm});
            skArc(sketch, "E52.74.12", {"start": v(50.38, -19.43) * mm, "mid": v(50.4, -19.3) * mm, "end": v(50.33, -19.2) * mm});
            skArc(sketch, "E52.74.13", {"start": v(50.3, -19.67) * mm, "mid": v(50.34, -19.55) * mm, "end": v(50.38, -19.43) * mm});
            skArc(sketch, "E52.74.14", {"start": v(51.32, -16.8) * mm, "mid": v(51.36, -16.68) * mm, "end": v(51.4, -16.56) * mm});
            skLineSegment(sketch, "E52.74.15", {"start": v(50.3, -19.67) * mm, "end": v(50.39, -19.42) * mm});
            skLineSegment(sketch, "E52.75.0", {"start": v(52.28, -15.45) * mm, "end": v(51.4, -16.57) * mm});
            skPoint(sketch, "E52.75.1", {"position": v(49.9, -14.95) * mm});
            skPoint(sketch, "E52.75.2", {"position": v(51.52, -16.18) * mm});
            skArc(sketch, "E52.75.3", {"start": v(49.95, -14.82) * mm, "mid": v(50.05, -14.46) * mm, "end": v(50.16, -14.1) * mm});
            skPoint(sketch, "E52.75.4", {"position": v(52.21, -13.78) * mm});
            skPoint(sketch, "E52.75.5", {"position": v(50.2, -13.96) * mm});
            skLineSegment(sketch, "E52.75.6", {"start": v(50.02, -15.04) * mm, "end": v(51.4, -16.1) * mm});
            skLineSegment(sketch, "E52.75.7", {"start": v(52.31, -13.4) * mm, "end": v(52.28, -15.45) * mm});
            skLineSegment(sketch, "E52.75.8", {"start": v(52.07, -13.8) * mm, "end": v(50.33, -13.95) * mm});
            skArc(sketch, "E52.75.9", {"start": v(49.95, -14.82) * mm, "mid": v(49.95, -14.94) * mm, "end": v(50.02, -15.04) * mm});
            skArc(sketch, "E52.75.10", {"start": v(50.33, -13.95) * mm, "mid": v(50.22, -14) * mm, "end": v(50.16, -14.1) * mm});
            skArc(sketch, "E52.75.11", {"start": v(52.07, -13.8) * mm, "mid": v(52.18, -13.75) * mm, "end": v(52.25, -13.65) * mm});
            skArc(sketch, "E52.75.12", {"start": v(51.48, -16.32) * mm, "mid": v(51.48, -16.2) * mm, "end": v(51.4, -16.1) * mm});
            skArc(sketch, "E52.75.13", {"start": v(51.4, -16.57) * mm, "mid": v(51.44, -16.44) * mm, "end": v(51.48, -16.32) * mm});
            skArc(sketch, "E52.75.14", {"start": v(52.25, -13.65) * mm, "mid": v(52.28, -13.52) * mm, "end": v(52.31, -13.4) * mm});
            skLineSegment(sketch, "E52.75.15", {"start": v(51.4, -16.57) * mm, "end": v(51.48, -16.3) * mm});
            skLineSegment(sketch, "E52.76.0", {"start": v(53.12, -12.23) * mm, "end": v(52.31, -13.4) * mm});
            skPoint(sketch, "E52.76.1", {"position": v(50.73, -11.88) * mm});
            skPoint(sketch, "E52.76.2", {"position": v(52.4, -13.01) * mm});
            skArc(sketch, "E52.76.3", {"start": v(50.76, -11.75) * mm, "mid": v(50.84, -11.38) * mm, "end": v(50.92, -11.01) * mm});
            skPoint(sketch, "E52.76.4", {"position": v(52.95, -10.57) * mm});
            skPoint(sketch, "E52.76.5", {"position": v(50.95, -10.88) * mm});
            skLineSegment(sketch, "E52.76.6", {"start": v(50.84, -11.96) * mm, "end": v(52.3, -12.93) * mm});
            skLineSegment(sketch, "E52.76.7", {"start": v(53.03, -10.18) * mm, "end": v(53.12, -12.23) * mm});
            skLineSegment(sketch, "E52.76.8", {"start": v(52.82, -10.6) * mm, "end": v(51.09, -10.86) * mm});
            skArc(sketch, "E52.76.9", {"start": v(50.76, -11.75) * mm, "mid": v(50.77, -11.87) * mm, "end": v(50.84, -11.96) * mm});
            skArc(sketch, "E52.76.10", {"start": v(51.09, -10.86) * mm, "mid": v(50.98, -10.9) * mm, "end": v(50.92, -11.01) * mm});
            skArc(sketch, "E52.76.11", {"start": v(52.82, -10.6) * mm, "mid": v(52.92, -10.54) * mm, "end": v(52.98, -10.44) * mm});
            skArc(sketch, "E52.76.12", {"start": v(52.37, -13.15) * mm, "mid": v(52.37, -13.03) * mm, "end": v(52.3, -12.93) * mm});
            skArc(sketch, "E52.76.13", {"start": v(52.31, -13.4) * mm, "mid": v(52.34, -13.28) * mm, "end": v(52.37, -13.15) * mm});
            skArc(sketch, "E52.76.14", {"start": v(52.98, -10.44) * mm, "mid": v(53, -10.3) * mm, "end": v(53.03, -10.18) * mm});
            skLineSegment(sketch, "E52.76.15", {"start": v(52.31, -13.4) * mm, "end": v(52.38, -13.14) * mm});
            skLineSegment(sketch, "E52.77.0", {"start": v(53.77, -8.97) * mm, "end": v(53.03, -10.19) * mm});
            skPoint(sketch, "E52.77.1", {"position": v(51.36, -8.77) * mm});
            skPoint(sketch, "E52.77.2", {"position": v(53.1, -9.8) * mm});
            skArc(sketch, "E52.77.3", {"start": v(51.38, -8.63) * mm, "mid": v(51.44, -8.26) * mm, "end": v(51.5, -7.89) * mm});
            skPoint(sketch, "E52.77.4", {"position": v(53.5, -7.33) * mm});
            skPoint(sketch, "E52.77.5", {"position": v(51.52, -7.75) * mm});
            skLineSegment(sketch, "E52.77.6", {"start": v(51.48, -8.84) * mm, "end": v(52.98, -9.72) * mm});
            skLineSegment(sketch, "E52.77.7", {"start": v(53.55, -6.93) * mm, "end": v(53.77, -8.97) * mm});
            skLineSegment(sketch, "E52.77.8", {"start": v(53.36, -7.35) * mm, "end": v(51.66, -7.72) * mm});
            skArc(sketch, "E52.77.9", {"start": v(51.38, -8.63) * mm, "mid": v(51.4, -8.75) * mm, "end": v(51.48, -8.84) * mm});
            skArc(sketch, "E52.77.10", {"start": v(51.66, -7.72) * mm, "mid": v(51.55, -7.78) * mm, "end": v(51.5, -7.89) * mm});
            skArc(sketch, "E52.77.11", {"start": v(53.36, -7.35) * mm, "mid": v(53.47, -7.3) * mm, "end": v(53.52, -7.19) * mm});
            skArc(sketch, "E52.77.12", {"start": v(53.08, -9.93) * mm, "mid": v(53.06, -9.81) * mm, "end": v(52.98, -9.72) * mm});
            skArc(sketch, "E52.77.13", {"start": v(53.03, -10.19) * mm, "mid": v(53.05, -10.06) * mm, "end": v(53.08, -9.93) * mm});
            skArc(sketch, "E52.77.14", {"start": v(53.52, -7.19) * mm, "mid": v(53.54, -7.06) * mm, "end": v(53.55, -6.93) * mm});
            skLineSegment(sketch, "E52.77.15", {"start": v(53.03, -10.19) * mm, "end": v(53.08, -9.92) * mm});
            skLineSegment(sketch, "E52.78.0", {"start": v(54.22, -5.67) * mm, "end": v(53.55, -6.93) * mm});
            skPoint(sketch, "E52.78.1", {"position": v(51.8, -5.62) * mm});
            skPoint(sketch, "E52.78.2", {"position": v(53.6, -6.54) * mm});
            skArc(sketch, "E52.78.3", {"start": v(51.81, -5.49) * mm, "mid": v(51.85, -5.1) * mm, "end": v(51.88, -4.73) * mm});
            skPoint(sketch, "E52.78.4", {"position": v(53.85, -4.05) * mm});
            skPoint(sketch, "E52.78.5", {"position": v(51.9, -4.6) * mm});
            skLineSegment(sketch, "E52.78.6", {"start": v(51.92, -5.68) * mm, "end": v(53.48, -6.47) * mm});
            skLineSegment(sketch, "E52.78.7", {"start": v(53.88, -3.65) * mm, "end": v(54.22, -5.67) * mm});
            skLineSegment(sketch, "E52.78.8", {"start": v(53.71, -4.09) * mm, "end": v(52.03, -4.56) * mm});
            skArc(sketch, "E52.78.9", {"start": v(51.81, -5.49) * mm, "mid": v(51.83, -5.6) * mm, "end": v(51.92, -5.68) * mm});
            skArc(sketch, "E52.78.10", {"start": v(52.03, -4.56) * mm, "mid": v(51.93, -4.62) * mm, "end": v(51.88, -4.73) * mm});
            skArc(sketch, "E52.78.11", {"start": v(53.71, -4.09) * mm, "mid": v(53.81, -4.02) * mm, "end": v(53.86, -3.9) * mm});
            skArc(sketch, "E52.78.12", {"start": v(53.59, -6.68) * mm, "mid": v(53.56, -6.56) * mm, "end": v(53.48, -6.47) * mm});
            skArc(sketch, "E52.78.13", {"start": v(53.55, -6.93) * mm, "mid": v(53.57, -6.8) * mm, "end": v(53.59, -6.68) * mm});
            skArc(sketch, "E52.78.14", {"start": v(53.86, -3.9) * mm, "mid": v(53.87, -3.78) * mm, "end": v(53.88, -3.65) * mm});
            skLineSegment(sketch, "E52.78.15", {"start": v(53.55, -6.93) * mm, "end": v(53.59, -6.67) * mm});
            skLineSegment(sketch, "E52.79.0", {"start": v(54.46, -2.36) * mm, "end": v(53.88, -3.66) * mm});
            skPoint(sketch, "E52.79.1", {"position": v(52.04, -2.45) * mm});
            skPoint(sketch, "E52.79.2", {"position": v(53.9, -3.26) * mm});
            skArc(sketch, "E52.79.3", {"start": v(52.05, -2.32) * mm, "mid": v(52.06, -1.94) * mm, "end": v(52.08, -1.56) * mm});
            skPoint(sketch, "E52.79.4", {"position": v(54, -0.76) * mm});
            skPoint(sketch, "E52.79.5", {"position": v(52.08, -1.42) * mm});
            skLineSegment(sketch, "E52.79.6", {"start": v(52.17, -2.5) * mm, "end": v(53.77, -3.2) * mm});
            skLineSegment(sketch, "E52.79.7", {"start": v(54, -0.36) * mm, "end": v(54.46, -2.36) * mm});
            skLineSegment(sketch, "E52.79.8", {"start": v(53.86, -0.8) * mm, "end": v(52.21, -1.38) * mm});
            skArc(sketch, "E52.79.9", {"start": v(52.05, -2.32) * mm, "mid": v(52.08, -2.43) * mm, "end": v(52.17, -2.5) * mm});
            skArc(sketch, "E52.79.10", {"start": v(52.21, -1.38) * mm, "mid": v(52.12, -1.45) * mm, "end": v(52.08, -1.56) * mm});
            skArc(sketch, "E52.79.11", {"start": v(53.86, -0.8) * mm, "mid": v(53.96, -0.73) * mm, "end": v(54, -0.62) * mm});
            skArc(sketch, "E52.79.12", {"start": v(53.9, -3.4) * mm, "mid": v(53.86, -3.28) * mm, "end": v(53.77, -3.2) * mm});
            skArc(sketch, "E52.79.13", {"start": v(53.88, -3.66) * mm, "mid": v(53.88, -3.53) * mm, "end": v(53.9, -3.4) * mm});
            skArc(sketch, "E52.79.14", {"start": v(54, -0.62) * mm, "mid": v(54, -0.49) * mm, "end": v(54, -0.36) * mm});
            skLineSegment(sketch, "E52.79.15", {"start": v(53.88, -3.66) * mm, "end": v(53.9, -3.39) * mm});
            skLineSegment(sketch, "E52.80.0", {"start": v(54.5, 0.97) * mm, "end": v(54, -0.37) * mm});
            skPoint(sketch, "E52.80.1", {"position": v(52.1, 0.72) * mm});
            skPoint(sketch, "E52.80.2", {"position": v(54, 0.03) * mm});
            skArc(sketch, "E52.80.3", {"start": v(52.1, 0.86) * mm, "mid": v(52.09, 1.24) * mm, "end": v(52.07, 1.62) * mm});
            skPoint(sketch, "E52.80.4", {"position": v(53.94, 2.53) * mm});
            skPoint(sketch, "E52.80.5", {"position": v(52.07, 1.75) * mm});
            skLineSegment(sketch, "E52.80.6", {"start": v(52.22, 0.68) * mm, "end": v(53.87, 0.08) * mm});
            skLineSegment(sketch, "E52.80.7", {"start": v(53.92, 2.93) * mm, "end": v(54.5, 0.97) * mm});
            skLineSegment(sketch, "E52.80.8", {"start": v(53.81, 2.48) * mm, "end": v(52.2, 1.8) * mm});
            skArc(sketch, "E52.80.9", {"start": v(52.1, 0.86) * mm, "mid": v(52.13, 0.75) * mm, "end": v(52.22, 0.68) * mm});
            skArc(sketch, "E52.80.10", {"start": v(52.2, 1.8) * mm, "mid": v(52.1, 1.73) * mm, "end": v(52.07, 1.62) * mm});
            skArc(sketch, "E52.80.11", {"start": v(53.81, 2.48) * mm, "mid": v(53.9, 2.56) * mm, "end": v(53.93, 2.67) * mm});
            skArc(sketch, "E52.80.12", {"start": v(54, -0.1) * mm, "mid": v(53.96, 0) * mm, "end": v(53.87, 0.08) * mm});
            skArc(sketch, "E52.80.13", {"start": v(54, -0.37) * mm, "mid": v(54, -0.24) * mm, "end": v(54, -0.1) * mm});
            skArc(sketch, "E52.80.14", {"start": v(53.93, 2.67) * mm, "mid": v(53.93, 2.8) * mm, "end": v(53.92, 2.93) * mm});
            skLineSegment(sketch, "E52.80.15", {"start": v(54, -0.37) * mm, "end": v(54, -0.1) * mm});
            skLineSegment(sketch, "E52.81.0", {"start": v(54.34, 4.29) * mm, "end": v(53.92, 2.93) * mm});
            skPoint(sketch, "E52.81.1", {"position": v(51.95, 3.9) * mm});
            skPoint(sketch, "E52.81.2", {"position": v(53.9, 3.33) * mm});
            skArc(sketch, "E52.81.3", {"start": v(51.94, 4.04) * mm, "mid": v(51.91, 4.41) * mm, "end": v(51.88, 4.79) * mm});
            skPoint(sketch, "E52.81.4", {"position": v(53.69, 5.82) * mm});
            skPoint(sketch, "E52.81.5", {"position": v(51.87, 4.93) * mm});
            skLineSegment(sketch, "E52.81.6", {"start": v(52.09, 3.86) * mm, "end": v(53.76, 3.37) * mm});
            skLineSegment(sketch, "E52.81.7", {"start": v(53.64, 6.21) * mm, "end": v(54.34, 4.29) * mm});
            skLineSegment(sketch, "E52.81.8", {"start": v(53.56, 5.76) * mm, "end": v(52, 4.99) * mm});
            skArc(sketch, "E52.81.9", {"start": v(51.94, 4.04) * mm, "mid": v(51.99, 3.92) * mm, "end": v(52.09, 3.86) * mm});
            skArc(sketch, "E52.81.10", {"start": v(52, 4.99) * mm, "mid": v(51.9, 4.9) * mm, "end": v(51.88, 4.79) * mm});
            skArc(sketch, "E52.81.11", {"start": v(53.56, 5.76) * mm, "mid": v(53.65, 5.84) * mm, "end": v(53.67, 5.96) * mm});
            skArc(sketch, "E52.81.12", {"start": v(53.9, 3.19) * mm, "mid": v(53.86, 3.3) * mm, "end": v(53.76, 3.37) * mm});
            skArc(sketch, "E52.81.13", {"start": v(53.92, 2.93) * mm, "mid": v(53.91, 3.06) * mm, "end": v(53.9, 3.19) * mm});
            skArc(sketch, "E52.81.14", {"start": v(53.67, 5.96) * mm, "mid": v(53.66, 6.09) * mm, "end": v(53.64, 6.21) * mm});
            skLineSegment(sketch, "E52.81.15", {"start": v(53.92, 2.93) * mm, "end": v(53.9, 3.2) * mm});
            skLineSegment(sketch, "E52.82.0", {"start": v(53.98, 7.6) * mm, "end": v(53.64, 6.2) * mm});
            skPoint(sketch, "E52.82.1", {"position": v(51.62, 7.06) * mm});
            skPoint(sketch, "E52.82.2", {"position": v(53.6, 6.6) * mm});
            skArc(sketch, "E52.82.3", {"start": v(51.6, 7.2) * mm, "mid": v(51.55, 7.57) * mm, "end": v(51.5, 7.94) * mm});
            skPoint(sketch, "E52.82.4", {"position": v(53.23, 9.08) * mm});
            skPoint(sketch, "E52.82.5", {"position": v(51.47, 8.08) * mm});
            skLineSegment(sketch, "E52.82.6", {"start": v(51.75, 7.03) * mm, "end": v(53.46, 6.64) * mm});
            skLineSegment(sketch, "E52.82.7", {"start": v(53.16, 9.47) * mm, "end": v(53.98, 7.6) * mm});
            skLineSegment(sketch, "E52.82.8", {"start": v(53.1, 9) * mm, "end": v(51.59, 8.15) * mm});
            skArc(sketch, "E52.82.9", {"start": v(51.6, 7.2) * mm, "mid": v(51.65, 7.09) * mm, "end": v(51.75, 7.03) * mm});
            skArc(sketch, "E52.82.10", {"start": v(51.59, 8.15) * mm, "mid": v(51.5, 8.06) * mm, "end": v(51.5, 7.94) * mm});
            skArc(sketch, "E52.82.11", {"start": v(53.1, 9) * mm, "mid": v(53.2, 9.1) * mm, "end": v(53.2, 9.22) * mm});
            skArc(sketch, "E52.82.12", {"start": v(53.61, 6.47) * mm, "mid": v(53.56, 6.58) * mm, "end": v(53.46, 6.64) * mm});
            skArc(sketch, "E52.82.13", {"start": v(53.64, 6.2) * mm, "mid": v(53.63, 6.34) * mm, "end": v(53.61, 6.47) * mm});
            skArc(sketch, "E52.82.14", {"start": v(53.2, 9.22) * mm, "mid": v(53.19, 9.35) * mm, "end": v(53.16, 9.47) * mm});
            skLineSegment(sketch, "E52.82.15", {"start": v(53.64, 6.2) * mm, "end": v(53.6, 6.48) * mm});
            skLineSegment(sketch, "E52.83.0", {"start": v(53.42, 10.87) * mm, "end": v(53.16, 9.47) * mm});
            skPoint(sketch, "E52.83.1", {"position": v(51.1, 10.2) * mm});
            skPoint(sketch, "E52.83.2", {"position": v(53.1, 9.86) * mm});
            skArc(sketch, "E52.83.3", {"start": v(51.07, 10.33) * mm, "mid": v(51, 10.7) * mm, "end": v(50.91, 11.07) * mm});
            skPoint(sketch, "E52.83.4", {"position": v(52.58, 12.3) * mm});
            skPoint(sketch, "E52.83.5", {"position": v(50.88, 11.2) * mm});
            skLineSegment(sketch, "E52.83.6", {"start": v(51.23, 10.17) * mm, "end": v(52.95, 9.88) * mm});
            skLineSegment(sketch, "E52.83.7", {"start": v(52.49, 12.7) * mm, "end": v(53.42, 10.87) * mm});
            skLineSegment(sketch, "E52.83.8", {"start": v(52.46, 12.23) * mm, "end": v(51, 11.28) * mm});
            skArc(sketch, "E52.83.9", {"start": v(51.07, 10.33) * mm, "mid": v(51.12, 10.22) * mm, "end": v(51.23, 10.17) * mm});
            skArc(sketch, "E52.83.10", {"start": v(51, 11.28) * mm, "mid": v(50.92, 11.19) * mm, "end": v(50.91, 11.07) * mm});
            skArc(sketch, "E52.83.11", {"start": v(52.46, 12.23) * mm, "mid": v(52.54, 12.32) * mm, "end": v(52.55, 12.44) * mm});
            skArc(sketch, "E52.83.12", {"start": v(53.12, 9.72) * mm, "mid": v(53.06, 9.83) * mm, "end": v(52.95, 9.88) * mm});
            skArc(sketch, "E52.83.13", {"start": v(53.16, 9.47) * mm, "mid": v(53.14, 9.6) * mm, "end": v(53.12, 9.72) * mm});
            skArc(sketch, "E52.83.14", {"start": v(52.55, 12.44) * mm, "mid": v(52.52, 12.57) * mm, "end": v(52.49, 12.7) * mm});
            skLineSegment(sketch, "E52.83.15", {"start": v(53.16, 9.47) * mm, "end": v(53.12, 9.73) * mm});
            skLineSegment(sketch, "E52.84.0", {"start": v(52.66, 14.1) * mm, "end": v(52.49, 12.7) * mm});
            skPoint(sketch, "E52.84.1", {"position": v(50.38, 13.29) * mm});
            skPoint(sketch, "E52.84.2", {"position": v(52.4, 13.08) * mm});
            skArc(sketch, "E52.84.3", {"start": v(50.34, 13.42) * mm, "mid": v(50.24, 13.79) * mm, "end": v(50.14, 14.15) * mm});
            skPoint(sketch, "E52.84.4", {"position": v(51.73, 15.5) * mm});
            skPoint(sketch, "E52.84.5", {"position": v(50.1, 14.28) * mm});
            skLineSegment(sketch, "E52.84.6", {"start": v(50.51, 13.27) * mm, "end": v(52.25, 13.1) * mm});
            skLineSegment(sketch, "E52.84.7", {"start": v(51.61, 15.87) * mm, "end": v(52.66, 14.1) * mm});
            skLineSegment(sketch, "E52.84.8", {"start": v(51.62, 15.4) * mm, "end": v(50.21, 14.36) * mm});
            skArc(sketch, "E52.84.9", {"start": v(50.34, 13.42) * mm, "mid": v(50.4, 13.32) * mm, "end": v(50.51, 13.27) * mm});
            skArc(sketch, "E52.84.10", {"start": v(50.21, 14.36) * mm, "mid": v(50.14, 14.27) * mm, "end": v(50.14, 14.15) * mm});
            skArc(sketch, "E52.84.11", {"start": v(51.62, 15.4) * mm, "mid": v(51.69, 15.5) * mm, "end": v(51.7, 15.62) * mm});
            skArc(sketch, "E52.84.12", {"start": v(52.43, 12.94) * mm, "mid": v(52.36, 13.05) * mm, "end": v(52.25, 13.1) * mm});
            skArc(sketch, "E52.84.13", {"start": v(52.49, 12.7) * mm, "mid": v(52.46, 12.82) * mm, "end": v(52.43, 12.94) * mm});
            skArc(sketch, "E52.84.14", {"start": v(51.7, 15.62) * mm, "mid": v(51.65, 15.75) * mm, "end": v(51.61, 15.87) * mm});
            skLineSegment(sketch, "E52.84.15", {"start": v(52.49, 12.7) * mm, "end": v(52.42, 12.95) * mm});
            skLineSegment(sketch, "E52.85.0", {"start": v(51.7, 17.29) * mm, "end": v(51.62, 15.87) * mm});
            skPoint(sketch, "E52.85.1", {"position": v(49.47, 16.33) * mm});
            skPoint(sketch, "E52.85.2", {"position": v(51.5, 16.25) * mm});
            skArc(sketch, "E52.85.3", {"start": v(49.43, 16.46) * mm, "mid": v(49.3, 16.82) * mm, "end": v(49.19, 17.18) * mm});
            skPoint(sketch, "E52.85.4", {"position": v(50.7, 18.62) * mm});
            skPoint(sketch, "E52.85.5", {"position": v(49.14, 17.31) * mm});
            skLineSegment(sketch, "E52.85.6", {"start": v(49.61, 16.33) * mm, "end": v(51.36, 16.25) * mm});
            skLineSegment(sketch, "E52.85.7", {"start": v(50.55, 19) * mm, "end": v(51.7, 17.29) * mm});
            skLineSegment(sketch, "E52.85.8", {"start": v(50.58, 18.52) * mm, "end": v(49.25, 17.4) * mm});
            skArc(sketch, "E52.85.9", {"start": v(49.43, 16.46) * mm, "mid": v(49.5, 16.37) * mm, "end": v(49.61, 16.33) * mm});
            skArc(sketch, "E52.85.10", {"start": v(49.25, 17.4) * mm, "mid": v(49.18, 17.3) * mm, "end": v(49.19, 17.18) * mm});
            skArc(sketch, "E52.85.11", {"start": v(50.58, 18.52) * mm, "mid": v(50.65, 18.63) * mm, "end": v(50.64, 18.75) * mm});
            skArc(sketch, "E52.85.12", {"start": v(51.54, 16.11) * mm, "mid": v(51.47, 16.21) * mm, "end": v(51.36, 16.25) * mm});
            skArc(sketch, "E52.85.13", {"start": v(51.62, 15.87) * mm, "mid": v(51.58, 16) * mm, "end": v(51.54, 16.11) * mm});
            skArc(sketch, "E52.85.14", {"start": v(50.64, 18.75) * mm, "mid": v(50.6, 18.87) * mm, "end": v(50.55, 19) * mm});
            skLineSegment(sketch, "E52.85.15", {"start": v(51.62, 15.87) * mm, "end": v(51.54, 16.13) * mm});
            skLineSegment(sketch, "E52.86.0", {"start": v(50.55, 20.4) * mm, "end": v(50.55, 18.98) * mm});
            skPoint(sketch, "E52.86.1", {"position": v(48.39, 19.32) * mm});
            skPoint(sketch, "E52.86.2", {"position": v(50.41, 19.36) * mm});
            skArc(sketch, "E52.86.3", {"start": v(48.33, 19.45) * mm, "mid": v(48.2, 19.8) * mm, "end": v(48.05, 20.15) * mm});
            skPoint(sketch, "E52.86.4", {"position": v(49.46, 21.67) * mm});
            skPoint(sketch, "E52.86.5", {"position": v(48, 20.27) * mm});
            skLineSegment(sketch, "E52.86.6", {"start": v(48.52, 19.32) * mm, "end": v(50.27, 19.36) * mm});
            skLineSegment(sketch, "E52.86.7", {"start": v(49.3, 22.04) * mm, "end": v(50.55, 20.4) * mm});
            skLineSegment(sketch, "E52.86.8", {"start": v(49.36, 21.57) * mm, "end": v(48.1, 20.37) * mm});
            skArc(sketch, "E52.86.9", {"start": v(48.33, 19.45) * mm, "mid": v(48.4, 19.36) * mm, "end": v(48.52, 19.32) * mm});
            skArc(sketch, "E52.86.10", {"start": v(48.1, 20.37) * mm, "mid": v(48.04, 20.27) * mm, "end": v(48.05, 20.15) * mm});
            skArc(sketch, "E52.86.11", {"start": v(49.36, 21.57) * mm, "mid": v(49.42, 21.68) * mm, "end": v(49.4, 21.8) * mm});
            skArc(sketch, "E52.86.12", {"start": v(50.46, 19.23) * mm, "mid": v(50.39, 19.32) * mm, "end": v(50.27, 19.36) * mm});
            skArc(sketch, "E52.86.13", {"start": v(50.55, 18.98) * mm, "mid": v(50.5, 19.1) * mm, "end": v(50.46, 19.23) * mm});
            skArc(sketch, "E52.86.14", {"start": v(49.4, 21.8) * mm, "mid": v(49.35, 21.92) * mm, "end": v(49.3, 22.04) * mm});
            skLineSegment(sketch, "E52.86.15", {"start": v(50.55, 18.98) * mm, "end": v(50.46, 19.24) * mm});
            skLineSegment(sketch, "E52.87.0", {"start": v(49.2, 23.45) * mm, "end": v(49.3, 22.03) * mm});
            skPoint(sketch, "E52.87.1", {"position": v(47.12, 22.23) * mm});
            skPoint(sketch, "E52.87.2", {"position": v(49.14, 22.4) * mm});
            skArc(sketch, "E52.87.3", {"start": v(47.06, 22.36) * mm, "mid": v(46.9, 22.7) * mm, "end": v(46.73, 23.04) * mm});
            skPoint(sketch, "E52.87.4", {"position": v(48.05, 24.65) * mm});
            skPoint(sketch, "E52.87.5", {"position": v(46.67, 23.16) * mm});
            skLineSegment(sketch, "E52.87.6", {"start": v(47.26, 22.24) * mm, "end": v(49, 22.38) * mm});
            skLineSegment(sketch, "E52.87.7", {"start": v(47.86, 25) * mm, "end": v(49.2, 23.45) * mm});
            skLineSegment(sketch, "E52.87.8", {"start": v(47.95, 24.54) * mm, "end": v(46.76, 23.26) * mm});
            skArc(sketch, "E52.87.9", {"start": v(47.06, 22.36) * mm, "mid": v(47.14, 22.27) * mm, "end": v(47.26, 22.24) * mm});
            skArc(sketch, "E52.87.10", {"start": v(46.76, 23.26) * mm, "mid": v(46.71, 23.16) * mm, "end": v(46.73, 23.04) * mm});
            skArc(sketch, "E52.87.11", {"start": v(47.95, 24.54) * mm, "mid": v(48, 24.65) * mm, "end": v(47.98, 24.77) * mm});
            skArc(sketch, "E52.87.12", {"start": v(49.2, 22.27) * mm, "mid": v(49.11, 22.36) * mm, "end": v(49, 22.38) * mm});
            skArc(sketch, "E52.87.13", {"start": v(49.3, 22.03) * mm, "mid": v(49.25, 22.15) * mm, "end": v(49.2, 22.27) * mm});
            skArc(sketch, "E52.87.14", {"start": v(47.98, 24.77) * mm, "mid": v(47.92, 24.89) * mm, "end": v(47.86, 25) * mm});
            skLineSegment(sketch, "E52.87.15", {"start": v(49.3, 22.03) * mm, "end": v(49.2, 22.28) * mm});
            skLineSegment(sketch, "E52.88.0", {"start": v(47.69, 26.4) * mm, "end": v(47.87, 25) * mm});
            skPoint(sketch, "E52.88.1", {"position": v(45.67, 25.06) * mm});
            skPoint(sketch, "E52.88.2", {"position": v(47.68, 25.35) * mm});
            skArc(sketch, "E52.88.3", {"start": v(45.6, 25.19) * mm, "mid": v(45.42, 25.52) * mm, "end": v(45.24, 25.84) * mm});
            skPoint(sketch, "E52.88.4", {"position": v(46.46, 27.53) * mm});
            skPoint(sketch, "E52.88.5", {"position": v(45.17, 25.96) * mm});
            skLineSegment(sketch, "E52.88.6", {"start": v(45.81, 25.08) * mm, "end": v(47.54, 25.33) * mm});
            skLineSegment(sketch, "E52.88.7", {"start": v(46.25, 27.87) * mm, "end": v(47.69, 26.4) * mm});
            skLineSegment(sketch, "E52.88.8", {"start": v(46.37, 27.42) * mm, "end": v(45.26, 26.07) * mm});
            skArc(sketch, "E52.88.9", {"start": v(45.6, 25.19) * mm, "mid": v(45.7, 25.1) * mm, "end": v(45.81, 25.08) * mm});
            skArc(sketch, "E52.88.10", {"start": v(45.26, 26.07) * mm, "mid": v(45.21, 25.96) * mm, "end": v(45.24, 25.84) * mm});
            skArc(sketch, "E52.88.11", {"start": v(46.37, 27.42) * mm, "mid": v(46.41, 27.53) * mm, "end": v(46.38, 27.65) * mm});
            skArc(sketch, "E52.88.12", {"start": v(47.75, 25.22) * mm, "mid": v(47.66, 25.3) * mm, "end": v(47.54, 25.33) * mm});
            skArc(sketch, "E52.88.13", {"start": v(47.87, 25) * mm, "mid": v(47.8, 25.11) * mm, "end": v(47.75, 25.22) * mm});
            skArc(sketch, "E52.88.14", {"start": v(46.38, 27.65) * mm, "mid": v(46.32, 27.76) * mm, "end": v(46.25, 27.87) * mm});
            skLineSegment(sketch, "E52.88.15", {"start": v(47.87, 25) * mm, "end": v(47.74, 25.23) * mm});
            skLineSegment(sketch, "E52.89.0", {"start": v(45.99, 29.27) * mm, "end": v(46.25, 27.87) * mm});
            skPoint(sketch, "E52.89.1", {"position": v(44.06, 27.8) * mm});
            skPoint(sketch, "E52.89.2", {"position": v(46.05, 28.2) * mm});
            skArc(sketch, "E52.89.3", {"start": v(43.99, 27.92) * mm, "mid": v(43.78, 28.24) * mm, "end": v(43.58, 28.55) * mm});
            skPoint(sketch, "E52.89.4", {"position": v(44.7, 30.31) * mm});
            skPoint(sketch, "E52.89.5", {"position": v(43.5, 28.67) * mm});
            skLineSegment(sketch, "E52.89.6", {"start": v(44.2, 27.83) * mm, "end": v(45.9, 28.18) * mm});
            skLineSegment(sketch, "E52.89.7", {"start": v(44.47, 30.64) * mm, "end": v(45.99, 29.27) * mm});
            skLineSegment(sketch, "E52.89.8", {"start": v(44.6, 30.2) * mm, "end": v(43.58, 28.78) * mm});
            skArc(sketch, "E52.89.9", {"start": v(43.99, 27.92) * mm, "mid": v(44.08, 27.84) * mm, "end": v(44.2, 27.83) * mm});
            skArc(sketch, "E52.89.10", {"start": v(43.58, 28.78) * mm, "mid": v(43.55, 28.67) * mm, "end": v(43.58, 28.55) * mm});
            skArc(sketch, "E52.89.11", {"start": v(44.6, 30.2) * mm, "mid": v(44.65, 30.31) * mm, "end": v(44.61, 30.43) * mm});
            skArc(sketch, "E52.89.12", {"start": v(46.12, 28.09) * mm, "mid": v(46.03, 28.17) * mm, "end": v(45.9, 28.18) * mm});
            skArc(sketch, "E52.89.13", {"start": v(46.25, 27.87) * mm, "mid": v(46.19, 27.98) * mm, "end": v(46.12, 28.09) * mm});
            skArc(sketch, "E52.89.14", {"start": v(44.61, 30.43) * mm, "mid": v(44.54, 30.53) * mm, "end": v(44.47, 30.64) * mm});
            skLineSegment(sketch, "E52.89.15", {"start": v(46.25, 27.87) * mm, "end": v(46.11, 28.1) * mm});
            skLineSegment(sketch, "E52.90.0", {"start": v(44.12, 32.02) * mm, "end": v(44.47, 30.63) * mm});
            skPoint(sketch, "E52.90.1", {"position": v(42.28, 30.44) * mm});
            skPoint(sketch, "E52.90.2", {"position": v(44.24, 30.96) * mm});
            skArc(sketch, "E52.90.3", {"start": v(42.2, 30.55) * mm, "mid": v(41.98, 30.85) * mm, "end": v(41.76, 31.16) * mm});
            skPoint(sketch, "E52.90.4", {"position": v(42.76, 32.98) * mm});
            skPoint(sketch, "E52.90.5", {"position": v(41.67, 31.27) * mm});
            skLineSegment(sketch, "E52.90.6", {"start": v(42.42, 30.47) * mm, "end": v(44.1, 30.93) * mm});
            skLineSegment(sketch, "E52.90.7", {"start": v(42.51, 33.3) * mm, "end": v(44.12, 32.02) * mm});
            skLineSegment(sketch, "E52.90.8", {"start": v(42.68, 32.86) * mm, "end": v(41.75, 31.38) * mm});
            skArc(sketch, "E52.90.9", {"start": v(42.2, 30.55) * mm, "mid": v(42.3, 30.48) * mm, "end": v(42.42, 30.47) * mm});
            skArc(sketch, "E52.90.10", {"start": v(41.75, 31.38) * mm, "mid": v(41.72, 31.27) * mm, "end": v(41.76, 31.16) * mm});
            skArc(sketch, "E52.90.11", {"start": v(42.68, 32.86) * mm, "mid": v(42.72, 32.98) * mm, "end": v(42.67, 33.09) * mm});
            skArc(sketch, "E52.90.12", {"start": v(44.32, 30.85) * mm, "mid": v(44.23, 30.92) * mm, "end": v(44.1, 30.93) * mm});
            skArc(sketch, "E52.90.13", {"start": v(44.47, 30.63) * mm, "mid": v(44.4, 30.74) * mm, "end": v(44.32, 30.85) * mm});
            skArc(sketch, "E52.90.14", {"start": v(42.67, 33.09) * mm, "mid": v(42.6, 33.2) * mm, "end": v(42.51, 33.3) * mm});
            skLineSegment(sketch, "E52.90.15", {"start": v(44.47, 30.63) * mm, "end": v(44.31, 30.86) * mm});
            skLineSegment(sketch, "E52.91.0", {"start": v(42.09, 34.65) * mm, "end": v(42.52, 33.29) * mm});
            skPoint(sketch, "E52.91.1", {"position": v(40.35, 32.96) * mm});
            skPoint(sketch, "E52.91.2", {"position": v(42.27, 33.6) * mm});
            skArc(sketch, "E52.91.3", {"start": v(40.26, 33.06) * mm, "mid": v(40.02, 33.36) * mm, "end": v(39.78, 33.65) * mm});
            skPoint(sketch, "E52.91.4", {"position": v(40.67, 35.52) * mm});
            skPoint(sketch, "E52.91.5", {"position": v(39.69, 33.75) * mm});
            skLineSegment(sketch, "E52.91.6", {"start": v(40.48, 33) * mm, "end": v(42.14, 33.56) * mm});
            skLineSegment(sketch, "E52.91.7", {"start": v(40.4, 35.82) * mm, "end": v(42.09, 34.65) * mm});
            skLineSegment(sketch, "E52.91.8", {"start": v(40.6, 35.4) * mm, "end": v(39.76, 33.87) * mm});
            skArc(sketch, "E52.91.9", {"start": v(40.26, 33.06) * mm, "mid": v(40.36, 33) * mm, "end": v(40.48, 33) * mm});
            skArc(sketch, "E52.91.10", {"start": v(39.76, 33.87) * mm, "mid": v(39.73, 33.76) * mm, "end": v(39.78, 33.65) * mm});
            skArc(sketch, "E52.91.11", {"start": v(40.6, 35.4) * mm, "mid": v(40.63, 35.52) * mm, "end": v(40.58, 35.63) * mm});
            skArc(sketch, "E52.91.12", {"start": v(42.36, 33.5) * mm, "mid": v(42.26, 33.56) * mm, "end": v(42.14, 33.56) * mm});
            skArc(sketch, "E52.91.13", {"start": v(42.52, 33.29) * mm, "mid": v(42.44, 33.4) * mm, "end": v(42.36, 33.5) * mm});
            skArc(sketch, "E52.91.14", {"start": v(40.58, 35.63) * mm, "mid": v(40.5, 35.73) * mm, "end": v(40.4, 35.82) * mm});
            skLineSegment(sketch, "E52.91.15", {"start": v(42.52, 33.29) * mm, "end": v(42.35, 33.5) * mm});
            skLineSegment(sketch, "E52.92.0", {"start": v(39.9, 37.15) * mm, "end": v(40.41, 35.82) * mm});
            skPoint(sketch, "E52.92.1", {"position": v(38.27, 35.36) * mm});
            skPoint(sketch, "E52.92.2", {"position": v(40.14, 36.12) * mm});
            skArc(sketch, "E52.92.3", {"start": v(38.17, 35.46) * mm, "mid": v(37.91, 35.73) * mm, "end": v(37.65, 36) * mm});
            skPoint(sketch, "E52.92.4", {"position": v(38.43, 37.94) * mm});
            skPoint(sketch, "E52.92.5", {"position": v(37.56, 36.1) * mm});
            skLineSegment(sketch, "E52.92.6", {"start": v(38.4, 35.4) * mm, "end": v(40.01, 36.06) * mm});
            skLineSegment(sketch, "E52.92.7", {"start": v(38.15, 38.22) * mm, "end": v(39.9, 37.15) * mm});
            skLineSegment(sketch, "E52.92.8", {"start": v(38.37, 37.81) * mm, "end": v(37.62, 36.23) * mm});
            skArc(sketch, "E52.92.9", {"start": v(38.17, 35.46) * mm, "mid": v(38.28, 35.4) * mm, "end": v(38.4, 35.4) * mm});
            skArc(sketch, "E52.92.10", {"start": v(37.62, 36.23) * mm, "mid": v(37.6, 36.11) * mm, "end": v(37.65, 36) * mm});
            skArc(sketch, "E52.92.11", {"start": v(38.37, 37.81) * mm, "mid": v(38.39, 37.93) * mm, "end": v(38.33, 38.04) * mm});
            skArc(sketch, "E52.92.12", {"start": v(40.24, 36.01) * mm, "mid": v(40.13, 36.07) * mm, "end": v(40.01, 36.06) * mm});
            skArc(sketch, "E52.92.13", {"start": v(40.41, 35.82) * mm, "mid": v(40.32, 35.92) * mm, "end": v(40.24, 36.01) * mm});
            skArc(sketch, "E52.92.14", {"start": v(38.33, 38.04) * mm, "mid": v(38.24, 38.13) * mm, "end": v(38.15, 38.22) * mm});
            skLineSegment(sketch, "E52.92.15", {"start": v(40.41, 35.82) * mm, "end": v(40.23, 36.02) * mm});
            skLineSegment(sketch, "E52.93.0", {"start": v(37.56, 39.51) * mm, "end": v(38.15, 38.22) * mm});
            skPoint(sketch, "E52.93.1", {"position": v(36.04, 37.62) * mm});
            skPoint(sketch, "E52.93.2", {"position": v(37.87, 38.5) * mm});
            skArc(sketch, "E52.93.3", {"start": v(35.94, 37.72) * mm, "mid": v(35.67, 37.98) * mm, "end": v(35.39, 38.24) * mm});
            skPoint(sketch, "E52.93.4", {"position": v(36.04, 40.2) * mm});
            skPoint(sketch, "E52.93.5", {"position": v(35.29, 38.33) * mm});
            skLineSegment(sketch, "E52.93.6", {"start": v(36.16, 37.68) * mm, "end": v(37.74, 38.44) * mm});
            skLineSegment(sketch, "E52.93.7", {"start": v(35.75, 40.48) * mm, "end": v(37.56, 39.51) * mm});
            skLineSegment(sketch, "E52.93.8", {"start": v(36, 40.08) * mm, "end": v(35.34, 38.46) * mm});
            skArc(sketch, "E52.93.9", {"start": v(35.94, 37.72) * mm, "mid": v(36.05, 37.67) * mm, "end": v(36.16, 37.68) * mm});
            skArc(sketch, "E52.93.10", {"start": v(35.34, 38.46) * mm, "mid": v(35.33, 38.34) * mm, "end": v(35.39, 38.24) * mm});
            skArc(sketch, "E52.93.11", {"start": v(36, 40.08) * mm, "mid": v(36, 40.2) * mm, "end": v(35.94, 40.3) * mm});
            skArc(sketch, "E52.93.12", {"start": v(37.97, 38.4) * mm, "mid": v(37.86, 38.45) * mm, "end": v(37.74, 38.44) * mm});
            skArc(sketch, "E52.93.13", {"start": v(38.15, 38.22) * mm, "mid": v(38.06, 38.3) * mm, "end": v(37.97, 38.4) * mm});
            skArc(sketch, "E52.93.14", {"start": v(35.94, 40.3) * mm, "mid": v(35.84, 40.39) * mm, "end": v(35.75, 40.48) * mm});
            skLineSegment(sketch, "E52.93.15", {"start": v(38.15, 38.22) * mm, "end": v(37.96, 38.4) * mm});
            skLineSegment(sketch, "E52.94.0", {"start": v(35.08, 41.73) * mm, "end": v(35.75, 40.47) * mm});
            skPoint(sketch, "E52.94.1", {"position": v(33.68, 39.75) * mm});
            skPoint(sketch, "E52.94.2", {"position": v(35.45, 40.73) * mm});
            skArc(sketch, "E52.94.3", {"start": v(33.57, 39.84) * mm, "mid": v(33.28, 40.08) * mm, "end": v(33, 40.32) * mm});
            skPoint(sketch, "E52.94.4", {"position": v(33.53, 42.33) * mm});
            skPoint(sketch, "E52.94.5", {"position": v(32.88, 40.41) * mm});
            skLineSegment(sketch, "E52.94.6", {"start": v(33.8, 39.82) * mm, "end": v(35.33, 40.67) * mm});
            skLineSegment(sketch, "E52.94.7", {"start": v(33.21, 42.58) * mm, "end": v(35.08, 41.73) * mm});
            skLineSegment(sketch, "E52.94.8", {"start": v(33.48, 42.2) * mm, "end": v(32.93, 40.54) * mm});
            skArc(sketch, "E52.94.9", {"start": v(33.57, 39.84) * mm, "mid": v(33.68, 39.8) * mm, "end": v(33.8, 39.82) * mm});
            skArc(sketch, "E52.94.10", {"start": v(32.93, 40.54) * mm, "mid": v(32.93, 40.42) * mm, "end": v(33, 40.32) * mm});
            skArc(sketch, "E52.94.11", {"start": v(33.48, 42.2) * mm, "mid": v(33.48, 42.32) * mm, "end": v(33.42, 42.42) * mm});
            skArc(sketch, "E52.94.12", {"start": v(35.56, 40.64) * mm, "mid": v(35.45, 40.7) * mm, "end": v(35.33, 40.67) * mm});
            skArc(sketch, "E52.94.13", {"start": v(35.75, 40.47) * mm, "mid": v(35.65, 40.56) * mm, "end": v(35.56, 40.64) * mm});
            skArc(sketch, "E52.94.14", {"start": v(33.42, 42.42) * mm, "mid": v(33.31, 42.5) * mm, "end": v(33.21, 42.58) * mm});
            skLineSegment(sketch, "E52.94.15", {"start": v(35.75, 40.47) * mm, "end": v(35.55, 40.65) * mm});
            skLineSegment(sketch, "E52.95.0", {"start": v(32.47, 43.79) * mm, "end": v(33.22, 42.58) * mm});
            skPoint(sketch, "E52.95.1", {"position": v(31.2, 41.73) * mm});
            skPoint(sketch, "E52.95.2", {"position": v(32.9, 42.82) * mm});
            skArc(sketch, "E52.95.3", {"start": v(31.08, 41.81) * mm, "mid": v(30.78, 42.04) * mm, "end": v(30.47, 42.26) * mm});
            skPoint(sketch, "E52.95.4", {"position": v(30.88, 44.3) * mm});
            skPoint(sketch, "E52.95.5", {"position": v(30.36, 42.34) * mm});
            skLineSegment(sketch, "E52.95.6", {"start": v(31.3, 41.8) * mm, "end": v(32.78, 42.74) * mm});
            skLineSegment(sketch, "E52.95.7", {"start": v(30.55, 44.52) * mm, "end": v(32.47, 43.79) * mm});
            skLineSegment(sketch, "E52.95.8", {"start": v(30.85, 44.16) * mm, "end": v(30.4, 42.47) * mm});
            skArc(sketch, "E52.95.9", {"start": v(31.08, 41.81) * mm, "mid": v(31.2, 41.77) * mm, "end": v(31.3, 41.8) * mm});
            skArc(sketch, "E52.95.10", {"start": v(30.4, 42.47) * mm, "mid": v(30.4, 42.35) * mm, "end": v(30.47, 42.26) * mm});
            skArc(sketch, "E52.95.11", {"start": v(30.85, 44.16) * mm, "mid": v(30.84, 44.28) * mm, "end": v(30.77, 44.38) * mm});
            skArc(sketch, "E52.95.12", {"start": v(33.01, 42.73) * mm, "mid": v(32.9, 42.78) * mm, "end": v(32.78, 42.74) * mm});
            skArc(sketch, "E52.95.13", {"start": v(33.22, 42.58) * mm, "mid": v(33.11, 42.65) * mm, "end": v(33.01, 42.73) * mm});
            skArc(sketch, "E52.95.14", {"start": v(30.77, 44.38) * mm, "mid": v(30.66, 44.45) * mm, "end": v(30.55, 44.52) * mm});
            skLineSegment(sketch, "E52.95.15", {"start": v(33.22, 42.58) * mm, "end": v(33, 42.74) * mm});
            skLineSegment(sketch, "E52.96.0", {"start": v(29.74, 45.69) * mm, "end": v(30.56, 44.52) * mm});
            skPoint(sketch, "E52.96.1", {"position": v(28.6, 43.55) * mm});
            skPoint(sketch, "E52.96.2", {"position": v(30.23, 44.75) * mm});
            skArc(sketch, "E52.96.3", {"start": v(28.48, 43.63) * mm, "mid": v(28.16, 43.84) * mm, "end": v(27.84, 44.04) * mm});
            skPoint(sketch, "E52.96.4", {"position": v(28.13, 46.1) * mm});
            skPoint(sketch, "E52.96.5", {"position": v(27.72, 44.11) * mm});
            skLineSegment(sketch, "E52.96.6", {"start": v(28.7, 43.64) * mm, "end": v(30.12, 44.66) * mm});
            skLineSegment(sketch, "E52.96.7", {"start": v(27.78, 46.3) * mm, "end": v(29.74, 45.69) * mm});
            skLineSegment(sketch, "E52.96.8", {"start": v(28.1, 45.96) * mm, "end": v(27.75, 44.25) * mm});
            skArc(sketch, "E52.96.9", {"start": v(28.48, 43.63) * mm, "mid": v(28.59, 43.6) * mm, "end": v(28.7, 43.64) * mm});
            skArc(sketch, "E52.96.10", {"start": v(27.75, 44.25) * mm, "mid": v(27.76, 44.13) * mm, "end": v(27.84, 44.04) * mm});
            skArc(sketch, "E52.96.11", {"start": v(28.1, 45.96) * mm, "mid": v(28.08, 46.08) * mm, "end": v(28, 46.17) * mm});
            skArc(sketch, "E52.96.12", {"start": v(30.35, 44.67) * mm, "mid": v(30.23, 44.7) * mm, "end": v(30.12, 44.66) * mm});
            skArc(sketch, "E52.96.13", {"start": v(30.56, 44.52) * mm, "mid": v(30.45, 44.6) * mm, "end": v(30.35, 44.67) * mm});
            skArc(sketch, "E52.96.14", {"start": v(28, 46.17) * mm, "mid": v(27.9, 46.24) * mm, "end": v(27.78, 46.3) * mm});
            skLineSegment(sketch, "E52.96.15", {"start": v(30.56, 44.52) * mm, "end": v(30.34, 44.67) * mm});
            skLineSegment(sketch, "E52.97.0", {"start": v(26.9, 47.41) * mm, "end": v(27.79, 46.3) * mm});
            skPoint(sketch, "E52.97.1", {"position": v(25.88, 45.22) * mm});
            skPoint(sketch, "E52.97.2", {"position": v(27.44, 46.5) * mm});
            skArc(sketch, "E52.97.3", {"start": v(25.76, 45.28) * mm, "mid": v(25.43, 45.47) * mm, "end": v(25.1, 45.65) * mm});
            skPoint(sketch, "E52.97.4", {"position": v(25.26, 47.73) * mm});
            skPoint(sketch, "E52.97.5", {"position": v(24.98, 45.72) * mm});
            skLineSegment(sketch, "E52.97.6", {"start": v(25.99, 45.3) * mm, "end": v(27.34, 46.42) * mm});
            skLineSegment(sketch, "E52.97.7", {"start": v(24.9, 47.91) * mm, "end": v(26.9, 47.41) * mm});
            skLineSegment(sketch, "E52.97.8", {"start": v(25.24, 47.59) * mm, "end": v(25, 45.86) * mm});
            skArc(sketch, "E52.97.9", {"start": v(25.76, 45.28) * mm, "mid": v(25.88, 45.26) * mm, "end": v(25.99, 45.3) * mm});
            skArc(sketch, "E52.97.10", {"start": v(25, 45.86) * mm, "mid": v(25.02, 45.74) * mm, "end": v(25.1, 45.65) * mm});
            skArc(sketch, "E52.97.11", {"start": v(25.24, 47.59) * mm, "mid": v(25.22, 47.7) * mm, "end": v(25.14, 47.8) * mm});
            skArc(sketch, "E52.97.12", {"start": v(27.57, 46.43) * mm, "mid": v(27.45, 46.46) * mm, "end": v(27.34, 46.42) * mm});
            skArc(sketch, "E52.97.13", {"start": v(27.79, 46.3) * mm, "mid": v(27.68, 46.37) * mm, "end": v(27.57, 46.43) * mm});
            skArc(sketch, "E52.97.14", {"start": v(25.14, 47.8) * mm, "mid": v(25.02, 47.85) * mm, "end": v(24.9, 47.91) * mm});
            skLineSegment(sketch, "E52.97.15", {"start": v(27.79, 46.3) * mm, "end": v(27.56, 46.44) * mm});
            skLineSegment(sketch, "E52.98.0", {"start": v(23.96, 48.97) * mm, "end": v(24.91, 47.9) * mm});
            skPoint(sketch, "E52.98.1", {"position": v(23.08, 46.71) * mm});
            skPoint(sketch, "E52.98.2", {"position": v(24.56, 48.1) * mm});
            skArc(sketch, "E52.98.3", {"start": v(22.95, 46.77) * mm, "mid": v(22.61, 46.94) * mm, "end": v(22.27, 47.1) * mm});
            skPoint(sketch, "E52.98.4", {"position": v(22.3, 49.18) * mm});
            skPoint(sketch, "E52.98.5", {"position": v(22.15, 47.16) * mm});
            skLineSegment(sketch, "E52.98.6", {"start": v(23.18, 46.8) * mm, "end": v(24.46, 48) * mm});
            skLineSegment(sketch, "E52.98.7", {"start": v(21.94, 49.34) * mm, "end": v(23.96, 48.97) * mm});
            skLineSegment(sketch, "E52.98.8", {"start": v(22.3, 49.04) * mm, "end": v(22.16, 47.3) * mm});
            skArc(sketch, "E52.98.9", {"start": v(22.95, 46.77) * mm, "mid": v(23.07, 46.75) * mm, "end": v(23.18, 46.8) * mm});
            skArc(sketch, "E52.98.10", {"start": v(22.16, 47.3) * mm, "mid": v(22.19, 47.18) * mm, "end": v(22.27, 47.1) * mm});
            skArc(sketch, "E52.98.11", {"start": v(22.3, 49.04) * mm, "mid": v(22.27, 49.16) * mm, "end": v(22.18, 49.24) * mm});
            skArc(sketch, "E52.98.12", {"start": v(24.68, 48.03) * mm, "mid": v(24.56, 48.05) * mm, "end": v(24.46, 48) * mm});
            skArc(sketch, "E52.98.13", {"start": v(24.91, 47.9) * mm, "mid": v(24.8, 47.97) * mm, "end": v(24.68, 48.03) * mm});
            skArc(sketch, "E52.98.14", {"start": v(22.18, 49.24) * mm, "mid": v(22.06, 49.29) * mm, "end": v(21.94, 49.34) * mm});
            skLineSegment(sketch, "E52.98.15", {"start": v(24.91, 47.9) * mm, "end": v(24.67, 48.03) * mm});
            skLineSegment(sketch, "E52.99.0", {"start": v(20.93, 50.33) * mm, "end": v(21.95, 49.34) * mm});
            skPoint(sketch, "E52.99.1", {"position": v(20.19, 48.03) * mm});
            skPoint(sketch, "E52.99.2", {"position": v(21.58, 49.5) * mm});
            skArc(sketch, "E52.99.3", {"start": v(20.06, 48.08) * mm, "mid": v(19.71, 48.23) * mm, "end": v(19.36, 48.37) * mm});
            skPoint(sketch, "E52.99.4", {"position": v(19.27, 50.45) * mm});
            skPoint(sketch, "E52.99.5", {"position": v(19.23, 48.42) * mm});
            skLineSegment(sketch, "E52.99.6", {"start": v(20.28, 48.13) * mm, "end": v(21.48, 49.4) * mm});
            skLineSegment(sketch, "E52.99.7", {"start": v(18.9, 50.59) * mm, "end": v(20.93, 50.33) * mm});
            skLineSegment(sketch, "E52.99.8", {"start": v(19.26, 50.3) * mm, "end": v(19.23, 48.56) * mm});
            skArc(sketch, "E52.99.9", {"start": v(20.06, 48.08) * mm, "mid": v(20.18, 48.07) * mm, "end": v(20.28, 48.13) * mm});
            skArc(sketch, "E52.99.10", {"start": v(19.23, 48.56) * mm, "mid": v(19.27, 48.44) * mm, "end": v(19.36, 48.37) * mm});
            skArc(sketch, "E52.99.11", {"start": v(19.26, 50.3) * mm, "mid": v(19.23, 50.42) * mm, "end": v(19.14, 50.5) * mm});
            skArc(sketch, "E52.99.12", {"start": v(21.7, 49.44) * mm, "mid": v(21.59, 49.46) * mm, "end": v(21.48, 49.4) * mm});
            skArc(sketch, "E52.99.13", {"start": v(21.95, 49.34) * mm, "mid": v(21.83, 49.4) * mm, "end": v(21.7, 49.44) * mm});
            skArc(sketch, "E52.99.14", {"start": v(19.14, 50.5) * mm, "mid": v(19.01, 50.54) * mm, "end": v(18.9, 50.59) * mm});
            skLineSegment(sketch, "E52.99.15", {"start": v(21.95, 49.34) * mm, "end": v(21.7, 49.45) * mm});
            skLineSegment(sketch, "E52.100.0", {"start": v(17.82, 51.52) * mm, "end": v(18.9, 50.59) * mm});
            skPoint(sketch, "E52.100.1", {"position": v(17.22, 49.17) * mm});
            skPoint(sketch, "E52.100.2", {"position": v(18.52, 50.72) * mm});
            skArc(sketch, "E52.100.3", {"start": v(17.1, 49.22) * mm, "mid": v(16.73, 49.34) * mm, "end": v(16.38, 49.46) * mm});
            skPoint(sketch, "E52.100.4", {"position": v(16.16, 51.53) * mm});
            skPoint(sketch, "E52.100.5", {"position": v(16.24, 49.5) * mm});
            skLineSegment(sketch, "E52.100.6", {"start": v(17.31, 49.28) * mm, "end": v(18.43, 50.62) * mm});
            skLineSegment(sketch, "E52.100.7", {"start": v(15.77, 51.65) * mm, "end": v(17.82, 51.52) * mm});
            skLineSegment(sketch, "E52.100.8", {"start": v(16.16, 51.39) * mm, "end": v(16.24, 49.64) * mm});
            skArc(sketch, "E52.100.9", {"start": v(17.1, 49.22) * mm, "mid": v(17.21, 49.21) * mm, "end": v(17.31, 49.28) * mm});
            skArc(sketch, "E52.100.10", {"start": v(16.24, 49.64) * mm, "mid": v(16.28, 49.53) * mm, "end": v(16.38, 49.46) * mm});
            skArc(sketch, "E52.100.11", {"start": v(16.16, 51.39) * mm, "mid": v(16.12, 51.5) * mm, "end": v(16.02, 51.57) * mm});
            skArc(sketch, "E52.100.12", {"start": v(18.66, 50.68) * mm, "mid": v(18.53, 50.68) * mm, "end": v(18.43, 50.62) * mm});
            skArc(sketch, "E52.100.13", {"start": v(18.9, 50.59) * mm, "mid": v(18.78, 50.63) * mm, "end": v(18.66, 50.68) * mm});
            skArc(sketch, "E52.100.14", {"start": v(16.02, 51.57) * mm, "mid": v(15.9, 51.6) * mm, "end": v(15.77, 51.65) * mm});
            skLineSegment(sketch, "E52.100.15", {"start": v(18.9, 50.59) * mm, "end": v(18.64, 50.68) * mm});
            skLineSegment(sketch, "E52.101.0", {"start": v(14.65, 52.5) * mm, "end": v(15.78, 51.64) * mm});
            skPoint(sketch, "E52.101.1", {"position": v(14.2, 50.13) * mm});
            skPoint(sketch, "E52.101.2", {"position": v(15.4, 51.76) * mm});
            skArc(sketch, "E52.101.3", {"start": v(14.06, 50.17) * mm, "mid": v(13.7, 50.27) * mm, "end": v(13.33, 50.37) * mm});
            skPoint(sketch, "E52.101.4", {"position": v(12.98, 52.42) * mm});
            skPoint(sketch, "E52.101.5", {"position": v(13.2, 50.4) * mm});
            skLineSegment(sketch, "E52.101.6", {"start": v(14.27, 50.24) * mm, "end": v(15.31, 51.65) * mm});
            skLineSegment(sketch, "E52.101.7", {"start": v(12.6, 52.51) * mm, "end": v(14.65, 52.5) * mm});
            skLineSegment(sketch, "E52.101.8", {"start": v(13, 52.28) * mm, "end": v(13.18, 50.54) * mm});
            skArc(sketch, "E52.101.9", {"start": v(14.06, 50.17) * mm, "mid": v(14.18, 50.17) * mm, "end": v(14.27, 50.24) * mm});
            skArc(sketch, "E52.101.10", {"start": v(13.18, 50.54) * mm, "mid": v(13.23, 50.43) * mm, "end": v(13.33, 50.37) * mm});
            skArc(sketch, "E52.101.11", {"start": v(13, 52.28) * mm, "mid": v(12.95, 52.39) * mm, "end": v(12.85, 52.45) * mm});
            skArc(sketch, "E52.101.12", {"start": v(15.53, 51.72) * mm, "mid": v(15.41, 51.72) * mm, "end": v(15.31, 51.65) * mm});
            skArc(sketch, "E52.101.13", {"start": v(15.78, 51.64) * mm, "mid": v(15.66, 51.68) * mm, "end": v(15.53, 51.72) * mm});
            skArc(sketch, "E52.101.14", {"start": v(12.85, 52.45) * mm, "mid": v(12.72, 52.48) * mm, "end": v(12.6, 52.51) * mm});
            skLineSegment(sketch, "E52.101.15", {"start": v(15.78, 51.64) * mm, "end": v(15.52, 51.72) * mm});
            skLineSegment(sketch, "E52.102.0", {"start": v(11.42, 53.3) * mm, "end": v(12.6, 52.5) * mm});
            skPoint(sketch, "E52.102.1", {"position": v(11.1, 50.9) * mm});
            skPoint(sketch, "E52.102.2", {"position": v(12.21, 52.6) * mm});
            skArc(sketch, "E52.102.3", {"start": v(10.97, 50.93) * mm, "mid": v(10.6, 51) * mm, "end": v(10.23, 51.08) * mm});
            skPoint(sketch, "E52.102.4", {"position": v(9.76, 53.1) * mm});
            skPoint(sketch, "E52.102.5", {"position": v(10.1, 51.11) * mm});
            skLineSegment(sketch, "E52.102.6", {"start": v(11.18, 51.02) * mm, "end": v(12.14, 52.48) * mm});
            skLineSegment(sketch, "E52.102.7", {"start": v(9.37, 53.18) * mm, "end": v(11.42, 53.3) * mm});
            skLineSegment(sketch, "E52.102.8", {"start": v(9.79, 52.97) * mm, "end": v(10.08, 51.25) * mm});
            skArc(sketch, "E52.102.9", {"start": v(10.97, 50.93) * mm, "mid": v(11.1, 50.94) * mm, "end": v(11.18, 51.02) * mm});
            skArc(sketch, "E52.102.10", {"start": v(10.08, 51.25) * mm, "mid": v(10.13, 51.14) * mm, "end": v(10.23, 51.08) * mm});
            skArc(sketch, "E52.102.11", {"start": v(9.79, 52.97) * mm, "mid": v(9.73, 53.08) * mm, "end": v(9.63, 53.14) * mm});
            skArc(sketch, "E52.102.12", {"start": v(12.35, 52.57) * mm, "mid": v(12.23, 52.56) * mm, "end": v(12.14, 52.48) * mm});
            skArc(sketch, "E52.102.13", {"start": v(12.6, 52.5) * mm, "mid": v(12.48, 52.54) * mm, "end": v(12.35, 52.57) * mm});
            skArc(sketch, "E52.102.14", {"start": v(9.63, 53.14) * mm, "mid": v(9.5, 53.16) * mm, "end": v(9.37, 53.18) * mm});
            skLineSegment(sketch, "E52.102.15", {"start": v(12.6, 52.5) * mm, "end": v(12.34, 52.57) * mm});
            skSolve(sketch);
        }
        {
            var Q0;
            {var subQ10=sQuery(id+"F25.wireOp",EDGE,"E40");Q0=makeQuery(id+"F25.imprint","IMPRINT",FACE,{"disambiguationData":[TD([[makeQuery(id+"F25.imprint","IMPRINT",EDGE,{"derivedFrom":subQ10}),1.0]])]});}
            var Q1;
            Q1=makeQuery(id+"F25.imprint","IMPRINT",FACE,{"disambiguationData":[TD([[makeQuery(id+"F25.imprint","IMPRINT",EDGE,{"derivedFrom":sQuery(id+"F25.wireOp",EDGE,"E52.1.3")}),-1.0]])]});
            var Q2;
            Q2=makeQuery(id+"F25.imprint","IMPRINT",FACE,{"disambiguationData":[TD([[makeQuery(id+"F25.imprint","IMPRINT",EDGE,{"derivedFrom":sQuery(id+"F25.wireOp",EDGE,"E52.2.3")}),-1.0]])]});
            var Q3;
            Q3=makeQuery(id+"F25.imprint","IMPRINT",FACE,{"disambiguationData":[TD([[makeQuery(id+"F25.imprint","IMPRINT",EDGE,{"derivedFrom":sQuery(id+"F25.wireOp",EDGE,"E52.3.3")}),-1.0]])]});
            var Q4;
            Q4=makeQuery(id+"F25.imprint","IMPRINT",FACE,{"disambiguationData":[TD([[makeQuery(id+"F25.imprint","IMPRINT",EDGE,{"derivedFrom":sQuery(id+"F25.wireOp",EDGE,"E52.4.3")}),-1.0]])]});
            var Q5;
            Q5=makeQuery(id+"F25.imprint","IMPRINT",FACE,{"disambiguationData":[TD([[makeQuery(id+"F25.imprint","IMPRINT",EDGE,{"derivedFrom":sQuery(id+"F25.wireOp",EDGE,"E52.5.3")}),-1.0]])]});
            var Q6;
            Q6=makeQuery(id+"F25.imprint","IMPRINT",FACE,{"disambiguationData":[TD([[makeQuery(id+"F25.imprint","IMPRINT",EDGE,{"derivedFrom":sQuery(id+"F25.wireOp",EDGE,"E52.6.3")}),-1.0]])]});
            var Q7;
            Q7=makeQuery(id+"F25.imprint","IMPRINT",FACE,{"disambiguationData":[TD([[makeQuery(id+"F25.imprint","IMPRINT",EDGE,{"derivedFrom":sQuery(id+"F25.wireOp",EDGE,"E52.7.3")}),-1.0]])]});
            extrude(context, id + "F26", {"entities" : qUnion([Q0, Q1, Q2, Q3, Q4, Q5, Q6, Q7]), "operationType" : NewBodyOperationType.REMOVE, "oppositeDirection" : true, "depth" : 5 * mm, "offsetDistance" : 25 * mm});
        }
        {
            var Q0;
            Q0=makeQuery(id+"F25.imprint","IMPRINT",FACE,{"disambiguationData":[TD([[makeQuery(id+"F25.imprint","IMPRINT",EDGE,{"derivedFrom":sQuery(id+"F25.wireOp",EDGE,"E52.8.3")}),-1.0]])]});
            var Q1;
            Q1=makeQuery(id+"F25.imprint","IMPRINT",FACE,{"disambiguationData":[TD([[makeQuery(id+"F25.imprint","IMPRINT",EDGE,{"derivedFrom":sQuery(id+"F25.wireOp",EDGE,"E52.9.3")}),-1.0]])]});
            var Q2;
            Q2=makeQuery(id+"F25.imprint","IMPRINT",FACE,{"disambiguationData":[TD([[makeQuery(id+"F25.imprint","IMPRINT",EDGE,{"derivedFrom":sQuery(id+"F25.wireOp",EDGE,"E52.10.3")}),-1.0]])]});
            var Q3;
            Q3=makeQuery(id+"F25.imprint","IMPRINT",FACE,{"disambiguationData":[TD([[makeQuery(id+"F25.imprint","IMPRINT",EDGE,{"derivedFrom":sQuery(id+"F25.wireOp",EDGE,"E52.11.3")}),-1.0]])]});
            var Q4;
            Q4=makeQuery(id+"F25.imprint","IMPRINT",FACE,{"disambiguationData":[TD([[makeQuery(id+"F25.imprint","IMPRINT",EDGE,{"derivedFrom":sQuery(id+"F25.wireOp",EDGE,"E52.12.3")}),-1.0]])]});
            var Q5;
            Q5=makeQuery(id+"F25.imprint","IMPRINT",FACE,{"disambiguationData":[TD([[makeQuery(id+"F25.imprint","IMPRINT",EDGE,{"derivedFrom":sQuery(id+"F25.wireOp",EDGE,"E52.13.3")}),-1.0]])]});
            var Q6;
            Q6=makeQuery(id+"F25.imprint","IMPRINT",FACE,{"disambiguationData":[TD([[makeQuery(id+"F25.imprint","IMPRINT",EDGE,{"derivedFrom":sQuery(id+"F25.wireOp",EDGE,"E52.14.3")}),-1.0]])]});
            var Q7;
            Q7=makeQuery(id+"F25.imprint","IMPRINT",FACE,{"disambiguationData":[TD([[makeQuery(id+"F25.imprint","IMPRINT",EDGE,{"derivedFrom":sQuery(id+"F25.wireOp",EDGE,"E52.15.3")}),-1.0]])]});
            var Q8;
            Q8=makeQuery(id+"F25.imprint","IMPRINT",FACE,{"disambiguationData":[TD([[makeQuery(id+"F25.imprint","IMPRINT",EDGE,{"derivedFrom":sQuery(id+"F25.wireOp",EDGE,"E52.16.3")}),-1.0]])]});
            var Q9;
            Q9=makeQuery(id+"F25.imprint","IMPRINT",FACE,{"disambiguationData":[TD([[makeQuery(id+"F25.imprint","IMPRINT",EDGE,{"derivedFrom":sQuery(id+"F25.wireOp",EDGE,"E52.17.3")}),-1.0]])]});
            var Q10;
            Q10=makeQuery(id+"F25.imprint","IMPRINT",FACE,{"disambiguationData":[TD([[makeQuery(id+"F25.imprint","IMPRINT",EDGE,{"derivedFrom":sQuery(id+"F25.wireOp",EDGE,"E52.19.3")}),-1.0]])]});
            var Q11;
            Q11=makeQuery(id+"F25.imprint","IMPRINT",FACE,{"disambiguationData":[TD([[makeQuery(id+"F25.imprint","IMPRINT",EDGE,{"derivedFrom":sQuery(id+"F25.wireOp",EDGE,"E52.18.3")}),-1.0]])]});
            var Q12;
            Q12=makeQuery(id+"F25.imprint","IMPRINT",FACE,{"disambiguationData":[TD([[makeQuery(id+"F25.imprint","IMPRINT",EDGE,{"derivedFrom":sQuery(id+"F25.wireOp",EDGE,"E52.20.3")}),-1.0]])]});
            var Q13;
            Q13=makeQuery(id+"F25.imprint","IMPRINT",FACE,{"disambiguationData":[TD([[makeQuery(id+"F25.imprint","IMPRINT",EDGE,{"derivedFrom":sQuery(id+"F25.wireOp",EDGE,"E52.21.3")}),-1.0]])]});
            var Q14;
            Q14=makeQuery(id+"F25.imprint","IMPRINT",FACE,{"disambiguationData":[TD([[makeQuery(id+"F25.imprint","IMPRINT",EDGE,{"derivedFrom":sQuery(id+"F25.wireOp",EDGE,"E52.22.3")}),-1.0]])]});
            var Q15;
            Q15=makeQuery(id+"F25.imprint","IMPRINT",FACE,{"disambiguationData":[TD([[makeQuery(id+"F25.imprint","IMPRINT",EDGE,{"derivedFrom":sQuery(id+"F25.wireOp",EDGE,"E52.23.3")}),-1.0]])]});
            extrude(context, id + "F27", {"entities" : qUnion([Q0, Q1, Q2, Q3, Q4, Q5, Q6, Q7, Q8, Q9, Q10, Q11, Q12, Q13, Q14, Q15]), "operationType" : NewBodyOperationType.REMOVE, "oppositeDirection" : true, "depth" : 25 * mm, "offsetDistance" : 25 * mm});
        }
        {
            var Q0;
            Q0=makeQuery(id+"F25.imprint","IMPRINT",FACE,{"disambiguationData":[TD([[makeQuery(id+"F25.imprint","IMPRINT",EDGE,{"derivedFrom":sQuery(id+"F25.wireOp",EDGE,"E52.24.3")}),-1.0]])]});
            var Q1;
            Q1=makeQuery(id+"F25.imprint","IMPRINT",FACE,{"disambiguationData":[TD([[makeQuery(id+"F25.imprint","IMPRINT",EDGE,{"derivedFrom":sQuery(id+"F25.wireOp",EDGE,"E52.25.3")}),-1.0]])]});
            var Q2;
            Q2=makeQuery(id+"F25.imprint","IMPRINT",FACE,{"disambiguationData":[TD([[makeQuery(id+"F25.imprint","IMPRINT",EDGE,{"derivedFrom":sQuery(id+"F25.wireOp",EDGE,"E52.26.3")}),-1.0]])]});
            var Q3;
            Q3=makeQuery(id+"F25.imprint","IMPRINT",FACE,{"disambiguationData":[TD([[makeQuery(id+"F25.imprint","IMPRINT",EDGE,{"derivedFrom":sQuery(id+"F25.wireOp",EDGE,"E52.27.3")}),-1.0]])]});
            var Q4;
            Q4=makeQuery(id+"F25.imprint","IMPRINT",FACE,{"disambiguationData":[TD([[makeQuery(id+"F25.imprint","IMPRINT",EDGE,{"derivedFrom":sQuery(id+"F25.wireOp",EDGE,"E52.28.3")}),-1.0]])]});
            var Q5;
            Q5=makeQuery(id+"F25.imprint","IMPRINT",FACE,{"disambiguationData":[TD([[makeQuery(id+"F25.imprint","IMPRINT",EDGE,{"derivedFrom":sQuery(id+"F25.wireOp",EDGE,"E52.29.3")}),-1.0]])]});
            var Q6;
            Q6=makeQuery(id+"F25.imprint","IMPRINT",FACE,{"disambiguationData":[TD([[makeQuery(id+"F25.imprint","IMPRINT",EDGE,{"derivedFrom":sQuery(id+"F25.wireOp",EDGE,"E52.30.3")}),-1.0]])]});
            var Q7;
            Q7=makeQuery(id+"F25.imprint","IMPRINT",FACE,{"disambiguationData":[TD([[makeQuery(id+"F25.imprint","IMPRINT",EDGE,{"derivedFrom":sQuery(id+"F25.wireOp",EDGE,"E52.31.3")}),-1.0]])]});
            var Q8;
            Q8=makeQuery(id+"F25.imprint","IMPRINT",FACE,{"disambiguationData":[TD([[makeQuery(id+"F25.imprint","IMPRINT",EDGE,{"derivedFrom":sQuery(id+"F25.wireOp",EDGE,"E52.32.3")}),-1.0]])]});
            var Q9;
            Q9=makeQuery(id+"F25.imprint","IMPRINT",FACE,{"disambiguationData":[TD([[makeQuery(id+"F25.imprint","IMPRINT",EDGE,{"derivedFrom":sQuery(id+"F25.wireOp",EDGE,"E52.33.3")}),-1.0]])]});
            var Q10;
            Q10=makeQuery(id+"F25.imprint","IMPRINT",FACE,{"disambiguationData":[TD([[makeQuery(id+"F25.imprint","IMPRINT",EDGE,{"derivedFrom":sQuery(id+"F25.wireOp",EDGE,"E52.34.3")}),-1.0]])]});
            var Q11;
            Q11=makeQuery(id+"F25.imprint","IMPRINT",FACE,{"disambiguationData":[TD([[makeQuery(id+"F25.imprint","IMPRINT",EDGE,{"derivedFrom":sQuery(id+"F25.wireOp",EDGE,"E52.35.3")}),-1.0]])]});
            var Q12;
            Q12=makeQuery(id+"F25.imprint","IMPRINT",FACE,{"disambiguationData":[TD([[makeQuery(id+"F25.imprint","IMPRINT",EDGE,{"derivedFrom":sQuery(id+"F25.wireOp",EDGE,"E52.36.3")}),-1.0]])]});
            var Q13;
            Q13=makeQuery(id+"F25.imprint","IMPRINT",FACE,{"disambiguationData":[TD([[makeQuery(id+"F25.imprint","IMPRINT",EDGE,{"derivedFrom":sQuery(id+"F25.wireOp",EDGE,"E52.37.3")}),-1.0]])]});
            var Q14;
            Q14=makeQuery(id+"F25.imprint","IMPRINT",FACE,{"disambiguationData":[TD([[makeQuery(id+"F25.imprint","IMPRINT",EDGE,{"derivedFrom":sQuery(id+"F25.wireOp",EDGE,"E52.38.3")}),-1.0]])]});
            var Q15;
            Q15=makeQuery(id+"F25.imprint","IMPRINT",FACE,{"disambiguationData":[TD([[makeQuery(id+"F25.imprint","IMPRINT",EDGE,{"derivedFrom":sQuery(id+"F25.wireOp",EDGE,"E52.39.3")}),-1.0]])]});
            var Q16;
            Q16=makeQuery(id+"F25.imprint","IMPRINT",FACE,{"disambiguationData":[TD([[makeQuery(id+"F25.imprint","IMPRINT",EDGE,{"derivedFrom":sQuery(id+"F25.wireOp",EDGE,"E52.40.3")}),-1.0]])]});
            var Q17;
            Q17=makeQuery(id+"F25.imprint","IMPRINT",FACE,{"disambiguationData":[TD([[makeQuery(id+"F25.imprint","IMPRINT",EDGE,{"derivedFrom":sQuery(id+"F25.wireOp",EDGE,"E52.41.3")}),-1.0]])]});
            extrude(context, id + "F28", {"entities" : qUnion([Q0, Q1, Q2, Q3, Q4, Q5, Q6, Q7, Q8, Q9, Q10, Q11, Q12, Q13, Q14, Q15, Q16, Q17]), "operationType" : NewBodyOperationType.REMOVE, "oppositeDirection" : true, "depth" : 25 * mm, "offsetDistance" : 25 * mm});
        }
        {
            var Q0;
            Q0=makeQuery(id+"F25.imprint","IMPRINT",FACE,{"disambiguationData":[TD([[makeQuery(id+"F25.imprint","IMPRINT",EDGE,{"derivedFrom":sQuery(id+"F25.wireOp",EDGE,"E52.42.3")}),-1.0]])]});
            var Q1;
            Q1=makeQuery(id+"F25.imprint","IMPRINT",FACE,{"disambiguationData":[TD([[makeQuery(id+"F25.imprint","IMPRINT",EDGE,{"derivedFrom":sQuery(id+"F25.wireOp",EDGE,"E52.43.3")}),-1.0]])]});
            var Q2;
            Q2=makeQuery(id+"F25.imprint","IMPRINT",FACE,{"disambiguationData":[TD([[makeQuery(id+"F25.imprint","IMPRINT",EDGE,{"derivedFrom":sQuery(id+"F25.wireOp",EDGE,"E52.44.3")}),-1.0]])]});
            var Q3;
            Q3=makeQuery(id+"F25.imprint","IMPRINT",FACE,{"disambiguationData":[TD([[makeQuery(id+"F25.imprint","IMPRINT",EDGE,{"derivedFrom":sQuery(id+"F25.wireOp",EDGE,"E52.45.3")}),-1.0]])]});
            var Q4;
            Q4=makeQuery(id+"F25.imprint","IMPRINT",FACE,{"disambiguationData":[TD([[makeQuery(id+"F25.imprint","IMPRINT",EDGE,{"derivedFrom":sQuery(id+"F25.wireOp",EDGE,"E52.46.3")}),-1.0]])]});
            var Q5;
            Q5=makeQuery(id+"F25.imprint","IMPRINT",FACE,{"disambiguationData":[TD([[makeQuery(id+"F25.imprint","IMPRINT",EDGE,{"derivedFrom":sQuery(id+"F25.wireOp",EDGE,"E52.47.3")}),-1.0]])]});
            var Q6;
            Q6=makeQuery(id+"F25.imprint","IMPRINT",FACE,{"disambiguationData":[TD([[makeQuery(id+"F25.imprint","IMPRINT",EDGE,{"derivedFrom":sQuery(id+"F25.wireOp",EDGE,"E52.48.3")}),-1.0]])]});
            var Q7;
            Q7=makeQuery(id+"F25.imprint","IMPRINT",FACE,{"disambiguationData":[TD([[makeQuery(id+"F25.imprint","IMPRINT",EDGE,{"derivedFrom":sQuery(id+"F25.wireOp",EDGE,"E52.49.3")}),-1.0]])]});
            var Q8;
            Q8=makeQuery(id+"F25.imprint","IMPRINT",FACE,{"disambiguationData":[TD([[makeQuery(id+"F25.imprint","IMPRINT",EDGE,{"derivedFrom":sQuery(id+"F25.wireOp",EDGE,"E52.50.3")}),-1.0]])]});
            extrude(context, id + "F29", {"entities" : qUnion([Q0, Q1, Q2, Q3, Q4, Q5, Q6, Q7, Q8]), "operationType" : NewBodyOperationType.REMOVE, "oppositeDirection" : true, "depth" : 25 * mm, "offsetDistance" : 25 * mm});
        }
        {
            var Q0;
            Q0=makeQuery(id+"F25.imprint","IMPRINT",FACE,{"disambiguationData":[TD([[makeQuery(id+"F25.imprint","IMPRINT",EDGE,{"derivedFrom":sQuery(id+"F25.wireOp",EDGE,"E52.51.3")}),-1.0]])]});
            var Q1;
            Q1=makeQuery(id+"F25.imprint","IMPRINT",FACE,{"disambiguationData":[TD([[makeQuery(id+"F25.imprint","IMPRINT",EDGE,{"derivedFrom":sQuery(id+"F25.wireOp",EDGE,"E52.52.3")}),-1.0]])]});
            var Q2;
            Q2=makeQuery(id+"F25.imprint","IMPRINT",FACE,{"disambiguationData":[TD([[makeQuery(id+"F25.imprint","IMPRINT",EDGE,{"derivedFrom":sQuery(id+"F25.wireOp",EDGE,"E52.53.3")}),-1.0]])]});
            var Q3;
            Q3=makeQuery(id+"F25.imprint","IMPRINT",FACE,{"disambiguationData":[TD([[makeQuery(id+"F25.imprint","IMPRINT",EDGE,{"derivedFrom":sQuery(id+"F25.wireOp",EDGE,"E52.54.3")}),-1.0]])]});
            var Q4;
            Q4=makeQuery(id+"F25.imprint","IMPRINT",FACE,{"disambiguationData":[TD([[makeQuery(id+"F25.imprint","IMPRINT",EDGE,{"derivedFrom":sQuery(id+"F25.wireOp",EDGE,"E52.55.3")}),-1.0]])]});
            var Q5;
            Q5=makeQuery(id+"F25.imprint","IMPRINT",FACE,{"disambiguationData":[TD([[makeQuery(id+"F25.imprint","IMPRINT",EDGE,{"derivedFrom":sQuery(id+"F25.wireOp",EDGE,"E52.56.3")}),-1.0]])]});
            var Q6;
            Q6=makeQuery(id+"F25.imprint","IMPRINT",FACE,{"disambiguationData":[TD([[makeQuery(id+"F25.imprint","IMPRINT",EDGE,{"derivedFrom":sQuery(id+"F25.wireOp",EDGE,"E52.57.3")}),-1.0]])]});
            extrude(context, id + "F30", {"entities" : qUnion([Q0, Q1, Q2, Q3, Q4, Q5, Q6]), "operationType" : NewBodyOperationType.REMOVE, "oppositeDirection" : true, "depth" : 25 * mm, "offsetDistance" : 25 * mm});
        }
        {
            var Q0;
            Q0=sQuery(id+"F1.wireOp",EDGE,"E5");
            cPlane(context, id + "F31", {"entities" : qUnion([Q0]), "cplaneType" : CPlaneType.LINE_ANGLE, "offset" : 25 * mm, "angle" : 0 * degree, "width" : 150 * mm, "height" : 150 * mm});
        }
        {
            var Q0;
            Q0=makeQuery(id+"F14.boolean.opBoolean","COPY",FACE,{"derivedFrom":makeQuery(id+"F14.opExtrude","SWEPT_FACE",FACE,{"disambiguationData":[OSD([sQuery(id+"F13.wireOp",EDGE,"E13")])]})});
            cPlane(context, id + "F32", {"entities" : qUnion([Q0]), "cplaneType" : CPlaneType.LINE_ANGLE, "offset" : 25 * mm, "angle" : 0 * degree, "width" : 150 * mm, "height" : 150 * mm});
        }
        {
            var Q0;
            Q0=qCreatedBy(id+"F32.planeOp",FACE);
            var sketch = newSketch(context, id + "F33", { "sketchPlane" : qUnion([Q0])});
            skLineSegment(sketch, "E53", {"start": v(0, 0) * mm, "end": v(-50.3, 0) * mm});
            skLineSegment(sketch, "E54", {"start": v(-50.3, 0) * mm, "end": v(-51.3, 0) * mm});
            skLineSegment(sketch, "E55", {"start": v(-51.3, 0) * mm, "end": v(-51.3, 2) * mm});
            skLineSegment(sketch, "E56", {"start": v(-51.3, 2) * mm, "end": v(-50.3, 0) * mm});
            skLineSegment(sketch, "E57", {"start": v(-51.3, 2) * mm, "end": v(-50.3, 2) * mm});
            skLineSegment(sketch, "E58", {"start": v(-50.3, 2) * mm, "end": v(-50.3, 0) * mm});
            skLineSegment(sketch, "E59", {"start": v(-50.3, 2) * mm, "end": v(-49.3, 2) * mm});
            skLineSegment(sketch, "E60", {"start": v(-49.3, 2) * mm, "end": v(-49.3, 0) * mm});
            skSolve(sketch);
        }
        {
            var Q0;
            Q0=makeQuery(id+"F33.imprint","IMPRINT",FACE,{"disambiguationData":[TD([[makeQuery(id+"F33.imprint","IMPRINT",EDGE,{"derivedFrom":sQuery(id+"F33.wireOp",EDGE,"E56")}),1.0]])]});
            var Q1;
            {var subQ0=sQuery(id+"F33.wireOp",EDGE,"E58");Q1=makeQuery(id+"F33.imprint","IMPRINT",FACE,{"disambiguationData":[TD([[makeQuery(id+"F33.imprint","IMPRINT",EDGE,{"derivedFrom":subQ0}),1.0]])]});}
            var Q2;
            Q2=makeQuery(id+"F14.boolean.opBoolean","COPY",FACE,{"derivedFrom":makeQuery(id+"F14.opExtrude","SWEPT_FACE",FACE,{"disambiguationData":[OSD([sQuery(id+"F13.wireOp",EDGE,"E13")])]})});
            revolve(context, id + "F34", {"operationType" : NewBodyOperationType.REMOVE, "surfaceOperationType" : NewSurfaceOperationType.NEW, "entities" : qUnion([Q0, Q1]), "axis" : qUnion([Q2]), "revolveType" : RevolveType.FULL, "oppositeDirection" : true});
        }
        {
            var Q0;
            Q0=makeQuery(id+"F16.boolean.opBoolean","COPY",FACE,{"derivedFrom":makeQuery(id+"F16.opExtrude","SWEPT_FACE",FACE,{"disambiguationData":[OSD([sQuery(id+"F15.wireOp",EDGE,"E16")])]})});
            cPlane(context, id + "F35", {"entities" : qUnion([Q0]), "cplaneType" : CPlaneType.LINE_ANGLE, "offset" : 25 * mm, "angle" : 0 * degree, "width" : 150 * mm, "height" : 150 * mm});
        }
        {
            var Q0;
            Q0=qCreatedBy(id+"F35.planeOp",FACE);
            var sketch = newSketch(context, id + "F36", { "sketchPlane" : qUnion([Q0])});
            skLineSegment(sketch, "E61", {"start": v(0, 0) * mm, "end": v(18.31, 0) * mm});
            skLineSegment(sketch, "E62", {"start": v(0, 0) * mm, "end": v(19.13, -46.2) * mm});
            skLineSegment(sketch, "E63", {"start": v(19.13, -46.2) * mm, "end": v(55.4, -9.92) * mm});
            skLineSegment(sketch, "E64", {"start": v(55.4, -9.92) * mm, "end": v(54, -8.5) * mm});
            skLineSegment(sketch, "E65", {"start": v(54, -8.5) * mm, "end": v(54.7, -7.8) * mm});
            skLineSegment(sketch, "E66", {"start": v(54.7, -7.8) * mm, "end": v(55.4, -9.92) * mm});
            skLineSegment(sketch, "E67", {"start": v(54, -8.5) * mm, "end": v(53.29, -9.21) * mm});
            skLineSegment(sketch, "E68", {"start": v(53.29, -9.21) * mm, "end": v(54.7, -10.63) * mm});
            skSolve(sketch);
        }
        {
            var Q0;
            Q0=makeQuery(id+"F36.imprint","IMPRINT",FACE,{"disambiguationData":[TD([[makeQuery(id+"F36.imprint","IMPRINT",EDGE,{"derivedFrom":sQuery(id+"F36.wireOp",EDGE,"E64")}),-1.0]])]});
            var Q1;
            {var subQ0=sQuery(id+"F36.wireOp",EDGE,"E64");Q1=makeQuery(id+"F36.imprint","IMPRINT",FACE,{"disambiguationData":[TD([[makeQuery(id+"F36.imprint","IMPRINT",EDGE,{"derivedFrom":subQ0}),1.0]])]});}
            var Q2;
            Q2=makeQuery(id+"F16.boolean.opBoolean","COPY",FACE,{"derivedFrom":makeQuery(id+"F16.opExtrude","SWEPT_FACE",FACE,{"disambiguationData":[OSD([sQuery(id+"F15.wireOp",EDGE,"E16")])]})});
            revolve(context, id + "F37", {"operationType" : NewBodyOperationType.REMOVE, "surfaceOperationType" : NewSurfaceOperationType.NEW, "entities" : qUnion([Q0, Q1]), "axis" : qUnion([Q2]), "revolveType" : RevolveType.FULL, "oppositeDirection" : true});
        }
        {
            var Q0;
            Q0=sQuery(id+"F1.wireOp",EDGE,"E5");
            cPlane(context, id + "F38", {"entities" : qUnion([Q0]), "cplaneType" : CPlaneType.LINE_ANGLE, "offset" : 25 * mm, "angle" : 0 * degree, "width" : 150 * mm, "height" : 150 * mm});
        }
    });
